# Revit family: d0088496_REVIT-QS
name_source: partatom
category: Mechanical Equipment
revit_build: Autodesk Revit 2017 (Build: 20190507_1515(x64)
units: mm (PartAtom-declared; Revit-internal decimal feet)

## family parameters
Always vertical = Yes
Cut with Voids When Loaded = No
Part Type = Normal
Room Calculation Point = No
Round Connector Dimension = Use Radius
Shared = No
Work Plane-Based = No

## types (134) — shared parameters
Apparent Load = 240 VA
Current = 2 A
Description = PVI QuickDraw® - Steam Storage
Disclaimer = This rendering is for building modeling purposes only. Submittal/catalog is still the contract document. PVI reserves the right to change design and specification without notice.
Drain Angle = 0.00°
Energy Radius = 14 1/2"
Frequency = 60 Hz
Manufacturer = PVI Industries, LLC
Phase = 1
Rear Access Extension = 0"
Relief Valve NPT = 1"
Relief Valve Radius = 1/2"
URL = www.pvi.com
Voltage = 120 V

## per-type parameters (varying)
- 900 L 150A-QS: Assembly Code=D3040400; Cold Water Extension=19 1/8"; Cold Water NPT=2"; Cold Water Radius=1"; Control Panel Extension=25 1/8"; Drain Extension=22"; Drain NPT=1"; Drain Radius=1/2"; Enclosure Location=15 1/2"; Energy Extension=34 1/8"; Flat Side Distance=34"; Front Skid Extension=72 5/8"; Height to Cold Inlet=14 13/16"; Height to Drain=1 3/4"; Height to Energy=26 1/2"; Height to Hot Outlet=44 7/8"; Height to Relief=51 7/8"; Hot Outlet Angle=0.00°; Hot Water Extension=19 1/8"; Hot Water NPT=2"; Hot Water Radius=1"; Large Visibility=No; Rear Skid Extension=18 1/8"; Recovery Rate 40F to 140F @15psi=900 gph; Relief Extension=21 1/8"; Skid Center Dist=8 1/2"; Skid Length=54 1/2"; Skid Spacing=17"; Small Visibility=Yes; Steam Return NPT=1"; Steam Return Radius=1/2"; Steam Return Y=2 9/16"; Steam Supply Conn Y=1 7/8"; Steam Supply NPT=2"; Steam Supply Radius=1"; Steam Supply Total Z=18"; Steam Supply X=14 1/16"; Steam Supply Y=1 7/8"; Steam Supply Z=9 1/16"; Steam flow lb/h 40F to 140F @15psi=780; Supply Pipe Conn Y=1 7/8"; U Tube Extension=8 15/16"; U Tube Radius=3 3/8"; Unit Height=63"; Unit Radius=18 1/8"; Weight=1095
- 830 L 150A-QSD: Assembly Code=D3040400; Cold Water Extension=19 1/8"; Cold Water NPT=2"; Cold Water Radius=1"; Control Panel Extension=25 1/8"; Drain Extension=22"; Drain NPT=1"; Drain Radius=1/2"; Enclosure Location=15 1/2"; Energy Extension=34 1/8"; Flat Side Distance=34"; Front Skid Extension=73 1/8"; Height to Cold Inlet=14 13/16"; Height to Drain=1 3/4"; Height to Energy=26 1/2"; Height to Hot Outlet=44 7/8"; Height to Relief=51 7/8"; Hot Outlet Angle=0.00°; Hot Water Extension=19 1/8"; Hot Water NPT=2"; Hot Water Radius=1"; Large Visibility=Yes; Rear Skid Extension=18 1/8"; Recovery Rate 40F to 140F @15psi=830 gph; Relief Extension=21 1/8"; Skid Center Dist=8 1/2"; Skid Length=55"; Skid Spacing=17"; Small Visibility=No; Steam Return NPT=1"; Steam Return Radius=1/2"; Steam Return Y=3 3/8"; Steam Supply Conn Y=2 1/4"; Steam Supply NPT=1 1/2"; Steam Supply Radius=3/4"; Steam Supply Total Z=18"; Steam Supply X=14 1/16"; Steam Supply Y=1 7/8"; Steam Supply Z=9 1/16"; Steam flow lb/h 40F to 140F @15psi=720; Supply Pipe Conn Y=4 1/8"; U Tube Extension=8 15/16"; U Tube Radius=4 5/16"; Unit Height=63"; Unit Radius=18 1/8"; Weight=1156
- 520 L 215A-QS: Assembly Code=D3040400; Cold Water Extension=19 1/8"; Cold Water NPT=2"; Cold Water Radius=1"; Control Panel Extension=25 1/8"; Drain Extension=22"; Drain NPT=1"; Drain Radius=1/2"; Enclosure Location=26"; Energy Extension=34 1/8"; Flat Side Distance=34"; Front Skid Extension=72 5/8"; Height to Cold Inlet=14 13/16"; Height to Drain=1 3/4"; Height to Energy=26 1/2"; Height to Hot Outlet=64 1/4"; Height to Relief=64 7/8"; Hot Outlet Angle=90.00°; Hot Water Extension=19 1/8"; Hot Water NPT=2"; Hot Water Radius=1"; Large Visibility=No; Rear Skid Extension=18 1/8"; Recovery Rate 40F to 140F @15psi=520 gph; Relief Extension=21 1/8"; Skid Center Dist=8 1/2"; Skid Length=54 1/2"; Skid Spacing=17"; Small Visibility=Yes; Steam Return NPT=3/4"; Steam Return Radius=3/8"; Steam Return Y=1 11/16"; Steam Supply Conn Y=1 5/16"; Steam Supply NPT=1 1/2"; Steam Supply Radius=3/4"; Steam Supply Total Z=15 5/16"; Steam Supply X=12 11/16"; Steam Supply Y=1 5/16"; Steam Supply Z=7 1/8"; Steam flow lb/h 40F to 140F @15psi=450; Supply Pipe Conn Y=1 5/16"; U Tube Extension=8 3/16"; U Tube Radius=2 1/4"; Unit Height=76"; Unit Radius=18 1/8"; Weight=1170
- 520 L 175A-QS: Assembly Code=D3040400; Cold Water Extension=19 1/8"; Cold Water NPT=2"; Cold Water Radius=1"; Control Panel Extension=25 1/8"; Drain Extension=22"; Drain NPT=1"; Drain Radius=1/2"; Enclosure Location=20"; Energy Extension=34 1/8"; Flat Side Distance=34"; Front Skid Extension=72 5/8"; Height to Cold Inlet=14 13/16"; Height to Drain=1 3/4"; Height to Energy=26 1/2"; Height to Hot Outlet=50 7/8"; Height to Relief=57 7/8"; Hot Outlet Angle=0.00°; Hot Water Extension=19 1/8"; Hot Water NPT=2"; Hot Water Radius=1"; Large Visibility=No; Rear Skid Extension=18 1/8"; Recovery Rate 40F to 140F @15psi=520 gph; Relief Extension=21 1/8"; Skid Center Dist=8 1/2"; Skid Length=54 1/2"; Skid Spacing=17"; Small Visibility=Yes; Steam Return NPT=3/4"; Steam Return Radius=3/8"; Steam Return Y=1 11/16"; Steam Supply Conn Y=1 5/16"; Steam Supply NPT=1 1/2"; Steam Supply Radius=3/4"; Steam Supply Total Z=15 5/16"; Steam Supply X=12 11/16"; Steam Supply Y=1 5/16"; Steam Supply Z=7 1/8"; Steam flow lb/h 40F to 140F @15psi=450; Supply Pipe Conn Y=1 5/16"; U Tube Extension=8 3/16"; U Tube Radius=2 1/4"; Unit Height=69"; Unit Radius=18 1/8"; Weight=1080
- 440 L 215A-QSD: Assembly Code=D3040400; Cold Water Extension=19 1/8"; Cold Water NPT=2"; Cold Water Radius=1"; Control Panel Extension=25 1/8"; Drain Extension=22"; Drain NPT=1"; Drain Radius=1/2"; Enclosure Location=26"; Energy Extension=34 1/8"; Flat Side Distance=34"; Front Skid Extension=72 5/8"; Height to Cold Inlet=14 13/16"; Height to Drain=1 3/4"; Height to Energy=26 1/2"; Height to Hot Outlet=64 1/4"; Height to Relief=64 7/8"; Hot Outlet Angle=90.00°; Hot Water Extension=19 1/8"; Hot Water NPT=2"; Hot Water Radius=1"; Large Visibility=No; Rear Skid Extension=18 1/8"; Recovery Rate 40F to 140F @15psi=440 gph; Relief Extension=21 1/8"; Skid Center Dist=8 1/2"; Skid Length=54 1/2"; Skid Spacing=17"; Small Visibility=Yes; Steam Return NPT=3/4"; Steam Return Radius=3/8"; Steam Return Y=1 11/16"; Steam Supply Conn Y=1 5/16"; Steam Supply NPT=1"; Steam Supply Radius=1/2"; Steam Supply Total Z=15 5/16"; Steam Supply X=12 11/16"; Steam Supply Y=1 5/16"; Steam Supply Z=7 1/8"; Steam flow lb/h 40F to 140F @15psi=380; Supply Pipe Conn Y=1 5/16"; U Tube Extension=8 3/16"; U Tube Radius=2 1/4"; Unit Height=76"; Unit Radius=18 1/8"; Weight=1220
- 440 L 175A-QSD: Assembly Code=D3040400; Cold Water Extension=19 1/8"; Cold Water NPT=2"; Cold Water Radius=1"; Control Panel Extension=25 1/8"; Drain Extension=22"; Drain NPT=1"; Drain Radius=1/2"; Enclosure Location=20"; Energy Extension=34 1/8"; Flat Side Distance=34"; Front Skid Extension=73 1/8"; Height to Cold Inlet=14 13/16"; Height to Drain=1 3/4"; Height to Energy=26 1/2"; Height to Hot Outlet=50 7/8"; Height to Relief=57 7/8"; Hot Outlet Angle=0.00°; Hot Water Extension=19 1/8"; Hot Water NPT=2"; Hot Water Radius=1"; Large Visibility=No; Rear Skid Extension=18 1/8"; Recovery Rate 40F to 140F @15psi=440 gph; Relief Extension=21 1/8"; Skid Center Dist=8 1/2"; Skid Length=55"; Skid Spacing=17"; Small Visibility=Yes; Steam Return NPT=3/4"; Steam Return Radius=3/8"; Steam Return Y=1 11/16"; Steam Supply Conn Y=1 5/16"; Steam Supply NPT=1"; Steam Supply Radius=1/2"; Steam Supply Total Z=15 5/16"; Steam Supply X=12 11/16"; Steam Supply Y=1 5/16"; Steam Supply Z=7 1/8"; Steam flow lb/h 40F to 140F @15psi=380; Supply Pipe Conn Y=1 5/16"; U Tube Extension=8 3/16"; U Tube Radius=2 1/4"; Unit Height=69"; Unit Radius=18 1/8"; Weight=1130
- 520 L 150A-QS: Assembly Code=D3040400; Cold Water Extension=19 1/8"; Cold Water NPT=2"; Cold Water Radius=1"; Control Panel Extension=25 1/8"; Drain Extension=22"; Drain NPT=1"; Drain Radius=1/2"; Enclosure Location=15 1/2"; Energy Extension=34 1/8"; Flat Side Distance=34"; Front Skid Extension=72 5/8"; Height to Cold Inlet=14 13/16"; Height to Drain=1 3/4"; Height to Energy=26 1/2"; Height to Hot Outlet=44 7/8"; Height to Relief=51 7/8"; Hot Outlet Angle=0.00°; Hot Water Extension=19 1/8"; Hot Water NPT=2"; Hot Water Radius=1"; Large Visibility=No; Rear Skid Extension=18 1/8"; Recovery Rate 40F to 140F @15psi=520 gph; Relief Extension=21 1/8"; Skid Center Dist=8 1/2"; Skid Length=54 1/2"; Skid Spacing=17"; Small Visibility=Yes; Steam Return NPT=3/4"; Steam Return Radius=3/8"; Steam Return Y=1 11/16"; Steam Supply Conn Y=1 5/16"; Steam Supply NPT=1 1/2"; Steam Supply Radius=3/4"; Steam Supply Total Z=15 5/16"; Steam Supply X=12 11/16"; Steam Supply Y=1 5/16"; Steam Supply Z=7 1/8"; Steam flow lb/h 40F to 140F @15psi=450; Supply Pipe Conn Y=1 5/16"; U Tube Extension=8 3/16"; U Tube Radius=2 1/4"; Unit Height=63"; Unit Radius=18 1/8"; Weight=1010
- 3790 L 215A-QSD: Assembly Code=D3040400; Cold Water Extension=19 1/8"; Cold Water NPT=2"; Cold Water Radius=1"; Control Panel Extension=25 1/8"; Drain Extension=22"; Drain NPT=1"; Drain Radius=1/2"; Enclosure Location=26"; Energy Extension=34 1/8"; Flat Side Distance=34"; Front Skid Extension=72 5/8"; Height to Cold Inlet=14 13/16"; Height to Drain=1 3/4"; Height to Energy=26 1/2"; Height to Hot Outlet=64 1/4"; Height to Relief=64 7/8"; Hot Outlet Angle=90.00°; Hot Water Extension=19 1/8"; Hot Water NPT=2"; Hot Water Radius=1"; Large Visibility=Yes; Rear Skid Extension=18 1/8"; Recovery Rate 40F to 140F @15psi=3790 gph; Relief Extension=21 1/8"; Skid Center Dist=8 1/2"; Skid Length=54 1/2"; Skid Spacing=17"; Small Visibility=No; Steam Return NPT=2"; Steam Return Radius=1"; Steam Return Y=4 5/8"; Steam Supply Conn Y=3 13/16"; Steam Supply NPT=2 1/2"; Steam Supply Radius=1 1/4"; Steam Supply Total Z=18 15/16"; Steam Supply X=25 1/2"; Steam Supply Y=8 9/16"; Steam Supply Z=10 13/16"; Steam flow lb/h 40F to 140F @15psi=3300; Supply Pipe Conn Y=12 3/8"; U Tube Extension=8 1/8"; U Tube Radius=6 3/8"; Unit Height=76"; Unit Radius=18 1/8"; Weight=1670
- 3790 L 175A-QSD: Assembly Code=D3040400; Cold Water Extension=19 1/8"; Cold Water NPT=2"; Cold Water Radius=1"; Control Panel Extension=25 1/8"; Drain Extension=22"; Drain NPT=1"; Drain Radius=1/2"; Enclosure Location=20"; Energy Extension=34 1/8"; Flat Side Distance=34"; Front Skid Extension=72 5/8"; Height to Cold Inlet=14 13/16"; Height to Drain=1 3/4"; Height to Energy=26 1/2"; Height to Hot Outlet=50 7/8"; Height to Relief=57 7/8"; Hot Outlet Angle=0.00°; Hot Water Extension=19 1/8"; Hot Water NPT=2"; Hot Water Radius=1"; Large Visibility=Yes; Rear Skid Extension=18 1/8"; Recovery Rate 40F to 140F @15psi=3790 gph; Relief Extension=21 1/8"; Skid Center Dist=8 1/2"; Skid Length=54 1/2"; Skid Spacing=17"; Small Visibility=No; Steam Return NPT=2"; Steam Return Radius=1"; Steam Return Y=4 5/8"; Steam Supply Conn Y=3 13/16"; Steam Supply NPT=2 1/2"; Steam Supply Radius=1 1/4"; Steam Supply Total Z=18 15/16"; Steam Supply X=25 1/2"; Steam Supply Y=8 9/16"; Steam Supply Z=10 13/16"; Steam flow lb/h 40F to 140F @15psi=3300; Supply Pipe Conn Y=12 3/8"; U Tube Extension=8 1/8"; U Tube Radius=6 3/8"; Unit Height=69"; Unit Radius=18 1/8"; Weight=1580
- 380 L 215A-QS: Assembly Code=D3040400; Cold Water Extension=19 1/8"; Cold Water NPT=2"; Cold Water Radius=1"; Control Panel Extension=25 1/8"; Drain Extension=22"; Drain NPT=1"; Drain Radius=1/2"; Enclosure Location=26"; Energy Extension=23 1/8"; Flat Side Distance=34"; Front Skid Extension=55 1/8"; Height to Cold Inlet=14 13/16"; Height to Drain=1 3/4"; Height to Energy=26 1/2"; Height to Hot Outlet=64 1/4"; Height to Relief=64 7/8"; Hot Outlet Angle=90.00°; Hot Water Extension=19 1/8"; Hot Water NPT=2"; Hot Water Radius=1"; Large Visibility=No; Rear Skid Extension=18 1/8"; Recovery Rate 40F to 140F @15psi=380 gph; Relief Extension=21 1/8"; Skid Center Dist=8 1/2"; Skid Length=37"; Skid Spacing=17"; Small Visibility=Yes; Steam Return NPT=3/4"; Steam Return Radius=3/8"; Steam Return Y=1 11/16"; Steam Supply Conn Y=1 5/16"; Steam Supply NPT=1"; Steam Supply Radius=1/2"; Steam Supply Total Z=15 5/16"; Steam Supply X=12 11/16"; Steam Supply Y=1 5/16"; Steam Supply Z=7 1/8"; Steam flow lb/h 40F to 140F @15psi=330; Supply Pipe Conn Y=1 5/16"; U Tube Extension=8 3/16"; U Tube Radius=2 1/4"; Unit Height=76"; Unit Radius=18 1/8"; Weight=1070
- 380 L 175A-QS: Assembly Code=D3040400; Cold Water Extension=19 1/8"; Cold Water NPT=2"; Cold Water Radius=1"; Control Panel Extension=25 1/8"; Drain Extension=22"; Drain NPT=1"; Drain Radius=1/2"; Enclosure Location=20"; Energy Extension=23 1/8"; Flat Side Distance=34"; Front Skid Extension=55 1/8"; Height to Cold Inlet=14 13/16"; Height to Drain=1 3/4"; Height to Energy=26 1/2"; Height to Hot Outlet=50 7/8"; Height to Relief=57 7/8"; Hot Outlet Angle=0.00°; Hot Water Extension=19 1/8"; Hot Water NPT=2"; Hot Water Radius=1"; Large Visibility=No; Rear Skid Extension=18 1/8"; Recovery Rate 40F to 140F @15psi=380 gph; Relief Extension=21 1/8"; Skid Center Dist=8 1/2"; Skid Length=37"; Skid Spacing=17"; Small Visibility=Yes; Steam Return NPT=3/4"; Steam Return Radius=3/8"; Steam Return Y=1 11/16"; Steam Supply Conn Y=1 5/16"; Steam Supply NPT=1"; Steam Supply Radius=1/2"; Steam Supply Total Z=15 5/16"; Steam Supply X=12 11/16"; Steam Supply Y=1 5/16"; Steam Supply Z=7 1/8"; Steam flow lb/h 40F to 140F @15psi=330; Supply Pipe Conn Y=1 5/16"; U Tube Extension=8 3/16"; U Tube Radius=2 1/4"; Unit Height=69"; Unit Radius=18 1/8"; Weight=980
- 440 L 150A-QSD: Assembly Code=D3040400; Cold Water Extension=19 1/8"; Cold Water NPT=2"; Cold Water Radius=1"; Control Panel Extension=25 1/8"; Drain Extension=22"; Drain NPT=1"; Drain Radius=1/2"; Enclosure Location=15 1/2"; Energy Extension=34 1/8"; Flat Side Distance=34"; Front Skid Extension=73 1/8"; Height to Cold Inlet=14 13/16"; Height to Drain=1 3/4"; Height to Energy=26 1/2"; Height to Hot Outlet=44 7/8"; Height to Relief=51 7/8"; Hot Outlet Angle=0.00°; Hot Water Extension=19 1/8"; Hot Water NPT=2"; Hot Water Radius=1"; Large Visibility=No; Rear Skid Extension=18 1/8"; Recovery Rate 40F to 140F @15psi=440 gph; Relief Extension=21 1/8"; Skid Center Dist=8 1/2"; Skid Length=55"; Skid Spacing=17"; Small Visibility=Yes; Steam Return NPT=3/4"; Steam Return Radius=3/8"; Steam Return Y=1 11/16"; Steam Supply Conn Y=1 5/16"; Steam Supply NPT=1"; Steam Supply Radius=1/2"; Steam Supply Total Z=15 5/16"; Steam Supply X=12 11/16"; Steam Supply Y=1 5/16"; Steam Supply Z=7 1/8"; Steam flow lb/h 40F to 140F @15psi=380; Supply Pipe Conn Y=1 5/16"; U Tube Extension=8 3/16"; U Tube Radius=2 1/4"; Unit Height=63"; Unit Radius=18 1/8"; Weight=1060
- 3120 L 215A-QS: Assembly Code=D3040400; Cold Water Extension=19 1/8"; Cold Water NPT=2"; Cold Water Radius=1"; Control Panel Extension=25 1/8"; Drain Extension=22"; Drain NPT=1"; Drain Radius=1/2"; Enclosure Location=26"; Energy Extension=34 1/8"; Flat Side Distance=34"; Front Skid Extension=72 5/8"; Height to Cold Inlet=14 13/16"; Height to Drain=1 3/4"; Height to Energy=26 1/2"; Height to Hot Outlet=64 1/4"; Height to Relief=64 7/8"; Hot Outlet Angle=90.00°; Hot Water Extension=19 1/8"; Hot Water NPT=2"; Hot Water Radius=1"; Large Visibility=Yes; Rear Skid Extension=18 1/8"; Recovery Rate 40F to 140F @15psi=3120 gph; Relief Extension=21 1/8"; Skid Center Dist=8 1/2"; Skid Length=54 1/2"; Skid Spacing=17"; Small Visibility=No; Steam Return NPT=2"; Steam Return Radius=1"; Steam Return Y=4 1/16"; Steam Supply Conn Y=2 11/16"; Steam Supply NPT=2 1/2"; Steam Supply Radius=1 1/4"; Steam Supply Total Z=19 3/4"; Steam Supply X=25 1/2"; Steam Supply Y=8 9/16"; Steam Supply Z=10 13/16"; Steam flow lb/h 40F to 140F @15psi=2700; Supply Pipe Conn Y=11 1/4"; U Tube Extension=8 15/16"; U Tube Radius=5 3/8"; Unit Height=76"; Unit Radius=18 1/8"; Weight=1370
- 3120 L 175A-QS: Assembly Code=D3040400; Cold Water Extension=19 1/8"; Cold Water NPT=2"; Cold Water Radius=1"; Control Panel Extension=25 1/8"; Drain Extension=22"; Drain NPT=1"; Drain Radius=1/2"; Enclosure Location=20"; Energy Extension=34 1/8"; Flat Side Distance=34"; Front Skid Extension=72 5/8"; Height to Cold Inlet=14 13/16"; Height to Drain=1 3/4"; Height to Energy=26 1/2"; Height to Hot Outlet=50 7/8"; Height to Relief=57 7/8"; Hot Outlet Angle=0.00°; Hot Water Extension=19 1/8"; Hot Water NPT=2"; Hot Water Radius=1"; Large Visibility=Yes; Rear Skid Extension=18 1/8"; Recovery Rate 40F to 140F @15psi=3120 gph; Relief Extension=21 1/8"; Skid Center Dist=8 1/2"; Skid Length=54 1/2"; Skid Spacing=17"; Small Visibility=No; Steam Return NPT=2"; Steam Return Radius=1"; Steam Return Y=4 1/16"; Steam Supply Conn Y=2 11/16"; Steam Supply NPT=2 1/2"; Steam Supply Radius=1 1/4"; Steam Supply Total Z=19 3/4"; Steam Supply X=25 1/2"; Steam Supply Y=8 9/16"; Steam Supply Z=10 13/16"; Steam flow lb/h 40F to 140F @15psi=2700; Supply Pipe Conn Y=11 1/4"; U Tube Extension=8 15/16"; U Tube Radius=5 3/8"; Unit Height=69"; Unit Radius=18 1/8"; Weight=1280
- 330 L 215A-QSD: Assembly Code=D3040400; Cold Water Extension=19 1/8"; Cold Water NPT=2"; Cold Water Radius=1"; Control Panel Extension=25 1/8"; Drain Extension=22"; Drain NPT=1"; Drain Radius=1/2"; Enclosure Location=26"; Energy Extension=23 1/8"; Flat Side Distance=34"; Front Skid Extension=55 1/8"; Height to Cold Inlet=14 13/16"; Height to Drain=1 3/4"; Height to Energy=26 1/2"; Height to Hot Outlet=64 1/4"; Height to Relief=64 7/8"; Hot Outlet Angle=90.00°; Hot Water Extension=19 1/8"; Hot Water NPT=2"; Hot Water Radius=1"; Large Visibility=No; Rear Skid Extension=18 1/8"; Recovery Rate 40F to 140F @15psi=330 gph; Relief Extension=21 1/8"; Skid Center Dist=8 1/2"; Skid Length=37"; Skid Spacing=17"; Small Visibility=Yes; Steam Return NPT=3/4"; Steam Return Radius=3/8"; Steam Return Y=1 11/16"; Steam Supply Conn Y=1 5/16"; Steam Supply NPT=1"; Steam Supply Radius=1/2"; Steam Supply Total Z=15 5/16"; Steam Supply X=12 11/16"; Steam Supply Y=1 5/16"; Steam Supply Z=7 1/8"; Steam flow lb/h 40F to 140F @15psi=280; Supply Pipe Conn Y=1 5/16"; U Tube Extension=8 3/16"; U Tube Radius=2 1/4"; Unit Height=76"; Unit Radius=18 1/8"; Weight=1070
- 330 L 175A-QSD: Assembly Code=D3040400; Cold Water Extension=19 1/8"; Cold Water NPT=2"; Cold Water Radius=1"; Control Panel Extension=25 1/8"; Drain Extension=22"; Drain NPT=1"; Drain Radius=1/2"; Enclosure Location=20"; Energy Extension=23 1/8"; Flat Side Distance=34"; Front Skid Extension=55 1/8"; Height to Cold Inlet=14 13/16"; Height to Drain=1 3/4"; Height to Energy=26 1/2"; Height to Hot Outlet=50 7/8"; Height to Relief=57 7/8"; Hot Outlet Angle=0.00°; Hot Water Extension=19 1/8"; Hot Water NPT=2"; Hot Water Radius=1"; Large Visibility=No; Rear Skid Extension=18 1/8"; Recovery Rate 40F to 140F @15psi=330 gph; Relief Extension=21 1/8"; Skid Center Dist=8 1/2"; Skid Length=37"; Skid Spacing=17"; Small Visibility=Yes; Steam Return NPT=3/4"; Steam Return Radius=3/8"; Steam Return Y=1 11/16"; Steam Supply Conn Y=1 5/16"; Steam Supply NPT=1"; Steam Supply Radius=1/2"; Steam Supply Total Z=15 5/16"; Steam Supply X=12 11/16"; Steam Supply Y=1 5/16"; Steam Supply Z=7 1/8"; Steam flow lb/h 40F to 140F @15psi=280; Supply Pipe Conn Y=1 5/16"; U Tube Extension=8 3/16"; U Tube Radius=2 1/4"; Unit Height=69"; Unit Radius=18 1/8"; Weight=980
- 3800 L 150A-QS: Assembly Code=D3040400; Cold Water Extension=19 1/8"; Cold Water NPT=2"; Cold Water Radius=1"; Control Panel Extension=25 1/8"; Drain Extension=22"; Drain NPT=1"; Drain Radius=1/2"; Enclosure Location=15 1/2"; Energy Extension=34 1/8"; Flat Side Distance=34"; Front Skid Extension=72 5/8"; Height to Cold Inlet=14 13/16"; Height to Drain=1 3/4"; Height to Energy=26 1/2"; Height to Hot Outlet=44 7/8"; Height to Relief=51 7/8"; Hot Outlet Angle=0.00°; Hot Water Extension=19 1/8"; Hot Water NPT=2"; Hot Water Radius=1"; Large Visibility=Yes; Rear Skid Extension=18 1/8"; Recovery Rate 40F to 140F @15psi=3790 gph; Relief Extension=21 1/8"; Skid Center Dist=8 1/2"; Skid Length=54 1/2"; Skid Spacing=17"; Small Visibility=No; Steam Return NPT=2"; Steam Return Radius=1"; Steam Return Y=4 5/8"; Steam Supply Conn Y=3 13/16"; Steam Supply NPT=2 1/2"; Steam Supply Radius=1 1/4"; Steam Supply Total Z=18 15/16"; Steam Supply X=25 1/2"; Steam Supply Y=8 9/16"; Steam Supply Z=10 13/16"; Steam flow lb/h 40F to 140F @15psi=3300; Supply Pipe Conn Y=12 3/8"; U Tube Extension=8 1/8"; U Tube Radius=6 3/8"; Unit Height=63"; Unit Radius=18 1/8"; Weight=1335
- 380 L 150A-QS: Assembly Code=D3040400; Cold Water Extension=19 1/8"; Cold Water NPT=2"; Cold Water Radius=1"; Control Panel Extension=25 1/8"; Drain Extension=22"; Drain NPT=1"; Drain Radius=1/2"; Enclosure Location=15 1/2"; Energy Extension=23 1/8"; Flat Side Distance=34"; Front Skid Extension=55 1/8"; Height to Cold Inlet=14 13/16"; Height to Drain=1 3/4"; Height to Energy=26 1/2"; Height to Hot Outlet=44 7/8"; Height to Relief=51 7/8"; Hot Outlet Angle=0.00°; Hot Water Extension=19 1/8"; Hot Water NPT=2"; Hot Water Radius=1"; Large Visibility=No; Rear Skid Extension=18 1/8"; Recovery Rate 40F to 140F @15psi=380 gph; Relief Extension=21 1/8"; Skid Center Dist=8 1/2"; Skid Length=37"; Skid Spacing=17"; Small Visibility=Yes; Steam Return NPT=3/4"; Steam Return Radius=3/8"; Steam Return Y=1 11/16"; Steam Supply Conn Y=1 5/16"; Steam Supply NPT=1"; Steam Supply Radius=1/2"; Steam Supply Total Z=15 5/16"; Steam Supply X=12 11/16"; Steam Supply Y=1 5/16"; Steam Supply Z=7 1/8"; Steam flow lb/h 40F to 140F @15psi=330; Supply Pipe Conn Y=1 5/16"; U Tube Extension=8 3/16"; U Tube Radius=2 1/4"; Unit Height=63"; Unit Radius=18 1/8"; Weight=910
- 3790 L 150A-QSD: Assembly Code=D3040400; Cold Water Extension=19 1/8"; Cold Water NPT=2"; Cold Water Radius=1"; Control Panel Extension=25 1/8"; Drain Extension=22"; Drain NPT=1"; Drain Radius=1/2"; Enclosure Location=15 1/2"; Energy Extension=34 1/8"; Flat Side Distance=34"; Front Skid Extension=73 1/8"; Height to Cold Inlet=14 13/16"; Height to Drain=1 3/4"; Height to Energy=26 1/2"; Height to Hot Outlet=44 7/8"; Height to Relief=51 7/8"; Hot Outlet Angle=0.00°; Hot Water Extension=19 1/8"; Hot Water NPT=2"; Hot Water Radius=1"; Large Visibility=Yes; Rear Skid Extension=18 1/8"; Recovery Rate 40F to 140F @15psi=3790 gph; Relief Extension=21 1/8"; Skid Center Dist=8 1/2"; Skid Length=55"; Skid Spacing=17"; Small Visibility=No; Steam Return NPT=2"; Steam Return Radius=1"; Steam Return Y=5 1/16"; Steam Supply Conn Y=3 11/16"; Steam Supply NPT=2 1/2"; Steam Supply Radius=1 1/4"; Steam Supply Total Z=18 15/16"; Steam Supply X=25 1/2"; Steam Supply Y=8 9/16"; Steam Supply Z=10 13/16"; Steam flow lb/h 40F to 140F @15psi=3300; Supply Pipe Conn Y=12 1/4"; U Tube Extension=8 1/8"; U Tube Radius=6 3/8"; Unit Height=63"; Unit Radius=18 1/8"; Weight=1510
- 2650 L 215A-QSD: Assembly Code=D3040400; Cold Water Extension=19 1/8"; Cold Water NPT=2"; Cold Water Radius=1"; Control Panel Extension=25 1/8"; Drain Extension=22"; Drain NPT=1"; Drain Radius=1/2"; Enclosure Location=26"; Energy Extension=34 1/8"; Flat Side Distance=34"; Front Skid Extension=72 5/8"; Height to Cold Inlet=14 13/16"; Height to Drain=1 3/4"; Height to Energy=26 1/2"; Height to Hot Outlet=64 1/4"; Height to Relief=64 7/8"; Hot Outlet Angle=90.00°; Hot Water Extension=19 1/8"; Hot Water NPT=2"; Hot Water Radius=1"; Large Visibility=Yes; Rear Skid Extension=18 1/8"; Recovery Rate 40F to 140F @15psi=2650 gph; Relief Extension=21 1/8"; Skid Center Dist=8 1/2"; Skid Length=54 1/2"; Skid Spacing=17"; Small Visibility=No; Steam Return NPT=2"; Steam Return Radius=1"; Steam Return Y=4 1/16"; Steam Supply Conn Y=2 11/16"; Steam Supply NPT=2 1/2"; Steam Supply Radius=1 1/4"; Steam Supply Total Z=19 3/4"; Steam Supply X=25 1/2"; Steam Supply Y=8 9/16"; Steam Supply Z=10 13/16"; Steam flow lb/h 40F to 140F @15psi=2300; Supply Pipe Conn Y=11 1/4"; U Tube Extension=8 15/16"; U Tube Radius=5 3/8"; Unit Height=76"; Unit Radius=18 1/8"; Weight=1520
- 2650 L 175A-QSD: Assembly Code=D3040400; Cold Water Extension=19 1/8"; Cold Water NPT=2"; Cold Water Radius=1"; Control Panel Extension=25 1/8"; Drain Extension=22"; Drain NPT=1"; Drain Radius=1/2"; Enclosure Location=20"; Energy Extension=34 1/8"; Flat Side Distance=34"; Front Skid Extension=72 5/8"; Height to Cold Inlet=14 13/16"; Height to Drain=1 3/4"; Height to Energy=26 1/2"; Height to Hot Outlet=50 7/8"; Height to Relief=57 7/8"; Hot Outlet Angle=0.00°; Hot Water Extension=19 1/8"; Hot Water NPT=2"; Hot Water Radius=1"; Large Visibility=Yes; Rear Skid Extension=18 1/8"; Recovery Rate 40F to 140F @15psi=2650 gph; Relief Extension=21 1/8"; Skid Center Dist=8 1/2"; Skid Length=54 1/2"; Skid Spacing=17"; Small Visibility=No; Steam Return NPT=2"; Steam Return Radius=1"; Steam Return Y=4 1/16"; Steam Supply Conn Y=2 11/16"; Steam Supply NPT=2 1/2"; Steam Supply Radius=1 1/4"; Steam Supply Total Z=19 3/4"; Steam Supply X=25 1/2"; Steam Supply Y=8 9/16"; Steam Supply Z=10 13/16"; Steam flow lb/h 40F to 140F @15psi=2300; Supply Pipe Conn Y=11 1/4"; U Tube Extension=8 15/16"; U Tube Radius=5 3/8"; Unit Height=69"; Unit Radius=18 1/8"; Weight=1430
- 330 L 150A-QSD: Assembly Code=D3040400; Cold Water Extension=19 1/8"; Cold Water NPT=2"; Cold Water Radius=1"; Control Panel Extension=25 1/8"; Drain Extension=22"; Drain NPT=1"; Drain Radius=1/2"; Enclosure Location=15 1/2"; Energy Extension=23 1/8"; Flat Side Distance=34"; Front Skid Extension=55 1/8"; Height to Cold Inlet=14 13/16"; Height to Drain=1 3/4"; Height to Energy=26 1/2"; Height to Hot Outlet=44 7/8"; Height to Relief=51 7/8"; Hot Outlet Angle=0.00°; Hot Water Extension=19 1/8"; Hot Water NPT=2"; Hot Water Radius=1"; Large Visibility=No; Rear Skid Extension=18 1/8"; Recovery Rate 40F to 140F @15psi=330 gph; Relief Extension=21 1/8"; Skid Center Dist=8 1/2"; Skid Length=37"; Skid Spacing=17"; Small Visibility=Yes; Steam Return NPT=3/4"; Steam Return Radius=3/8"; Steam Return Y=1 11/16"; Steam Supply Conn Y=1 5/16"; Steam Supply NPT=1"; Steam Supply Radius=1/2"; Steam Supply Total Z=15 5/16"; Steam Supply X=12 11/16"; Steam Supply Y=1 5/16"; Steam Supply Z=7 1/8"; Steam flow lb/h 40F to 140F @15psi=280; Supply Pipe Conn Y=1 5/16"; U Tube Extension=8 3/16"; U Tube Radius=2 1/4"; Unit Height=63"; Unit Radius=18 1/8"; Weight=910
- 3120 L 150A-QS: Assembly Code=D3040400; Cold Water Extension=19 1/8"; Cold Water NPT=2"; Cold Water Radius=1"; Control Panel Extension=25 1/8"; Drain Extension=22"; Drain NPT=1"; Drain Radius=1/2"; Enclosure Location=15 1/2"; Energy Extension=34 1/8"; Flat Side Distance=34"; Front Skid Extension=72 5/8"; Height to Cold Inlet=14 13/16"; Height to Drain=1 3/4"; Height to Energy=26 1/2"; Height to Hot Outlet=44 7/8"; Height to Relief=51 7/8"; Hot Outlet Angle=0.00°; Hot Water Extension=19 1/8"; Hot Water NPT=2"; Hot Water Radius=1"; Large Visibility=Yes; Rear Skid Extension=18 1/8"; Recovery Rate 40F to 140F @15psi=3120 gph; Relief Extension=21 1/8"; Skid Center Dist=8 1/2"; Skid Length=54 1/2"; Skid Spacing=17"; Small Visibility=No; Steam Return NPT=2"; Steam Return Radius=1"; Steam Return Y=4 1/16"; Steam Supply Conn Y=2 11/16"; Steam Supply NPT=2 1/2"; Steam Supply Radius=1 1/4"; Steam Supply Total Z=19 3/4"; Steam Supply X=25 1/2"; Steam Supply Y=8 9/16"; Steam Supply Z=10 13/16"; Steam flow lb/h 40F to 140F @15psi=2700; Supply Pipe Conn Y=11 1/4"; U Tube Extension=8 15/16"; U Tube Radius=5 3/8"; Unit Height=63"; Unit Radius=18 1/8"; Weight=1235
- 2650 L 150A-QSD: Assembly Code=D3040400; Cold Water Extension=19 1/8"; Cold Water NPT=2"; Cold Water Radius=1"; Control Panel Extension=25 1/8"; Drain Extension=22"; Drain NPT=1"; Drain Radius=1/2"; Enclosure Location=15 1/2"; Energy Extension=34 1/8"; Flat Side Distance=34"; Front Skid Extension=72 5/8"; Height to Cold Inlet=14 13/16"; Height to Drain=1 3/4"; Height to Energy=26 1/2"; Height to Hot Outlet=44 7/8"; Height to Relief=51 7/8"; Hot Outlet Angle=0.00°; Hot Water Extension=19 1/8"; Hot Water NPT=2"; Hot Water Radius=1"; Large Visibility=Yes; Rear Skid Extension=18 1/8"; Recovery Rate 40F to 140F @15psi=2650 gph; Relief Extension=21 1/8"; Skid Center Dist=8 1/2"; Skid Length=54 1/2"; Skid Spacing=17"; Small Visibility=No; Steam Return NPT=2"; Steam Return Radius=1"; Steam Return Y=4 1/16"; Steam Supply Conn Y=2 13/16"; Steam Supply NPT=2 1/2"; Steam Supply Radius=1 1/4"; Steam Supply Total Z=19 3/4"; Steam Supply X=25 1/2"; Steam Supply Y=8 9/16"; Steam Supply Z=10 13/16"; Steam flow lb/h 40F to 140F @15psi=2300; Supply Pipe Conn Y=11 3/8"; U Tube Extension=8 15/16"; U Tube Radius=5 3/8"; Unit Height=63"; Unit Radius=18 1/8"; Weight=1332
- 1780 L 215A-QS: Assembly Code=D3040400; Cold Water Extension=19 1/8"; Cold Water NPT=2"; Cold Water Radius=1"; Control Panel Extension=25 1/8"; Drain Extension=22"; Drain NPT=1"; Drain Radius=1/2"; Enclosure Location=26"; Energy Extension=34 1/8"; Flat Side Distance=34"; Front Skid Extension=72 5/8"; Height to Cold Inlet=14 13/16"; Height to Drain=1 3/4"; Height to Energy=26 1/2"; Height to Hot Outlet=64 1/4"; Height to Relief=64 7/8"; Hot Outlet Angle=90.00°; Hot Water Extension=19 1/8"; Hot Water NPT=2"; Hot Water Radius=1"; Large Visibility=Yes; Rear Skid Extension=18 1/8"; Recovery Rate 40F to 140F @15psi=1780 gph; Relief Extension=21 1/8"; Skid Center Dist=8 1/2"; Skid Length=54 1/2"; Skid Spacing=17"; Small Visibility=No; Steam Return NPT=1 1/4"; Steam Return Radius=5/8"; Steam Return Y=3 3/8"; Steam Supply Conn Y=2 1/4"; Steam Supply NPT=2 1/2"; Steam Supply Radius=1 1/4"; Steam Supply Total Z=19 3/4"; Steam Supply X=25 1/2"; Steam Supply Y=8 9/16"; Steam Supply Z=10 13/16"; Steam flow lb/h 40F to 140F @15psi=1540; Supply Pipe Conn Y=10 13/16"; U Tube Extension=8 15/16"; U Tube Radius=4 5/16"; Unit Height=76"; Unit Radius=18 1/8"; Weight=1270
- 1780 L 175A-QS: Assembly Code=D3040400; Cold Water Extension=19 1/8"; Cold Water NPT=2"; Cold Water Radius=1"; Control Panel Extension=25 1/8"; Drain Extension=22"; Drain NPT=1"; Drain Radius=1/2"; Enclosure Location=20"; Energy Extension=34 1/8"; Flat Side Distance=34"; Front Skid Extension=72 5/8"; Height to Cold Inlet=14 13/16"; Height to Drain=1 3/4"; Height to Energy=26 1/2"; Height to Hot Outlet=50 7/8"; Height to Relief=57 7/8"; Hot Outlet Angle=0.00°; Hot Water Extension=19 1/8"; Hot Water NPT=2"; Hot Water Radius=1"; Large Visibility=Yes; Rear Skid Extension=18 1/8"; Recovery Rate 40F to 140F @15psi=1780 gph; Relief Extension=21 1/8"; Skid Center Dist=8 1/2"; Skid Length=54 1/2"; Skid Spacing=17"; Small Visibility=No; Steam Return NPT=1 1/4"; Steam Return Radius=5/8"; Steam Return Y=3 3/8"; Steam Supply Conn Y=2 1/4"; Steam Supply NPT=2 1/2"; Steam Supply Radius=1 1/4"; Steam Supply Total Z=19 3/4"; Steam Supply X=25 1/2"; Steam Supply Y=8 9/16"; Steam Supply Z=10 13/16"; Steam flow lb/h 40F to 140F @15psi=1540; Supply Pipe Conn Y=10 13/16"; U Tube Extension=8 15/16"; U Tube Radius=4 5/16"; Unit Height=69"; Unit Radius=18 1/8"; Weight=1180
- 1520 L 215A-QSD: Assembly Code=D3040400; Cold Water Extension=19 1/8"; Cold Water NPT=2"; Cold Water Radius=1"; Control Panel Extension=25 1/8"; Drain Extension=22"; Drain NPT=1"; Drain Radius=1/2"; Enclosure Location=26"; Energy Extension=34 1/8"; Flat Side Distance=34"; Front Skid Extension=72 5/8"; Height to Cold Inlet=14 13/16"; Height to Drain=1 3/4"; Height to Energy=26 1/2"; Height to Hot Outlet=64 1/4"; Height to Relief=64 7/8"; Hot Outlet Angle=90.00°; Hot Water Extension=19 1/8"; Hot Water NPT=2"; Hot Water Radius=1"; Large Visibility=No; Rear Skid Extension=18 1/8"; Recovery Rate 40F to 140F @15psi=1520 gph; Relief Extension=21 1/8"; Skid Center Dist=8 1/2"; Skid Length=54 1/2"; Skid Spacing=17"; Small Visibility=Yes; Steam Return NPT=1 1/4"; Steam Return Radius=5/8"; Steam Return Y=3 3/8"; Steam Supply Conn Y=2 1/4"; Steam Supply NPT=2"; Steam Supply Radius=1"; Steam Supply Total Z=17 1/8"; Steam Supply X=17 3/16"; Steam Supply Y=2 1/4"; Steam Supply Z=8 3/16"; Steam flow lb/h 40F to 140F @15psi=1320; Supply Pipe Conn Y=2 1/4"; U Tube Extension=8 15/16"; U Tube Radius=4 5/16"; Unit Height=76"; Unit Radius=18 1/8"; Weight=1370
- 1520 L 175A-QSD: Assembly Code=D3040400; Cold Water Extension=19 1/8"; Cold Water NPT=2"; Cold Water Radius=1"; Control Panel Extension=25 1/8"; Drain Extension=22"; Drain NPT=1"; Drain Radius=1/2"; Enclosure Location=20"; Energy Extension=34 1/8"; Flat Side Distance=34"; Front Skid Extension=72 5/8"; Height to Cold Inlet=14 13/16"; Height to Drain=1 3/4"; Height to Energy=26 1/2"; Height to Hot Outlet=50 7/8"; Height to Relief=57 7/8"; Hot Outlet Angle=0.00°; Hot Water Extension=19 1/8"; Hot Water NPT=2"; Hot Water Radius=1"; Large Visibility=No; Rear Skid Extension=18 1/8"; Recovery Rate 40F to 140F @15psi=1520 gph; Relief Extension=21 1/8"; Skid Center Dist=8 1/2"; Skid Length=54 1/2"; Skid Spacing=17"; Small Visibility=Yes; Steam Return NPT=1 1/4"; Steam Return Radius=5/8"; Steam Return Y=3 3/8"; Steam Supply Conn Y=2 1/4"; Steam Supply NPT=2"; Steam Supply Radius=1"; Steam Supply Total Z=17 1/8"; Steam Supply X=17 3/16"; Steam Supply Y=2 1/4"; Steam Supply Z=8 3/16"; Steam flow lb/h 40F to 140F @15psi=1320; Supply Pipe Conn Y=2 1/4"; U Tube Extension=8 15/16"; U Tube Radius=4 5/16"; Unit Height=69"; Unit Radius=18 1/8"; Weight=1280
- 1780 L 150A-QS: Assembly Code=D3040400; Cold Water Extension=19 1/8"; Cold Water NPT=2"; Cold Water Radius=1"; Control Panel Extension=25 1/8"; Drain Extension=22"; Drain NPT=1"; Drain Radius=1/2"; Enclosure Location=15 1/2"; Energy Extension=34 1/8"; Flat Side Distance=34"; Front Skid Extension=73 1/8"; Height to Cold Inlet=14 13/16"; Height to Drain=1 3/4"; Height to Energy=26 1/2"; Height to Hot Outlet=44 7/8"; Height to Relief=51 7/8"; Hot Outlet Angle=0.00°; Hot Water Extension=19 1/8"; Hot Water NPT=2"; Hot Water Radius=1"; Large Visibility=Yes; Rear Skid Extension=18 1/8"; Recovery Rate 40F to 140F @15psi=1780 gph; Relief Extension=21 1/8"; Skid Center Dist=8 1/2"; Skid Length=55"; Skid Spacing=17"; Small Visibility=No; Steam Return NPT=1 1/4"; Steam Return Radius=5/8"; Steam Return Y=3 3/8"; Steam Supply Conn Y=2 1/4"; Steam Supply NPT=2 1/2"; Steam Supply Radius=1 1/4"; Steam Supply Total Z=19 3/4"; Steam Supply X=25 1/2"; Steam Supply Y=8 9/16"; Steam Supply Z=10 13/16"; Steam flow lb/h 40F to 140F @15psi=1540; Supply Pipe Conn Y=10 13/16"; U Tube Extension=8 15/16"; U Tube Radius=4 5/16"; Unit Height=63"; Unit Radius=18 1/8"; Weight=1135
- 1520 L 150A-QSD: Assembly Code=D3040400; Cold Water Extension=19 1/8"; Cold Water NPT=2"; Cold Water Radius=1"; Control Panel Extension=25 1/8"; Drain Extension=22"; Drain NPT=1"; Drain Radius=1/2"; Enclosure Location=15 1/2"; Energy Extension=34 1/8"; Flat Side Distance=34"; Front Skid Extension=72 5/8"; Height to Cold Inlet=14 13/16"; Height to Drain=1 3/4"; Height to Energy=26 1/2"; Height to Hot Outlet=44 7/8"; Height to Relief=51 7/8"; Hot Outlet Angle=0.00°; Hot Water Extension=19 1/8"; Hot Water NPT=2"; Hot Water Radius=1"; Large Visibility=No; Rear Skid Extension=18 1/8"; Recovery Rate 40F to 140F @15psi=1520 gph; Relief Extension=21 1/8"; Skid Center Dist=8 1/2"; Skid Length=54 1/2"; Skid Spacing=17"; Small Visibility=Yes; Steam Return NPT=1 1/4"; Steam Return Radius=5/8"; Steam Return Y=3 3/8"; Steam Supply Conn Y=2 1/4"; Steam Supply NPT=2"; Steam Supply Radius=1"; Steam Supply Total Z=17 1/8"; Steam Supply X=17 3/16"; Steam Supply Y=2 1/4"; Steam Supply Z=8 3/16"; Steam flow lb/h 40F to 140F @15psi=1320; Supply Pipe Conn Y=2 1/4"; U Tube Extension=8 15/16"; U Tube Radius=4 5/16"; Unit Height=63"; Unit Radius=18 1/8"; Weight=1176
- 900 L 215A-QS: Assembly Code=D3040400; Cold Water Extension=19 1/8"; Cold Water NPT=2"; Cold Water Radius=1"; Control Panel Extension=25 1/8"; Drain Extension=22"; Drain NPT=1"; Drain Radius=1/2"; Enclosure Location=26"; Energy Extension=34 1/8"; Flat Side Distance=34"; Front Skid Extension=72 5/8"; Height to Cold Inlet=14 13/16"; Height to Drain=1 3/4"; Height to Energy=26 1/2"; Height to Hot Outlet=64 1/4"; Height to Relief=64 7/8"; Hot Outlet Angle=90.00°; Hot Water Extension=19 1/8"; Hot Water NPT=2"; Hot Water Radius=1"; Large Visibility=No; Rear Skid Extension=18 1/8"; Recovery Rate 40F to 140F @15psi=900 gph; Relief Extension=21 1/8"; Skid Center Dist=8 1/2"; Skid Length=54 1/2"; Skid Spacing=17"; Small Visibility=Yes; Steam Return NPT=1"; Steam Return Radius=1/2"; Steam Return Y=2 9/16"; Steam Supply Conn Y=1 7/8"; Steam Supply NPT=2"; Steam Supply Radius=1"; Steam Supply Total Z=18"; Steam Supply X=14 1/16"; Steam Supply Y=1 7/8"; Steam Supply Z=9 1/16"; Steam flow lb/h 40F to 140F @15psi=780; Supply Pipe Conn Y=1 7/8"; U Tube Extension=8 15/16"; U Tube Radius=3 3/8"; Unit Height=76"; Unit Radius=18 1/8"; Weight=1220
- 900 L 175A-QS: Assembly Code=D3040400; Cold Water Extension=19 1/8"; Cold Water NPT=2"; Cold Water Radius=1"; Control Panel Extension=25 1/8"; Drain Extension=22"; Drain NPT=1"; Drain Radius=1/2"; Enclosure Location=20"; Energy Extension=34 1/8"; Flat Side Distance=34"; Front Skid Extension=72 5/8"; Height to Cold Inlet=14 13/16"; Height to Drain=1 3/4"; Height to Energy=26 1/2"; Height to Hot Outlet=50 7/8"; Height to Relief=57 7/8"; Hot Outlet Angle=0.00°; Hot Water Extension=19 1/8"; Hot Water NPT=2"; Hot Water Radius=1"; Large Visibility=No; Rear Skid Extension=18 1/8"; Recovery Rate 40F to 140F @15psi=900 gph; Relief Extension=21 1/8"; Skid Center Dist=8 1/2"; Skid Length=54 1/2"; Skid Spacing=17"; Small Visibility=Yes; Steam Return NPT=1"; Steam Return Radius=1/2"; Steam Return Y=2 9/16"; Steam Supply Conn Y=1 7/8"; Steam Supply NPT=2"; Steam Supply Radius=1"; Steam Supply Total Z=18"; Steam Supply X=14 1/16"; Steam Supply Y=1 7/8"; Steam Supply Z=9 1/16"; Steam flow lb/h 40F to 140F @15psi=780; Supply Pipe Conn Y=1 7/8"; U Tube Extension=8 15/16"; U Tube Radius=3 3/8"; Unit Height=69"; Unit Radius=18 1/8"; Weight=1130
- 830 L 215A-QSD: Assembly Code=D3040400; Cold Water Extension=19 1/8"; Cold Water NPT=2"; Cold Water Radius=1"; Control Panel Extension=25 1/8"; Drain Extension=22"; Drain NPT=1"; Drain Radius=1/2"; Enclosure Location=26"; Energy Extension=34 1/8"; Flat Side Distance=34"; Front Skid Extension=72 5/8"; Height to Cold Inlet=14 13/16"; Height to Drain=1 3/4"; Height to Energy=26 1/2"; Height to Hot Outlet=64 1/4"; Height to Relief=64 7/8"; Hot Outlet Angle=90.00°; Hot Water Extension=19 1/8"; Hot Water NPT=2"; Hot Water Radius=1"; Large Visibility=No; Rear Skid Extension=18 1/8"; Recovery Rate 40F to 140F @15psi=830 gph; Relief Extension=21 1/8"; Skid Center Dist=8 1/2"; Skid Length=54 1/2"; Skid Spacing=17"; Small Visibility=Yes; Steam Return NPT=1"; Steam Return Radius=1/2"; Steam Return Y=2 9/16"; Steam Supply Conn Y=1 7/8"; Steam Supply NPT=1 1/2"; Steam Supply Radius=3/4"; Steam Supply Total Z=18"; Steam Supply X=14 1/16"; Steam Supply Y=1 7/8"; Steam Supply Z=9 1/16"; Steam flow lb/h 40F to 140F @15psi=720; Supply Pipe Conn Y=1 7/8"; U Tube Extension=8 15/16"; U Tube Radius=3 3/8"; Unit Height=76"; Unit Radius=18 1/8"; Weight=1270
- 830 L 175A-QSD: Assembly Code=D3040400; Cold Water Extension=19 1/8"; Cold Water NPT=2"; Cold Water Radius=1"; Control Panel Extension=25 1/8"; Drain Extension=22"; Drain NPT=1"; Drain Radius=1/2"; Enclosure Location=15 1/2"; Energy Extension=34 1/8"; Flat Side Distance=34"; Front Skid Extension=72 5/8"; Height to Cold Inlet=14 13/16"; Height to Drain=1 3/4"; Height to Energy=26 1/2"; Height to Hot Outlet=50 7/8"; Height to Relief=57 7/8"; Hot Outlet Angle=0.00°; Hot Water Extension=19 1/8"; Hot Water NPT=2"; Hot Water Radius=1"; Large Visibility=No; Rear Skid Extension=18 1/8"; Recovery Rate 40F to 140F @15psi=830 gph; Relief Extension=21 1/8"; Skid Center Dist=8 1/2"; Skid Length=54 1/2"; Skid Spacing=17"; Small Visibility=Yes; Steam Return NPT=1"; Steam Return Radius=1/2"; Steam Return Y=2 9/16"; Steam Supply Conn Y=1 7/8"; Steam Supply NPT=1 1/2"; Steam Supply Radius=3/4"; Steam Supply Total Z=18"; Steam Supply X=14 1/16"; Steam Supply Y=1 7/8"; Steam Supply Z=9 1/16"; Steam flow lb/h 40F to 140F @15psi=720; Supply Pipe Conn Y=1 7/8"; U Tube Extension=8 15/16"; U Tube Radius=3 3/8"; Unit Height=69"; Unit Radius=18 1/8"; Weight=1180
- 900 L 400A-QS: Assembly Code=D3040400; Cold Water Extension=23 5/8"; Cold Water NPT=2"; Cold Water Radius=1"; Control Panel Extension=29 5/8"; Drain Extension=26 1/2"; Drain NPT=1"; Drain Radius=1/2"; Enclosure Location=23"; Energy Extension=27 1/8"; Flat Side Distance=45 1/4"; Front Skid Extension=68 5/8"; Height to Cold Inlet=17 1/16"; Height to Drain=1 3/4"; Height to Energy=28 3/4"; Height to Hot Outlet=68 1/2"; Height to Relief=69 1/8"; Hot Outlet Angle=90.00°; Hot Water Extension=23 5/8"; Hot Water NPT=2"; Hot Water Radius=1"; Large Visibility=No; Rear Skid Extension=22 5/8"; Recovery Rate 40F to 140F @15psi=900 gph; Relief Extension=25 5/8"; Skid Center Dist=13 1/2"; Skid Length=46"; Skid Spacing=27"; Small Visibility=Yes; Steam Return NPT=1"; Steam Return Radius=1/2"; Steam Return Y=2 9/16"; Steam Supply Conn Y=1 7/8"; Steam Supply NPT=2"; Steam Supply Radius=1"; Steam Supply Total Z=18"; Steam Supply X=14 1/16"; Steam Supply Y=1 7/8"; Steam Supply Z=9 1/16"; Steam flow lb/h 40F to 140F @15psi=780; Supply Pipe Conn Y=1 7/8"; U Tube Extension=8 15/16"; U Tube Radius=3 3/8"; Unit Height=85 1/2"; Unit Radius=22 5/8"; Weight=1365
- 830 L 400A-QSD: Assembly Code=D3040400; Cold Water Extension=23 5/8"; Cold Water NPT=2"; Cold Water Radius=1"; Control Panel Extension=29 5/8"; Drain Extension=26 1/2"; Drain NPT=1"; Drain Radius=1/2"; Enclosure Location=23"; Energy Extension=27 1/8"; Flat Side Distance=45 1/4"; Front Skid Extension=68 5/8"; Height to Cold Inlet=17 1/16"; Height to Drain=1 3/4"; Height to Energy=28 3/4"; Height to Hot Outlet=68 1/2"; Height to Relief=69 1/8"; Hot Outlet Angle=90.00°; Hot Water Extension=23 5/8"; Hot Water NPT=2"; Hot Water Radius=1"; Large Visibility=Yes; Rear Skid Extension=22 5/8"; Recovery Rate 40F to 140F @15psi=830 gph; Relief Extension=25 5/8"; Skid Center Dist=13 1/2"; Skid Length=46"; Skid Spacing=27"; Small Visibility=No; Steam Return NPT=1"; Steam Return Radius=1/2"; Steam Return Y=3 3/8"; Steam Supply Conn Y=2 1/4"; Steam Supply NPT=1 1/2"; Steam Supply Radius=3/4"; Steam Supply Total Z=18"; Steam Supply X=14 1/16"; Steam Supply Y=1 7/8"; Steam Supply Z=9 1/16"; Steam flow lb/h 40F to 140F @15psi=720; Supply Pipe Conn Y=4 1/8"; U Tube Extension=8 15/16"; U Tube Radius=4 5/16"; Unit Height=85 1/2"; Unit Radius=22 5/8"; Weight=1411
- 520 L 300A-QS: Assembly Code=D3040400; Cold Water Extension=23 5/8"; Cold Water NPT=2"; Cold Water Radius=1"; Control Panel Extension=29 5/8"; Drain Extension=26 1/2"; Drain NPT=1"; Drain Radius=1/2"; Enclosure Location=17"; Energy Extension=27 1/8"; Flat Side Distance=45 1/4"; Front Skid Extension=68 5/8"; Height to Cold Inlet=17 1/16"; Height to Drain=1 3/4"; Height to Energy=28 3/4"; Height to Hot Outlet=50 7/8"; Height to Relief=57 1/8"; Hot Outlet Angle=0.00°; Hot Water Extension=23 5/8"; Hot Water NPT=2"; Hot Water Radius=1"; Large Visibility=No; Rear Skid Extension=22 5/8"; Recovery Rate 40F to 140F @15psi=520 gph; Relief Extension=25 5/8"; Skid Center Dist=13 1/2"; Skid Length=46"; Skid Spacing=27"; Small Visibility=Yes; Steam Return NPT=3/4"; Steam Return Radius=3/8"; Steam Return Y=1 11/16"; Steam Supply Conn Y=1 5/16"; Steam Supply NPT=1 1/2"; Steam Supply Radius=3/4"; Steam Supply Total Z=15 5/16"; Steam Supply X=12 11/16"; Steam Supply Y=1 5/16"; Steam Supply Z=7 1/8"; Steam flow lb/h 40F to 140F @15psi=450; Supply Pipe Conn Y=1 5/16"; U Tube Extension=8 3/16"; U Tube Radius=2 1/4"; Unit Height=73 1/2"; Unit Radius=22 5/8"; Weight=1250
- 520 L 250A-QS: Assembly Code=D3040400; Cold Water Extension=23 5/8"; Cold Water NPT=2"; Cold Water Radius=1"; Control Panel Extension=29 5/8"; Drain Extension=26 1/2"; Drain NPT=1"; Drain Radius=1/2"; Enclosure Location=15 1/2"; Energy Extension=27 1/8"; Flat Side Distance=45 1/4"; Front Skid Extension=68 5/8"; Height to Cold Inlet=17 1/16"; Height to Drain=1 3/4"; Height to Energy=28 3/4"; Height to Hot Outlet=38 7/8"; Height to Relief=45 1/8"; Hot Outlet Angle=0.00°; Hot Water Extension=23 5/8"; Hot Water NPT=2"; Hot Water Radius=1"; Large Visibility=No; Rear Skid Extension=22 5/8"; Recovery Rate 40F to 140F @15psi=520 gph; Relief Extension=25 5/8"; Skid Center Dist=13 1/2"; Skid Length=46"; Skid Spacing=27"; Small Visibility=Yes; Steam Return NPT=3/4"; Steam Return Radius=3/8"; Steam Return Y=1 11/16"; Steam Supply Conn Y=1 5/16"; Steam Supply NPT=1 1/2"; Steam Supply Radius=3/4"; Steam Supply Total Z=15 5/16"; Steam Supply X=12 11/16"; Steam Supply Y=1 5/16"; Steam Supply Z=7 1/8"; Steam flow lb/h 40F to 140F @15psi=450; Supply Pipe Conn Y=1 5/16"; U Tube Extension=8 3/16"; U Tube Radius=2 1/4"; Unit Height=61 1/2"; Unit Radius=22 5/8"; Weight=1190
- 440 L 300A-QSD: Assembly Code=D3040400; Cold Water Extension=23 5/8"; Cold Water NPT=2"; Cold Water Radius=1"; Control Panel Extension=29 5/8"; Drain Extension=26 1/2"; Drain NPT=1"; Drain Radius=1/2"; Enclosure Location=17"; Energy Extension=27 1/8"; Flat Side Distance=45 1/4"; Front Skid Extension=68 5/8"; Height to Cold Inlet=17 1/16"; Height to Drain=1 3/4"; Height to Energy=28 3/4"; Height to Hot Outlet=50 7/8"; Height to Relief=57 1/8"; Hot Outlet Angle=0.00°; Hot Water Extension=23 5/8"; Hot Water NPT=2"; Hot Water Radius=1"; Large Visibility=No; Rear Skid Extension=22 5/8"; Recovery Rate 40F to 140F @15psi=440 gph; Relief Extension=25 5/8"; Skid Center Dist=13 1/2"; Skid Length=46"; Skid Spacing=27"; Small Visibility=Yes; Steam Return NPT=3/4"; Steam Return Radius=3/8"; Steam Return Y=1 11/16"; Steam Supply Conn Y=1 5/16"; Steam Supply NPT=1"; Steam Supply Radius=1/2"; Steam Supply Total Z=15 5/16"; Steam Supply X=12 11/16"; Steam Supply Y=1 5/16"; Steam Supply Z=7 1/8"; Steam flow lb/h 40F to 140F @15psi=380; Supply Pipe Conn Y=1 5/16"; U Tube Extension=8 3/16"; U Tube Radius=2 1/4"; Unit Height=73 1/2"; Unit Radius=22 5/8"; Weight=1250
- 440 L 250A-QSD: Assembly Code=D3040400; Cold Water Extension=23 5/8"; Cold Water NPT=2"; Cold Water Radius=1"; Control Panel Extension=29 5/8"; Drain Extension=26 1/2"; Drain NPT=1"; Drain Radius=1/2"; Enclosure Location=15 1/2"; Energy Extension=27 1/8"; Flat Side Distance=45 1/4"; Front Skid Extension=68 5/8"; Height to Cold Inlet=17 1/16"; Height to Drain=1 3/4"; Height to Energy=28 3/4"; Height to Hot Outlet=38 7/8"; Height to Relief=45 1/8"; Hot Outlet Angle=0.00°; Hot Water Extension=23 5/8"; Hot Water NPT=2"; Hot Water Radius=1"; Large Visibility=No; Rear Skid Extension=22 5/8"; Recovery Rate 40F to 140F @15psi=440 gph; Relief Extension=25 5/8"; Skid Center Dist=13 1/2"; Skid Length=46"; Skid Spacing=27"; Small Visibility=Yes; Steam Return NPT=3/4"; Steam Return Radius=3/8"; Steam Return Y=1 11/16"; Steam Supply Conn Y=1 5/16"; Steam Supply NPT=1"; Steam Supply Radius=1/2"; Steam Supply Total Z=15 5/16"; Steam Supply X=12 11/16"; Steam Supply Y=1 5/16"; Steam Supply Z=7 1/8"; Steam flow lb/h 40F to 140F @15psi=380; Supply Pipe Conn Y=1 5/16"; U Tube Extension=8 3/16"; U Tube Radius=2 1/4"; Unit Height=61 1/2"; Unit Radius=22 5/8"; Weight=1190
- 520 L 400A-QS: Assembly Code=D3040400; Cold Water Extension=23 5/8"; Cold Water NPT=2"; Cold Water Radius=1"; Control Panel Extension=29 5/8"; Drain Extension=26 1/2"; Drain NPT=1"; Drain Radius=1/2"; Enclosure Location=23"; Energy Extension=27 1/8"; Flat Side Distance=45 1/4"; Front Skid Extension=68 5/8"; Height to Cold Inlet=17 1/16"; Height to Drain=1 3/4"; Height to Energy=28 3/4"; Height to Hot Outlet=68 1/2"; Height to Relief=69 1/8"; Hot Outlet Angle=90.00°; Hot Water Extension=23 5/8"; Hot Water NPT=2"; Hot Water Radius=1"; Large Visibility=No; Rear Skid Extension=22 5/8"; Recovery Rate 40F to 140F @15psi=520 gph; Relief Extension=25 5/8"; Skid Center Dist=13 1/2"; Skid Length=46"; Skid Spacing=27"; Small Visibility=Yes; Steam Return NPT=3/4"; Steam Return Radius=3/8"; Steam Return Y=1 11/16"; Steam Supply Conn Y=1 5/16"; Steam Supply NPT=1 1/2"; Steam Supply Radius=3/4"; Steam Supply Total Z=15 5/16"; Steam Supply X=12 11/16"; Steam Supply Y=1 5/16"; Steam Supply Z=7 1/8"; Steam flow lb/h 40F to 140F @15psi=450; Supply Pipe Conn Y=1 5/16"; U Tube Extension=8 3/16"; U Tube Radius=2 1/4"; Unit Height=85 1/2"; Unit Radius=22 5/8"; Weight=1265
- 3790 L 300A-QSD: Assembly Code=D3040400; Cold Water Extension=23 5/8"; Cold Water NPT=2"; Cold Water Radius=1"; Control Panel Extension=29 5/8"; Drain Extension=26 1/2"; Drain NPT=1"; Drain Radius=1/2"; Enclosure Location=17"; Energy Extension=27 1/8"; Flat Side Distance=45 1/4"; Front Skid Extension=68 5/8"; Height to Cold Inlet=17 1/16"; Height to Drain=1 3/4"; Height to Energy=28 3/4"; Height to Hot Outlet=50 7/8"; Height to Relief=57 1/8"; Hot Outlet Angle=0.00°; Hot Water Extension=23 5/8"; Hot Water NPT=2"; Hot Water Radius=1"; Large Visibility=Yes; Rear Skid Extension=22 5/8"; Recovery Rate 40F to 140F @15psi=3790 gph; Relief Extension=25 5/8"; Skid Center Dist=13 1/2"; Skid Length=46"; Skid Spacing=27"; Small Visibility=No; Steam Return NPT=2"; Steam Return Radius=1"; Steam Return Y=4 5/8"; Steam Supply Conn Y=3 13/16"; Steam Supply NPT=2 1/2"; Steam Supply Radius=1 1/4"; Steam Supply Total Z=18 15/16"; Steam Supply X=25 1/2"; Steam Supply Y=8 9/16"; Steam Supply Z=10 13/16"; Steam flow lb/h 40F to 140F @15psi=3300; Supply Pipe Conn Y=12 3/8"; U Tube Extension=8 1/8"; U Tube Radius=6 3/8"; Unit Height=73 1/2"; Unit Radius=22 5/8"; Weight=1750
- 3790 L 250A-QSD: Assembly Code=D3040400; Cold Water Extension=23 5/8"; Cold Water NPT=2"; Cold Water Radius=1"; Control Panel Extension=29 5/8"; Drain Extension=26 1/2"; Drain NPT=1"; Drain Radius=1/2"; Enclosure Location=15 1/2"; Energy Extension=27 1/8"; Flat Side Distance=45 1/4"; Front Skid Extension=68 5/8"; Height to Cold Inlet=17 1/16"; Height to Drain=1 3/4"; Height to Energy=28 3/4"; Height to Hot Outlet=38 7/8"; Height to Relief=45 1/8"; Hot Outlet Angle=0.00°; Hot Water Extension=23 5/8"; Hot Water NPT=2"; Hot Water Radius=1"; Large Visibility=Yes; Rear Skid Extension=22 5/8"; Recovery Rate 40F to 140F @15psi=3790 gph; Relief Extension=25 5/8"; Skid Center Dist=13 1/2"; Skid Length=46"; Skid Spacing=27"; Small Visibility=No; Steam Return NPT=2"; Steam Return Radius=1"; Steam Return Y=4 5/8"; Steam Supply Conn Y=3 13/16"; Steam Supply NPT=2 1/2"; Steam Supply Radius=1 1/4"; Steam Supply Total Z=18 15/16"; Steam Supply X=25 1/2"; Steam Supply Y=8 9/16"; Steam Supply Z=10 13/16"; Steam flow lb/h 40F to 140F @15psi=3300; Supply Pipe Conn Y=12 3/8"; U Tube Extension=8 1/8"; U Tube Radius=6 3/8"; Unit Height=61 1/2"; Unit Radius=22 5/8"; Weight=1590
- 3790 L 300A-QS: Assembly Code=D3040400; Cold Water Extension=23 5/8"; Cold Water NPT=2"; Cold Water Radius=1"; Control Panel Extension=29 5/8"; Drain Extension=26 1/2"; Drain NPT=1"; Drain Radius=1/2"; Enclosure Location=17"; Energy Extension=38 1/8"; Flat Side Distance=45 1/4"; Front Skid Extension=77 5/8"; Height to Cold Inlet=17 1/16"; Height to Drain=1 3/4"; Height to Energy=28 3/4"; Height to Hot Outlet=50 7/8"; Height to Relief=57 1/8"; Hot Outlet Angle=0.00°; Hot Water Extension=23 5/8"; Hot Water NPT=2"; Hot Water Radius=1"; Large Visibility=Yes; Rear Skid Extension=22 5/8"; Recovery Rate 40F to 140F @15psi=3790 gph; Relief Extension=25 5/8"; Skid Center Dist=13 1/2"; Skid Length=55"; Skid Spacing=27"; Small Visibility=No; Steam Return NPT=2"; Steam Return Radius=1"; Steam Return Y=4 5/8"; Steam Supply Conn Y=3 13/16"; Steam Supply NPT=2 1/2"; Steam Supply Radius=1 1/4"; Steam Supply Total Z=18 15/16"; Steam Supply X=25 1/2"; Steam Supply Y=8 9/16"; Steam Supply Z=10 13/16"; Steam flow lb/h 40F to 140F @15psi=3300; Supply Pipe Conn Y=12 3/8"; U Tube Extension=8 1/8"; U Tube Radius=6 3/8"; Unit Height=73 1/2"; Unit Radius=22 5/8"; Weight=1500
- 3790 L 250A-QS: Assembly Code=D3040400; Cold Water Extension=23 5/8"; Cold Water NPT=2"; Cold Water Radius=1"; Control Panel Extension=29 5/8"; Drain Extension=26 1/2"; Drain NPT=1"; Drain Radius=1/2"; Enclosure Location=15 1/2"; Energy Extension=38 1/8"; Flat Side Distance=45 1/4"; Front Skid Extension=77 5/8"; Height to Cold Inlet=17 1/16"; Height to Drain=1 3/4"; Height to Energy=28 3/4"; Height to Hot Outlet=38 7/8"; Height to Relief=45 1/8"; Hot Outlet Angle=0.00°; Hot Water Extension=23 5/8"; Hot Water NPT=2"; Hot Water Radius=1"; Large Visibility=Yes; Rear Skid Extension=22 5/8"; Recovery Rate 40F to 140F @15psi=3790 gph; Relief Extension=25 5/8"; Skid Center Dist=13 1/2"; Skid Length=55"; Skid Spacing=27"; Small Visibility=No; Steam Return NPT=2"; Steam Return Radius=1"; Steam Return Y=4 5/8"; Steam Supply Conn Y=3 13/16"; Steam Supply NPT=2 1/2"; Steam Supply Radius=1 1/4"; Steam Supply Total Z=18 15/16"; Steam Supply X=25 1/2"; Steam Supply Y=8 9/16"; Steam Supply Z=10 13/16"; Steam flow lb/h 40F to 140F @15psi=3300; Supply Pipe Conn Y=12 3/8"; U Tube Extension=8 1/8"; U Tube Radius=6 3/8"; Unit Height=61 1/2"; Unit Radius=22 5/8"; Weight=1440
- 380 L 300A-QS: Assembly Code=D3040400; Cold Water Extension=23 5/8"; Cold Water NPT=2"; Cold Water Radius=1"; Control Panel Extension=29 5/8"; Drain Extension=26 1/2"; Drain NPT=1"; Drain Radius=1/2"; Enclosure Location=17"; Energy Extension=27 1/8"; Flat Side Distance=45 1/4"; Front Skid Extension=68 5/8"; Height to Cold Inlet=17 1/16"; Height to Drain=1 3/4"; Height to Energy=28 3/4"; Height to Hot Outlet=50 7/8"; Height to Relief=57 1/8"; Hot Outlet Angle=0.00°; Hot Water Extension=23 5/8"; Hot Water NPT=2"; Hot Water Radius=1"; Large Visibility=No; Rear Skid Extension=22 5/8"; Recovery Rate 40F to 140F @15psi=380 gph; Relief Extension=25 5/8"; Skid Center Dist=13 1/2"; Skid Length=46"; Skid Spacing=27"; Small Visibility=Yes; Steam Return NPT=3/4"; Steam Return Radius=3/8"; Steam Return Y=1 11/16"; Steam Supply Conn Y=1 5/16"; Steam Supply NPT=1"; Steam Supply Radius=1/2"; Steam Supply Total Z=15 5/16"; Steam Supply X=12 11/16"; Steam Supply Y=1 5/16"; Steam Supply Z=7 1/8"; Steam flow lb/h 40F to 140F @15psi=330; Supply Pipe Conn Y=1 5/16"; U Tube Extension=8 3/16"; U Tube Radius=2 1/4"; Unit Height=73 1/2"; Unit Radius=22 5/8"; Weight=1100
- 380 L 250A-QS: Assembly Code=D3040400; Cold Water Extension=23 5/8"; Cold Water NPT=2"; Cold Water Radius=1"; Control Panel Extension=29 5/8"; Drain Extension=26 1/2"; Drain NPT=1"; Drain Radius=1/2"; Enclosure Location=15 1/2"; Energy Extension=27 1/8"; Flat Side Distance=45 1/4"; Front Skid Extension=68 5/8"; Height to Cold Inlet=17 1/16"; Height to Drain=1 3/4"; Height to Energy=28 3/4"; Height to Hot Outlet=38 7/8"; Height to Relief=45 1/8"; Hot Outlet Angle=0.00°; Hot Water Extension=23 5/8"; Hot Water NPT=2"; Hot Water Radius=1"; Large Visibility=No; Rear Skid Extension=22 5/8"; Recovery Rate 40F to 140F @15psi=380 gph; Relief Extension=25 5/8"; Skid Center Dist=13 1/2"; Skid Length=46"; Skid Spacing=27"; Small Visibility=Yes; Steam Return NPT=3/4"; Steam Return Radius=3/8"; Steam Return Y=1 11/16"; Steam Supply Conn Y=1 5/16"; Steam Supply NPT=1"; Steam Supply Radius=1/2"; Steam Supply Total Z=15 5/16"; Steam Supply X=12 11/16"; Steam Supply Y=1 5/16"; Steam Supply Z=7 1/8"; Steam flow lb/h 40F to 140F @15psi=330; Supply Pipe Conn Y=1 5/16"; U Tube Extension=8 3/16"; U Tube Radius=2 1/4"; Unit Height=61 1/2"; Unit Radius=22 5/8"; Weight=1040
- 440 L 400A-QSD: Assembly Code=D3040400; Cold Water Extension=23 5/8"; Cold Water NPT=2"; Cold Water Radius=1"; Control Panel Extension=29 5/8"; Drain Extension=26 1/2"; Drain NPT=1"; Drain Radius=1/2"; Enclosure Location=23"; Energy Extension=27 1/8"; Flat Side Distance=45 1/4"; Front Skid Extension=68 5/8"; Height to Cold Inlet=17 1/16"; Height to Drain=1 3/4"; Height to Energy=28 3/4"; Height to Hot Outlet=68 1/2"; Height to Relief=69 1/8"; Hot Outlet Angle=90.00°; Hot Water Extension=23 5/8"; Hot Water NPT=2"; Hot Water Radius=1"; Large Visibility=No; Rear Skid Extension=22 5/8"; Recovery Rate 40F to 140F @15psi=440 gph; Relief Extension=25 5/8"; Skid Center Dist=13 1/2"; Skid Length=46"; Skid Spacing=27"; Small Visibility=Yes; Steam Return NPT=3/4"; Steam Return Radius=3/8"; Steam Return Y=1 11/16"; Steam Supply Conn Y=1 5/16"; Steam Supply NPT=1"; Steam Supply Radius=1/2"; Steam Supply Total Z=15 5/16"; Steam Supply X=12 11/16"; Steam Supply Y=1 5/16"; Steam Supply Z=7 1/8"; Steam flow lb/h 40F to 140F @15psi=380; Supply Pipe Conn Y=1 5/16"; U Tube Extension=8 3/16"; U Tube Radius=2 1/4"; Unit Height=85 1/2"; Unit Radius=22 5/8"; Weight=1315
- 330 L 300A-QSD: Assembly Code=D3040400; Cold Water Extension=23 5/8"; Cold Water NPT=2"; Cold Water Radius=1"; Control Panel Extension=29 5/8"; Drain Extension=26 1/2"; Drain NPT=1"; Drain Radius=1/2"; Enclosure Location=17"; Energy Extension=27 1/8"; Flat Side Distance=45 1/4"; Front Skid Extension=68 5/8"; Height to Cold Inlet=17 1/16"; Height to Drain=1 3/4"; Height to Energy=28 3/4"; Height to Hot Outlet=50 7/8"; Height to Relief=57 1/8"; Hot Outlet Angle=0.00°; Hot Water Extension=23 5/8"; Hot Water NPT=2"; Hot Water Radius=1"; Large Visibility=No; Rear Skid Extension=22 5/8"; Recovery Rate 40F to 140F @15psi=330 gph; Relief Extension=25 5/8"; Skid Center Dist=13 1/2"; Skid Length=46"; Skid Spacing=27"; Small Visibility=Yes; Steam Return NPT=3/4"; Steam Return Radius=3/8"; Steam Return Y=1 11/16"; Steam Supply Conn Y=1 5/16"; Steam Supply NPT=1"; Steam Supply Radius=1/2"; Steam Supply Total Z=15 5/16"; Steam Supply X=12 11/16"; Steam Supply Y=1 5/16"; Steam Supply Z=7 1/8"; Steam flow lb/h 40F to 140F @15psi=280; Supply Pipe Conn Y=1 5/16"; U Tube Extension=8 3/16"; U Tube Radius=2 1/4"; Unit Height=73 1/2"; Unit Radius=22 5/8"; Weight=1100
- 330 L 250A-QSD: Assembly Code=D3040400; Cold Water Extension=23 5/8"; Cold Water NPT=2"; Cold Water Radius=1"; Control Panel Extension=29 5/8"; Drain Extension=26 1/2"; Drain NPT=1"; Drain Radius=1/2"; Enclosure Location=15 1/2"; Energy Extension=27 1/8"; Flat Side Distance=45 1/4"; Front Skid Extension=68 5/8"; Height to Cold Inlet=17 1/16"; Height to Drain=1 3/4"; Height to Energy=28 3/4"; Height to Hot Outlet=38 7/8"; Height to Relief=45 1/8"; Hot Outlet Angle=0.00°; Hot Water Extension=23 5/8"; Hot Water NPT=2"; Hot Water Radius=1"; Large Visibility=No; Rear Skid Extension=22 5/8"; Recovery Rate 40F to 140F @15psi=330 gph; Relief Extension=25 5/8"; Skid Center Dist=13 1/2"; Skid Length=46"; Skid Spacing=27"; Small Visibility=Yes; Steam Return NPT=3/4"; Steam Return Radius=3/8"; Steam Return Y=1 11/16"; Steam Supply Conn Y=1 5/16"; Steam Supply NPT=1"; Steam Supply Radius=1/2"; Steam Supply Total Z=15 5/16"; Steam Supply X=12 11/16"; Steam Supply Y=1 5/16"; Steam Supply Z=7 1/8"; Steam flow lb/h 40F to 140F @15psi=280; Supply Pipe Conn Y=1 5/16"; U Tube Extension=8 3/16"; U Tube Radius=2 1/4"; Unit Height=61 1/2"; Unit Radius=22 5/8"; Weight=1040
- 380 L 400A-QS: Assembly Code=D3040400; Cold Water Extension=23 5/8"; Cold Water NPT=2"; Cold Water Radius=1"; Control Panel Extension=29 5/8"; Drain Extension=26 1/2"; Drain NPT=1"; Drain Radius=1/2"; Enclosure Location=23"; Energy Extension=27 1/8"; Flat Side Distance=45 1/4"; Front Skid Extension=68 5/8"; Height to Cold Inlet=17 1/16"; Height to Drain=1 3/4"; Height to Energy=28 3/4"; Height to Hot Outlet=68 1/2"; Height to Relief=69 1/8"; Hot Outlet Angle=90.00°; Hot Water Extension=23 5/8"; Hot Water NPT=2"; Hot Water Radius=1"; Large Visibility=No; Rear Skid Extension=22 5/8"; Recovery Rate 40F to 140F @15psi=380 gph; Relief Extension=25 5/8"; Skid Center Dist=13 1/2"; Skid Length=46"; Skid Spacing=27"; Small Visibility=Yes; Steam Return NPT=3/4"; Steam Return Radius=3/8"; Steam Return Y=1 11/16"; Steam Supply Conn Y=1 5/16"; Steam Supply NPT=1"; Steam Supply Radius=1/2"; Steam Supply Total Z=15 5/16"; Steam Supply X=12 11/16"; Steam Supply Y=1 5/16"; Steam Supply Z=7 1/8"; Steam flow lb/h 40F to 140F @15psi=330; Supply Pipe Conn Y=1 5/16"; U Tube Extension=8 3/16"; U Tube Radius=2 1/4"; Unit Height=85 1/2"; Unit Radius=22 5/8"; Weight=1165
- 3790 L 400A-QSD: Assembly Code=D3040400; Cold Water Extension=23 5/8"; Cold Water NPT=2"; Cold Water Radius=1"; Control Panel Extension=29 5/8"; Drain Extension=26 1/2"; Drain NPT=1"; Drain Radius=1/2"; Enclosure Location=23"; Energy Extension=27 1/8"; Flat Side Distance=45 1/4"; Front Skid Extension=77 5/8"; Height to Cold Inlet=17 1/16"; Height to Drain=1 3/4"; Height to Energy=28 3/4"; Height to Hot Outlet=68 1/2"; Height to Relief=69 1/8"; Hot Outlet Angle=90.00°; Hot Water Extension=23 5/8"; Hot Water NPT=2"; Hot Water Radius=1"; Large Visibility=Yes; Rear Skid Extension=22 5/8"; Recovery Rate 40F to 140F @15psi=3790 gph; Relief Extension=25 5/8"; Skid Center Dist=13 1/2"; Skid Length=55"; Skid Spacing=27"; Small Visibility=No; Steam Return NPT=2"; Steam Return Radius=1"; Steam Return Y=5 1/16"; Steam Supply Conn Y=3 11/16"; Steam Supply NPT=2 1/2"; Steam Supply Radius=1 1/4"; Steam Supply Total Z=18 15/16"; Steam Supply X=25 1/2"; Steam Supply Y=8 9/16"; Steam Supply Z=10 13/16"; Steam flow lb/h 40F to 140F @15psi=3300; Supply Pipe Conn Y=12 1/4"; U Tube Extension=8 1/8"; U Tube Radius=6 3/8"; Unit Height=85 1/2"; Unit Radius=22 5/8"; Weight=1677
- 3790 L 400A-QS: Assembly Code=D3040400; Cold Water Extension=23 5/8"; Cold Water NPT=2"; Cold Water Radius=1"; Control Panel Extension=29 5/8"; Drain Extension=26 1/2"; Drain NPT=1"; Drain Radius=1/2"; Enclosure Location=23"; Energy Extension=38 1/8"; Flat Side Distance=45 1/4"; Front Skid Extension=77 5/8"; Height to Cold Inlet=17 1/16"; Height to Drain=1 3/4"; Height to Energy=28 3/4"; Height to Hot Outlet=68 1/2"; Height to Relief=69 1/8"; Hot Outlet Angle=90.00°; Hot Water Extension=23 5/8"; Hot Water NPT=2"; Hot Water Radius=1"; Large Visibility=Yes; Rear Skid Extension=22 5/8"; Recovery Rate 40F to 140F @15psi=3790 gph; Relief Extension=25 5/8"; Skid Center Dist=13 1/2"; Skid Length=55"; Skid Spacing=27"; Small Visibility=No; Steam Return NPT=2"; Steam Return Radius=1"; Steam Return Y=5 1/16"; Steam Supply Conn Y=3 11/16"; Steam Supply NPT=2 1/2"; Steam Supply Radius=1 1/4"; Steam Supply Total Z=18 15/16"; Steam Supply X=25 1/2"; Steam Supply Y=8 9/16"; Steam Supply Z=10 13/16"; Steam flow lb/h 40F to 140F @15psi=3300; Supply Pipe Conn Y=12 1/4"; U Tube Extension=8 1/8"; U Tube Radius=6 3/8"; Unit Height=85 1/2"; Unit Radius=22 5/8"; Weight=1427
- 2650 L 300A-QSD: Assembly Code=D3040400; Cold Water Extension=23 5/8"; Cold Water NPT=2"; Cold Water Radius=1"; Control Panel Extension=29 5/8"; Drain Extension=26 1/2"; Drain NPT=1"; Drain Radius=1/2"; Enclosure Location=17"; Energy Extension=27 1/8"; Flat Side Distance=45 1/4"; Front Skid Extension=68 5/8"; Height to Cold Inlet=17 1/16"; Height to Drain=1 3/4"; Height to Energy=28 3/4"; Height to Hot Outlet=50 7/8"; Height to Relief=57 1/8"; Hot Outlet Angle=0.00°; Hot Water Extension=23 5/8"; Hot Water NPT=2"; Hot Water Radius=1"; Large Visibility=Yes; Rear Skid Extension=22 5/8"; Recovery Rate 40F to 140F @15psi=2650 gph; Relief Extension=25 5/8"; Skid Center Dist=13 1/2"; Skid Length=46"; Skid Spacing=27"; Small Visibility=No; Steam Return NPT=2"; Steam Return Radius=1"; Steam Return Y=4 1/16"; Steam Supply Conn Y=2 11/16"; Steam Supply NPT=2 1/2"; Steam Supply Radius=1 1/4"; Steam Supply Total Z=19 3/4"; Steam Supply X=25 1/2"; Steam Supply Y=8 9/16"; Steam Supply Z=10 13/16"; Steam flow lb/h 40F to 140F @15psi=2300; Supply Pipe Conn Y=11 1/4"; U Tube Extension=8 15/16"; U Tube Radius=5 3/8"; Unit Height=73 1/2"; Unit Radius=22 5/8"; Weight=1550
- 2650 L 250A-QSD: Assembly Code=D3040400; Cold Water Extension=23 5/8"; Cold Water NPT=2"; Cold Water Radius=1"; Control Panel Extension=29 5/8"; Drain Extension=26 1/2"; Drain NPT=1"; Drain Radius=1/2"; Enclosure Location=15 1/2"; Energy Extension=27 1/8"; Flat Side Distance=45 1/4"; Front Skid Extension=68 5/8"; Height to Cold Inlet=17 1/16"; Height to Drain=1 3/4"; Height to Energy=28 3/4"; Height to Hot Outlet=38 7/8"; Height to Relief=45 1/8"; Hot Outlet Angle=0.00°; Hot Water Extension=23 5/8"; Hot Water NPT=2"; Hot Water Radius=1"; Large Visibility=Yes; Rear Skid Extension=22 5/8"; Recovery Rate 40F to 140F @15psi=2650 gph; Relief Extension=25 5/8"; Skid Center Dist=13 1/2"; Skid Length=46"; Skid Spacing=27"; Small Visibility=No; Steam Return NPT=2"; Steam Return Radius=1"; Steam Return Y=4 1/16"; Steam Supply Conn Y=2 11/16"; Steam Supply NPT=2 1/2"; Steam Supply Radius=1 1/4"; Steam Supply Total Z=19 3/4"; Steam Supply X=25 1/2"; Steam Supply Y=8 9/16"; Steam Supply Z=10 13/16"; Steam flow lb/h 40F to 140F @15psi=2300; Supply Pipe Conn Y=11 1/4"; U Tube Extension=8 15/16"; U Tube Radius=5 3/8"; Unit Height=61 1/2"; Unit Radius=22 5/8"; Weight=1390
- 330 L 400A-QSD: Assembly Code=D3040400; Cold Water Extension=23 5/8"; Cold Water NPT=2"; Cold Water Radius=1"; Control Panel Extension=29 5/8"; Drain Extension=26 1/2"; Drain NPT=1"; Drain Radius=1/2"; Enclosure Location=23"; Energy Extension=27 1/8"; Flat Side Distance=45 1/4"; Front Skid Extension=68 5/8"; Height to Cold Inlet=17 1/16"; Height to Drain=1 3/4"; Height to Energy=28 3/4"; Height to Hot Outlet=68 1/2"; Height to Relief=69 1/8"; Hot Outlet Angle=90.00°; Hot Water Extension=23 5/8"; Hot Water NPT=2"; Hot Water Radius=1"; Large Visibility=No; Rear Skid Extension=22 5/8"; Recovery Rate 40F to 140F @15psi=330 gph; Relief Extension=25 5/8"; Skid Center Dist=13 1/2"; Skid Length=46"; Skid Spacing=27"; Small Visibility=Yes; Steam Return NPT=3/4"; Steam Return Radius=3/8"; Steam Return Y=1 11/16"; Steam Supply Conn Y=1 5/16"; Steam Supply NPT=1"; Steam Supply Radius=1/2"; Steam Supply Total Z=15 5/16"; Steam Supply X=12 11/16"; Steam Supply Y=1 5/16"; Steam Supply Z=7 1/8"; Steam flow lb/h 40F to 140F @15psi=280; Supply Pipe Conn Y=1 5/16"; U Tube Extension=8 3/16"; U Tube Radius=2 1/4"; Unit Height=85 1/2"; Unit Radius=22 5/8"; Weight=1165
- 2280 L 300A-QS: Assembly Code=D3040400; Cold Water Extension=23 5/8"; Cold Water NPT=2"; Cold Water Radius=1"; Control Panel Extension=29 5/8"; Drain Extension=26 1/2"; Drain NPT=1"; Drain Radius=1/2"; Enclosure Location=17"; Energy Extension=38 1/8"; Flat Side Distance=45 1/4"; Front Skid Extension=77 5/8"; Height to Cold Inlet=17 1/16"; Height to Drain=1 3/4"; Height to Energy=28 3/4"; Height to Hot Outlet=50 7/8"; Height to Relief=57 1/8"; Hot Outlet Angle=0.00°; Hot Water Extension=23 5/8"; Hot Water NPT=2"; Hot Water Radius=1"; Large Visibility=Yes; Rear Skid Extension=22 5/8"; Recovery Rate 40F to 140F @15psi=2280 gph; Relief Extension=25 5/8"; Skid Center Dist=13 1/2"; Skid Length=55"; Skid Spacing=27"; Small Visibility=No; Steam Return NPT=1 1/4"; Steam Return Radius=5/8"; Steam Return Y=3 3/8"; Steam Supply Conn Y=2 1/4"; Steam Supply NPT=2 1/2"; Steam Supply Radius=1 1/4"; Steam Supply Total Z=19 3/4"; Steam Supply X=25 1/2"; Steam Supply Y=8 9/16"; Steam Supply Z=10 13/16"; Steam flow lb/h 40F to 140F @15psi=1980; Supply Pipe Conn Y=10 13/16"; U Tube Extension=8 15/16"; U Tube Radius=4 5/16"; Unit Height=73 1/2"; Unit Radius=22 5/8"; Weight=1400
- 2280 L 250A-QS: Assembly Code=D3040400; Cold Water Extension=23 5/8"; Cold Water NPT=2"; Cold Water Radius=1"; Control Panel Extension=29 5/8"; Drain Extension=26 1/2"; Drain NPT=1"; Drain Radius=1/2"; Enclosure Location=15 1/2"; Energy Extension=38 1/8"; Flat Side Distance=45 1/4"; Front Skid Extension=77 5/8"; Height to Cold Inlet=17 1/16"; Height to Drain=1 3/4"; Height to Energy=28 3/4"; Height to Hot Outlet=38 7/8"; Height to Relief=45 1/8"; Hot Outlet Angle=0.00°; Hot Water Extension=23 5/8"; Hot Water NPT=2"; Hot Water Radius=1"; Large Visibility=Yes; Rear Skid Extension=22 5/8"; Recovery Rate 40F to 140F @15psi=2280 gph; Relief Extension=25 5/8"; Skid Center Dist=13 1/2"; Skid Length=55"; Skid Spacing=27"; Small Visibility=No; Steam Return NPT=1 1/4"; Steam Return Radius=5/8"; Steam Return Y=3 3/8"; Steam Supply Conn Y=2 1/4"; Steam Supply NPT=2 1/2"; Steam Supply Radius=1 1/4"; Steam Supply Total Z=19 3/4"; Steam Supply X=25 1/2"; Steam Supply Y=8 9/16"; Steam Supply Z=10 13/16"; Steam flow lb/h 40F to 140F @15psi=1980; Supply Pipe Conn Y=10 13/16"; U Tube Extension=8 15/16"; U Tube Radius=4 5/16"; Unit Height=61 1/2"; Unit Radius=22 5/8"; Weight=1340
- 2650 L 400A-QSD: Assembly Code=D3040400; Cold Water Extension=23 5/8"; Cold Water NPT=2"; Cold Water Radius=1"; Control Panel Extension=29 5/8"; Drain Extension=26 1/2"; Drain NPT=1"; Drain Radius=1/2"; Enclosure Location=23"; Energy Extension=27 1/8"; Flat Side Distance=45 1/4"; Front Skid Extension=68 5/8"; Height to Cold Inlet=17 1/16"; Height to Drain=1 3/4"; Height to Energy=28 3/4"; Height to Hot Outlet=68 1/2"; Height to Relief=69 1/8"; Hot Outlet Angle=90.00°; Hot Water Extension=23 5/8"; Hot Water NPT=2"; Hot Water Radius=1"; Large Visibility=Yes; Rear Skid Extension=22 5/8"; Recovery Rate 40F to 140F @15psi=2650 gph; Relief Extension=25 5/8"; Skid Center Dist=13 1/2"; Skid Length=46"; Skid Spacing=27"; Small Visibility=No; Steam Return NPT=2"; Steam Return Radius=1"; Steam Return Y=4 1/16"; Steam Supply Conn Y=2 13/16"; Steam Supply NPT=2 1/2"; Steam Supply Radius=1 1/4"; Steam Supply Total Z=19 3/4"; Steam Supply X=25 1/2"; Steam Supply Y=8 9/16"; Steam Supply Z=10 13/16"; Steam flow lb/h 40F to 140F @15psi=2300; Supply Pipe Conn Y=11 3/8"; U Tube Extension=8 15/16"; U Tube Radius=5 3/8"; Unit Height=85 1/2"; Unit Radius=22 5/8"; Weight=1587
- 1940 L 300A-QSD: Assembly Code=D3040400; Cold Water Extension=23 5/8"; Cold Water NPT=2"; Cold Water Radius=1"; Control Panel Extension=29 5/8"; Drain Extension=26 1/2"; Drain NPT=1"; Drain Radius=1/2"; Enclosure Location=17"; Energy Extension=38 1/8"; Flat Side Distance=45 1/4"; Front Skid Extension=68 5/8"; Height to Cold Inlet=17 1/16"; Height to Drain=1 3/4"; Height to Energy=28 3/4"; Height to Hot Outlet=50 7/8"; Height to Relief=57 1/8"; Hot Outlet Angle=0.00°; Hot Water Extension=23 5/8"; Hot Water NPT=2"; Hot Water Radius=1"; Large Visibility=No; Rear Skid Extension=22 5/8"; Recovery Rate 40F to 140F @15psi=1940 gph; Relief Extension=25 5/8"; Skid Center Dist=13 1/2"; Skid Length=46"; Skid Spacing=27"; Small Visibility=Yes; Steam Return NPT=1 1/4"; Steam Return Radius=5/8"; Steam Return Y=3 3/8"; Steam Supply Conn Y=2 1/4"; Steam Supply NPT=2 1/2"; Steam Supply Radius=1 1/4"; Steam Supply Total Z=17 1/8"; Steam Supply X=17 3/16"; Steam Supply Y=2 1/4"; Steam Supply Z=8 3/16"; Steam flow lb/h 40F to 140F @15psi=1680; Supply Pipe Conn Y=2 1/4"; U Tube Extension=8 15/16"; U Tube Radius=4 5/16"; Unit Height=73 1/2"; Unit Radius=22 5/8"; Weight=1450
- 1940 L 250A-QSD: Assembly Code=D3040400; Cold Water Extension=23 5/8"; Cold Water NPT=2"; Cold Water Radius=1"; Control Panel Extension=29 5/8"; Drain Extension=26 1/2"; Drain NPT=1"; Drain Radius=1/2"; Enclosure Location=15 1/2"; Energy Extension=38 1/8"; Flat Side Distance=45 1/4"; Front Skid Extension=68 5/8"; Height to Cold Inlet=17 1/16"; Height to Drain=1 3/4"; Height to Energy=28 3/4"; Height to Hot Outlet=38 7/8"; Height to Relief=45 1/8"; Hot Outlet Angle=0.00°; Hot Water Extension=23 5/8"; Hot Water NPT=2"; Hot Water Radius=1"; Large Visibility=No; Rear Skid Extension=22 5/8"; Recovery Rate 40F to 140F @15psi=1940 gph; Relief Extension=25 5/8"; Skid Center Dist=13 1/2"; Skid Length=46"; Skid Spacing=27"; Small Visibility=Yes; Steam Return NPT=1 1/4"; Steam Return Radius=5/8"; Steam Return Y=3 3/8"; Steam Supply Conn Y=2 1/4"; Steam Supply NPT=2 1/2"; Steam Supply Radius=1 1/4"; Steam Supply Total Z=17 1/8"; Steam Supply X=17 3/16"; Steam Supply Y=2 1/4"; Steam Supply Z=8 3/16"; Steam flow lb/h 40F to 140F @15psi=1680; Supply Pipe Conn Y=2 1/4"; U Tube Extension=8 15/16"; U Tube Radius=4 5/16"; Unit Height=61 1/2"; Unit Radius=22 5/8"; Weight=1390
- 1780 L 300A-QS: Assembly Code=D3040400; Cold Water Extension=23 5/8"; Cold Water NPT=2"; Cold Water Radius=1"; Control Panel Extension=29 5/8"; Drain Extension=26 1/2"; Drain NPT=1"; Drain Radius=1/2"; Enclosure Location=17"; Energy Extension=27 1/8"; Flat Side Distance=45 1/4"; Front Skid Extension=68 5/8"; Height to Cold Inlet=17 1/16"; Height to Drain=1 3/4"; Height to Energy=28 3/4"; Height to Hot Outlet=50 7/8"; Height to Relief=57 1/8"; Hot Outlet Angle=0.00°; Hot Water Extension=23 5/8"; Hot Water NPT=2"; Hot Water Radius=1"; Large Visibility=Yes; Rear Skid Extension=22 5/8"; Recovery Rate 40F to 140F @15psi=1780 gph; Relief Extension=25 5/8"; Skid Center Dist=13 1/2"; Skid Length=46"; Skid Spacing=27"; Small Visibility=No; Steam Return NPT=1 1/4"; Steam Return Radius=5/8"; Steam Return Y=3 3/8"; Steam Supply Conn Y=2 1/4"; Steam Supply NPT=2 1/2"; Steam Supply Radius=1 1/4"; Steam Supply Total Z=19 3/4"; Steam Supply X=25 1/2"; Steam Supply Y=8 9/16"; Steam Supply Z=10 13/16"; Steam flow lb/h 40F to 140F @15psi=1540; Supply Pipe Conn Y=10 13/16"; U Tube Extension=8 15/16"; U Tube Radius=4 5/16"; Unit Height=73 1/2"; Unit Radius=22 5/8"; Weight=1350
- 1780 L 250A-QS: Assembly Code=D3040400; Cold Water Extension=23 5/8"; Cold Water NPT=2"; Cold Water Radius=1"; Control Panel Extension=29 5/8"; Drain Extension=26 1/2"; Drain NPT=1"; Drain Radius=1/2"; Enclosure Location=15 1/2"; Energy Extension=27 1/8"; Flat Side Distance=45 1/4"; Front Skid Extension=68 5/8"; Height to Cold Inlet=17 1/16"; Height to Drain=1 3/4"; Height to Energy=28 3/4"; Height to Hot Outlet=38 7/8"; Height to Relief=45 1/8"; Hot Outlet Angle=0.00°; Hot Water Extension=23 5/8"; Hot Water NPT=2"; Hot Water Radius=1"; Large Visibility=Yes; Rear Skid Extension=22 5/8"; Recovery Rate 40F to 140F @15psi=1780 gph; Relief Extension=25 5/8"; Skid Center Dist=13 1/2"; Skid Length=46"; Skid Spacing=27"; Small Visibility=No; Steam Return NPT=1 1/4"; Steam Return Radius=5/8"; Steam Return Y=3 3/8"; Steam Supply Conn Y=2 1/4"; Steam Supply NPT=2 1/2"; Steam Supply Radius=1 1/4"; Steam Supply Total Z=19 3/4"; Steam Supply X=25 1/2"; Steam Supply Y=8 9/16"; Steam Supply Z=10 13/16"; Steam flow lb/h 40F to 140F @15psi=1540; Supply Pipe Conn Y=10 13/16"; U Tube Extension=8 15/16"; U Tube Radius=4 5/16"; Unit Height=61 1/2"; Unit Radius=22 5/8"; Weight=1290
- 2280 L 400A-QS: Assembly Code=D3040400; Cold Water Extension=23 5/8"; Cold Water NPT=2"; Cold Water Radius=1"; Control Panel Extension=29 5/8"; Drain Extension=26 1/2"; Drain NPT=1"; Drain Radius=1/2"; Enclosure Location=23"; Energy Extension=38 1/8"; Flat Side Distance=45 1/4"; Front Skid Extension=77 5/8"; Height to Cold Inlet=17 1/16"; Height to Drain=1 3/4"; Height to Energy=28 3/4"; Height to Hot Outlet=68 1/2"; Height to Relief=69 1/8"; Hot Outlet Angle=90.00°; Hot Water Extension=23 5/8"; Hot Water NPT=2"; Hot Water Radius=1"; Large Visibility=Yes; Rear Skid Extension=22 5/8"; Recovery Rate 40F to 140F @15psi=2280 gph; Relief Extension=25 5/8"; Skid Center Dist=13 1/2"; Skid Length=55"; Skid Spacing=27"; Small Visibility=No; Steam Return NPT=1 1/4"; Steam Return Radius=5/8"; Steam Return Y=3 3/8"; Steam Supply Conn Y=2 1/4"; Steam Supply NPT=2 1/2"; Steam Supply Radius=1 1/4"; Steam Supply Total Z=19 3/4"; Steam Supply X=25 1/2"; Steam Supply Y=8 9/16"; Steam Supply Z=10 13/16"; Steam flow lb/h 40F to 140F @15psi=1980; Supply Pipe Conn Y=10 13/16"; U Tube Extension=8 15/16"; U Tube Radius=4 5/16"; Unit Height=85 1/2"; Unit Radius=22 5/8"; Weight=1415
- 1520 L 300A-QSD: Assembly Code=D3040400; Cold Water Extension=23 5/8"; Cold Water NPT=2"; Cold Water Radius=1"; Control Panel Extension=29 5/8"; Drain Extension=26 1/2"; Drain NPT=1"; Drain Radius=1/2"; Enclosure Location=17"; Energy Extension=27 1/8"; Flat Side Distance=45 1/4"; Front Skid Extension=68 5/8"; Height to Cold Inlet=17 1/16"; Height to Drain=1 3/4"; Height to Energy=28 3/4"; Height to Hot Outlet=50 7/8"; Height to Relief=57 1/8"; Hot Outlet Angle=0.00°; Hot Water Extension=23 5/8"; Hot Water NPT=2"; Hot Water Radius=1"; Large Visibility=No; Rear Skid Extension=22 5/8"; Recovery Rate 40F to 140F @15psi=1520 gph; Relief Extension=25 5/8"; Skid Center Dist=13 1/2"; Skid Length=46"; Skid Spacing=27"; Small Visibility=Yes; Steam Return NPT=1 1/4"; Steam Return Radius=5/8"; Steam Return Y=3 3/8"; Steam Supply Conn Y=2 1/4"; Steam Supply NPT=2"; Steam Supply Radius=1"; Steam Supply Total Z=17 1/8"; Steam Supply X=17 3/16"; Steam Supply Y=2 1/4"; Steam Supply Z=8 3/16"; Steam flow lb/h 40F to 140F @15psi=1320; Supply Pipe Conn Y=2 1/4"; U Tube Extension=8 15/16"; U Tube Radius=4 5/16"; Unit Height=73 1/2"; Unit Radius=22 5/8"; Weight=1450
- 1520 L 250A-QSD: Assembly Code=D3040400e; Cold Water Extension=23 5/8"; Cold Water NPT=2"; Cold Water Radius=1"; Control Panel Extension=29 5/8"; Drain Extension=26 1/2"; Drain NPT=1"; Drain Radius=1/2"; Enclosure Location=15 1/2"; Energy Extension=27 1/8"; Flat Side Distance=45 1/4"; Front Skid Extension=68 5/8"; Height to Cold Inlet=17 1/16"; Height to Drain=1 3/4"; Height to Energy=28 3/4"; Height to Hot Outlet=38 7/8"; Height to Relief=45 1/8"; Hot Outlet Angle=0.00°; Hot Water Extension=23 5/8"; Hot Water NPT=2"; Hot Water Radius=1"; Large Visibility=No; Rear Skid Extension=22 5/8"; Recovery Rate 40F to 140F @15psi=1520 gph; Relief Extension=25 5/8"; Skid Center Dist=13 1/2"; Skid Length=46"; Skid Spacing=27"; Small Visibility=Yes; Steam Return NPT=1 1/4"; Steam Return Radius=5/8"; Steam Return Y=3 3/8"; Steam Supply Conn Y=2 1/4"; Steam Supply NPT=2"; Steam Supply Radius=1"; Steam Supply Total Z=17 1/8"; Steam Supply X=17 3/16"; Steam Supply Y=2 1/4"; Steam Supply Z=8 3/16"; Steam flow lb/h 40F to 140F @15psi=1320; Supply Pipe Conn Y=2 1/4"; U Tube Extension=8 15/16"; U Tube Radius=4 5/16"; Unit Height=61 1/2"; Unit Radius=22 5/8"; Weight=1290
- 1940 L 400A-QSD: Assembly Code=D3040400; Cold Water Extension=23 5/8"; Cold Water NPT=2"; Cold Water Radius=1"; Control Panel Extension=29 5/8"; Drain Extension=26 1/2"; Drain NPT=1"; Drain Radius=1/2"; Enclosure Location=23"; Energy Extension=38 1/8"; Flat Side Distance=45 1/4"; Front Skid Extension=68 5/8"; Height to Cold Inlet=17 1/16"; Height to Drain=1 3/4"; Height to Energy=28 3/4"; Height to Hot Outlet=68 1/2"; Height to Relief=69 1/8"; Hot Outlet Angle=90.00°; Hot Water Extension=23 5/8"; Hot Water NPT=2"; Hot Water Radius=1"; Large Visibility=Yes; Rear Skid Extension=22 5/8"; Recovery Rate 40F to 140F @15psi=1940 gph; Relief Extension=25 5/8"; Skid Center Dist=13 1/2"; Skid Length=46"; Skid Spacing=27"; Small Visibility=No; Steam Return NPT=1 1/4"; Steam Return Radius=5/8"; Steam Return Y=4 1/16"; Steam Supply Conn Y=2 13/16"; Steam Supply NPT=2 1/2"; Steam Supply Radius=1 1/4"; Steam Supply Total Z=17 1/8"; Steam Supply X=17 3/16"; Steam Supply Y=2 1/4"; Steam Supply Z=8 3/16"; Steam flow lb/h 40F to 140F @15psi=1680; Supply Pipe Conn Y=5 1/16"; U Tube Extension=8 15/16"; U Tube Radius=5 3/8"; Unit Height=85 1/2"; Unit Radius=22 5/8"; Weight=1597
- 1780 L 400A-QS: Assembly Code=D3040400; Cold Water Extension=23 5/8"; Cold Water NPT=2"; Cold Water Radius=1"; Control Panel Extension=29 5/8"; Drain Extension=26 1/2"; Drain NPT=1"; Drain Radius=1/2"; Enclosure Location=23"; Energy Extension=27 1/8"; Flat Side Distance=45 1/4"; Front Skid Extension=68 5/8"; Height to Cold Inlet=17 1/16"; Height to Drain=1 3/4"; Height to Energy=28 3/4"; Height to Hot Outlet=68 1/2"; Height to Relief=69 1/8"; Hot Outlet Angle=90.00°; Hot Water Extension=23 5/8"; Hot Water NPT=2"; Hot Water Radius=1"; Large Visibility=Yes; Rear Skid Extension=22 5/8"; Recovery Rate 40F to 140F @15psi=1780 gph; Relief Extension=25 5/8"; Skid Center Dist=13 1/2"; Skid Length=46"; Skid Spacing=27"; Small Visibility=No; Steam Return NPT=1 1/4"; Steam Return Radius=5/8"; Steam Return Y=3 3/8"; Steam Supply Conn Y=2 1/4"; Steam Supply NPT=2 1/2"; Steam Supply Radius=1 1/4"; Steam Supply Total Z=19 3/4"; Steam Supply X=25 1/2"; Steam Supply Y=8 9/16"; Steam Supply Z=10 13/16"; Steam flow lb/h 40F to 140F @15psi=1540; Supply Pipe Conn Y=10 13/16"; U Tube Extension=8 15/16"; U Tube Radius=4 5/16"; Unit Height=85 1/2"; Unit Radius=22 5/8"; Weight=1415
- 1230 L 300A-QS: Assembly Code=D3040400; Cold Water Extension=23 5/8"; Cold Water NPT=2"; Cold Water Radius=1"; Control Panel Extension=29 5/8"; Drain Extension=26 1/2"; Drain NPT=1"; Drain Radius=1/2"; Enclosure Location=17"; Energy Extension=38 1/8"; Flat Side Distance=45 1/4"; Front Skid Extension=77 5/8"; Height to Cold Inlet=17 1/16"; Height to Drain=1 3/4"; Height to Energy=28 3/4"; Height to Hot Outlet=50 7/8"; Height to Relief=57 1/8"; Hot Outlet Angle=0.00°; Hot Water Extension=23 5/8"; Hot Water NPT=2"; Hot Water Radius=1"; Large Visibility=Yes; Rear Skid Extension=22 5/8"; Recovery Rate 40F to 140F @15psi=1230 gph; Relief Extension=25 5/8"; Skid Center Dist=13 1/2"; Skid Length=55"; Skid Spacing=27"; Small Visibility=No; Steam Return NPT=1"; Steam Return Radius=1/2"; Steam Return Y=2 9/16"; Steam Supply Conn Y=1 7/8"; Steam Supply NPT=2"; Steam Supply Radius=1"; Steam Supply Total Z=17 1/8"; Steam Supply X=17 3/16"; Steam Supply Y=2 1/4"; Steam Supply Z=8 3/16"; Steam flow lb/h 40F to 140F @15psi=1070; Supply Pipe Conn Y=4 1/8"; U Tube Extension=8 15/16"; U Tube Radius=3 3/8"; Unit Height=73 1/2"; Unit Radius=22 5/8"; Weight=1300
- 1230 L 250A-QS: Assembly Code=D3040400; Cold Water Extension=23 5/8"; Cold Water NPT=2"; Cold Water Radius=1"; Control Panel Extension=29 5/8"; Drain Extension=26 1/2"; Drain NPT=1"; Drain Radius=1/2"; Enclosure Location=15 1/2"; Energy Extension=38 1/8"; Flat Side Distance=45 1/4"; Front Skid Extension=77 5/8"; Height to Cold Inlet=17 1/16"; Height to Drain=1 3/4"; Height to Energy=28 3/4"; Height to Hot Outlet=38 7/8"; Height to Relief=45 1/8"; Hot Outlet Angle=0.00°; Hot Water Extension=23 5/8"; Hot Water NPT=2"; Hot Water Radius=1"; Large Visibility=Yes; Rear Skid Extension=22 5/8"; Recovery Rate 40F to 140F @15psi=1230 gph; Relief Extension=25 5/8"; Skid Center Dist=13 1/2"; Skid Length=55"; Skid Spacing=27"; Small Visibility=No; Steam Return NPT=1"; Steam Return Radius=1/2"; Steam Return Y=2 9/16"; Steam Supply Conn Y=1 7/8"; Steam Supply NPT=2"; Steam Supply Radius=1"; Steam Supply Total Z=17 1/8"; Steam Supply X=17 3/16"; Steam Supply Y=2 1/4"; Steam Supply Z=8 3/16"; Steam flow lb/h 40F to 140F @15psi=1070; Supply Pipe Conn Y=4 1/8"; U Tube Extension=8 15/16"; U Tube Radius=3 3/8"; Unit Height=61 1/2"; Unit Radius=22 5/8"; Weight=1240
- 1520 L 400A-QSD: Assembly Code=D3040400; Cold Water Extension=23 5/8"; Cold Water NPT=2"; Cold Water Radius=1"; Control Panel Extension=29 5/8"; Drain Extension=26 1/2"; Drain NPT=1"; Drain Radius=1/2"; Enclosure Location=23"; Energy Extension=27 1/8"; Flat Side Distance=45 1/4"; Front Skid Extension=68 5/8"; Height to Cold Inlet=17 1/16"; Height to Drain=1 3/4"; Height to Energy=28 3/4"; Height to Hot Outlet=68 1/2"; Height to Relief=69 1/8"; Hot Outlet Angle=90.00°; Hot Water Extension=23 5/8"; Hot Water NPT=2"; Hot Water Radius=1"; Large Visibility=No; Rear Skid Extension=22 5/8"; Recovery Rate 40F to 140F @15psi=1520 gph; Relief Extension=25 5/8"; Skid Center Dist=13 1/2"; Skid Length=46"; Skid Spacing=27"; Small Visibility=Yes; Steam Return NPT=1 1/4"; Steam Return Radius=5/8"; Steam Return Y=3 3/8"; Steam Supply Conn Y=2 1/4"; Steam Supply NPT=2"; Steam Supply Radius=1"; Steam Supply Total Z=17 1/8"; Steam Supply X=17 3/16"; Steam Supply Y=2 1/4"; Steam Supply Z=8 3/16"; Steam flow lb/h 40F to 140F @15psi=1320; Supply Pipe Conn Y=2 1/4"; U Tube Extension=8 15/16"; U Tube Radius=4 5/16"; Unit Height=85 1/2"; Unit Radius=22 5/8"; Weight=1431
- 1230 L 400A-QS: Assembly Code=D3040400; Cold Water Extension=23 5/8"; Cold Water NPT=2"; Cold Water Radius=1"; Control Panel Extension=29 5/8"; Drain Extension=26 1/2"; Drain NPT=1"; Drain Radius=1/2"; Enclosure Location=23"; Energy Extension=38 1/8"; Flat Side Distance=45 1/4"; Front Skid Extension=77 5/8"; Height to Cold Inlet=17 1/16"; Height to Drain=1 3/4"; Height to Energy=28 3/4"; Height to Hot Outlet=68 1/2"; Height to Relief=69 1/8"; Hot Outlet Angle=90.00°; Hot Water Extension=23 5/8"; Hot Water NPT=2"; Hot Water Radius=1"; Large Visibility=Yes; Rear Skid Extension=22 5/8"; Recovery Rate 40F to 140F @15psi=1230 gph; Relief Extension=25 5/8"; Skid Center Dist=13 1/2"; Skid Length=55"; Skid Spacing=27"; Small Visibility=No; Steam Return NPT=1"; Steam Return Radius=1/2"; Steam Return Y=2 9/16"; Steam Supply Conn Y=1 7/8"; Steam Supply NPT=2"; Steam Supply Radius=1"; Steam Supply Total Z=17 1/8"; Steam Supply X=17 3/16"; Steam Supply Y=2 1/4"; Steam Supply Z=8 3/16"; Steam flow lb/h 40F to 140F @15psi=1070; Supply Pipe Conn Y=4 1/8"; U Tube Extension=8 15/16"; U Tube Radius=3 3/8"; Unit Height=85 1/2"; Unit Radius=22 5/8"; Weight=1365
- 900 L 300A-QS: Assembly Code=D3040400; Cold Water Extension=23 5/8"; Cold Water NPT=2"; Cold Water Radius=1"; Control Panel Extension=29 5/8"; Drain Extension=26 1/2"; Drain NPT=1"; Drain Radius=1/2"; Enclosure Location=17"; Energy Extension=27 1/8"; Flat Side Distance=45 1/4"; Front Skid Extension=68 5/8"; Height to Cold Inlet=17 1/16"; Height to Drain=1 3/4"; Height to Energy=28 3/4"; Height to Hot Outlet=50 7/8"; Height to Relief=57 1/8"; Hot Outlet Angle=0.00°; Hot Water Extension=23 5/8"; Hot Water NPT=2"; Hot Water Radius=1"; Large Visibility=No; Rear Skid Extension=22 5/8"; Recovery Rate 40F to 140F @15psi=900 gph; Relief Extension=25 5/8"; Skid Center Dist=13 1/2"; Skid Length=46"; Skid Spacing=27"; Small Visibility=Yes; Steam Return NPT=1"; Steam Return Radius=1/2"; Steam Return Y=2 9/16"; Steam Supply Conn Y=1 7/8"; Steam Supply NPT=2"; Steam Supply Radius=1"; Steam Supply Total Z=18"; Steam Supply X=14 1/16"; Steam Supply Y=1 7/8"; Steam Supply Z=9 1/16"; Steam flow lb/h 40F to 140F @15psi=780; Supply Pipe Conn Y=1 7/8"; U Tube Extension=8 15/16"; U Tube Radius=3 3/8"; Unit Height=73 1/2"; Unit Radius=22 5/8"; Weight=1300
- 900 L 250A-QS: Assembly Code=D3040400; Cold Water Extension=23 5/8"; Cold Water NPT=2"; Cold Water Radius=1"; Control Panel Extension=29 5/8"; Drain Extension=26 1/2"; Drain NPT=1"; Drain Radius=1/2"; Enclosure Location=15 1/2"; Energy Extension=27 1/8"; Flat Side Distance=45 1/4"; Front Skid Extension=68 5/8"; Height to Cold Inlet=17 1/16"; Height to Drain=1 3/4"; Height to Energy=28 3/4"; Height to Hot Outlet=38 7/8"; Height to Relief=45 1/8"; Hot Outlet Angle=0.00°; Hot Water Extension=23 5/8"; Hot Water NPT=2"; Hot Water Radius=1"; Large Visibility=No; Rear Skid Extension=22 5/8"; Recovery Rate 40F to 140F @15psi=900 gph; Relief Extension=25 5/8"; Skid Center Dist=13 1/2"; Skid Length=46"; Skid Spacing=27"; Small Visibility=Yes; Steam Return NPT=1"; Steam Return Radius=1/2"; Steam Return Y=2 9/16"; Steam Supply Conn Y=1 7/8"; Steam Supply NPT=2"; Steam Supply Radius=1"; Steam Supply Total Z=18"; Steam Supply X=14 1/16"; Steam Supply Y=1 7/8"; Steam Supply Z=9 1/16"; Steam flow lb/h 40F to 140F @15psi=780; Supply Pipe Conn Y=1 7/8"; U Tube Extension=8 15/16"; U Tube Radius=3 3/8"; Unit Height=61 1/2"; Unit Radius=22 5/8"; Weight=1240
- 830 L 300A-QSD: Assembly Code=D3040400; Cold Water Extension=23 5/8"; Cold Water NPT=2"; Cold Water Radius=1"; Control Panel Extension=29 5/8"; Drain Extension=26 1/2"; Drain NPT=1"; Drain Radius=1/2"; Enclosure Location=17"; Energy Extension=27 1/8"; Flat Side Distance=45 1/4"; Front Skid Extension=68 5/8"; Height to Cold Inlet=17 1/16"; Height to Drain=1 3/4"; Height to Energy=28 3/4"; Height to Hot Outlet=50 7/8"; Height to Relief=57 1/8"; Hot Outlet Angle=0.00°; Hot Water Extension=23 5/8"; Hot Water NPT=2"; Hot Water Radius=1"; Large Visibility=No; Rear Skid Extension=22 5/8"; Recovery Rate 40F to 140F @15psi=830 gph; Relief Extension=25 5/8"; Skid Center Dist=13 1/2"; Skid Length=46"; Skid Spacing=27"; Small Visibility=Yes; Steam Return NPT=1"; Steam Return Radius=1/2"; Steam Return Y=2 9/16"; Steam Supply Conn Y=1 7/8"; Steam Supply NPT=1 1/2"; Steam Supply Radius=3/4"; Steam Supply Total Z=18"; Steam Supply X=14 1/16"; Steam Supply Y=1 7/8"; Steam Supply Z=9 1/16"; Steam flow lb/h 40F to 140F @15psi=720; Supply Pipe Conn Y=1 7/8"; U Tube Extension=8 15/16"; U Tube Radius=3 3/8"; Unit Height=73 1/2"; Unit Radius=22 5/8"; Weight=1350
- 830 L 250A-QSD: Assembly Code=D3040400; Cold Water Extension=23 5/8"; Cold Water NPT=2"; Cold Water Radius=1"; Control Panel Extension=29 5/8"; Drain Extension=26 1/2"; Drain NPT=1"; Drain Radius=1/2"; Enclosure Location=15 1/2"; Energy Extension=27 1/8"; Flat Side Distance=45 1/4"; Front Skid Extension=68 5/8"; Height to Cold Inlet=17 1/16"; Height to Drain=1 3/4"; Height to Energy=28 3/4"; Height to Hot Outlet=38 7/8"; Height to Relief=45 1/8"; Hot Outlet Angle=0.00°; Hot Water Extension=23 5/8"; Hot Water NPT=2"; Hot Water Radius=1"; Large Visibility=No; Rear Skid Extension=22 5/8"; Recovery Rate 40F to 140F @15psi=830 gph; Relief Extension=25 5/8"; Skid Center Dist=13 1/2"; Skid Length=46"; Skid Spacing=27"; Small Visibility=Yes; Steam Return NPT=1"; Steam Return Radius=1/2"; Steam Return Y=2 9/16"; Steam Supply Conn Y=1 7/8"; Steam Supply NPT=1 1/2"; Steam Supply Radius=3/4"; Steam Supply Total Z=18"; Steam Supply X=14 1/16"; Steam Supply Y=1 7/8"; Steam Supply Z=9 1/16"; Steam flow lb/h 40F to 140F @15psi=720; Supply Pipe Conn Y=1 7/8"; U Tube Extension=8 15/16"; U Tube Radius=3 3/8"; Unit Height=61 1/2"; Unit Radius=22 5/8"; Weight=1240
- 520 L 600A-QS: Assembly Code=D3040400; Cold Water Extension=28 7/8"; Cold Water NPT=3"; Cold Water Radius=1 1/2"; Control Panel Extension=34 7/8"; Drain Extension=31 3/4"; Drain NPT=1 1/2"; Drain Radius=3/4"; Enclosure Location=23"; Energy Extension=32 5/8"; Flat Side Distance=55 3/4"; Front Skid Extension=82 7/8"; Height to Cold Inlet=18 1/4"; Height to Drain=1 3/4"; Height to Energy=30"; Height to Hot Outlet=69 3/8"; Height to Relief=70"; Hot Outlet Angle=90.00°; Hot Water Extension=28 7/8"; Hot Water NPT=3"; Hot Water Radius=1 1/2"; Large Visibility=No; Rear Skid Extension=27 7/8"; Recovery Rate 40F to 140F @15psi=520 gph; Relief Extension=30 7/8"; Skid Center Dist=13 1/2"; Skid Length=55"; Skid Spacing=27"; Small Visibility=Yes; Steam Return NPT=3/4"; Steam Return Radius=3/8"; Steam Return Y=1 11/16"; Steam Supply Conn Y=1 5/16"; Steam Supply NPT=1 1/2"; Steam Supply Radius=3/4"; Steam Supply Total Z=15 5/16"; Steam Supply X=12 11/16"; Steam Supply Y=1 5/16"; Steam Supply Z=7 1/8"; Steam flow lb/h 40F to 140F @15psi=450; Supply Pipe Conn Y=1 5/16"; U Tube Extension=8 3/16"; U Tube Radius=2 1/4"; Unit Height=87 3/4"; Unit Radius=27 7/8"; Weight=1900
- 520 L 500A-QS: Assembly Code=D3040400; Cold Water Extension=28 7/8"; Cold Water NPT=3"; Cold Water Radius=1 1/2"; Control Panel Extension=34 7/8"; Drain Extension=31 3/4"; Drain NPT=1 1/2"; Drain Radius=3/4"; Enclosure Location=17"; Energy Extension=32 5/8"; Flat Side Distance=55 3/4"; Front Skid Extension=82 7/8"; Height to Cold Inlet=18 1/4"; Height to Drain=1 3/4"; Height to Energy=30"; Height to Hot Outlet=57 3/8"; Height to Relief=58"; Hot Outlet Angle=90.00°; Hot Water Extension=28 7/8"; Hot Water NPT=3"; Hot Water Radius=1 1/2"; Large Visibility=No; Rear Skid Extension=27 7/8"; Recovery Rate 40F to 140F @15psi=520 gph; Relief Extension=30 7/8"; Skid Center Dist=13 1/2"; Skid Length=55"; Skid Spacing=27"; Small Visibility=Yes; Steam Return NPT=3/4"; Steam Return Radius=3/8"; Steam Return Y=1 11/16"; Steam Supply Conn Y=1 5/16"; Steam Supply NPT=1 1/2"; Steam Supply Radius=3/4"; Steam Supply Total Z=15 5/16"; Steam Supply X=12 11/16"; Steam Supply Y=1 5/16"; Steam Supply Z=7 1/8"; Steam flow lb/h 40F to 140F @15psi=450; Supply Pipe Conn Y=1 5/16"; U Tube Extension=8 3/16"; U Tube Radius=2 1/4"; Unit Height=75 3/4"; Unit Radius=27 7/8"; Weight=1675
- 440 L 600A-QSD: Assembly Code=D3040400; Cold Water Extension=28 7/8"; Cold Water NPT=3"; Cold Water Radius=1 1/2"; Control Panel Extension=34 7/8"; Drain Extension=31 3/4"; Drain NPT=1 1/2"; Drain Radius=3/4"; Enclosure Location=23"; Energy Extension=32 5/8"; Flat Side Distance=55 3/4"; Front Skid Extension=82 7/8"; Height to Cold Inlet=18 1/4"; Height to Drain=1 3/4"; Height to Energy=30"; Height to Hot Outlet=69 3/8"; Height to Relief=70"; Hot Outlet Angle=90.00°; Hot Water Extension=28 7/8"; Hot Water NPT=3"; Hot Water Radius=1 1/2"; Large Visibility=No; Rear Skid Extension=27 7/8"; Recovery Rate 40F to 140F @15psi=440 gph; Relief Extension=30 7/8"; Skid Center Dist=13 1/2"; Skid Length=55"; Skid Spacing=27"; Small Visibility=Yes; Steam Return NPT=3/4"; Steam Return Radius=3/8"; Steam Return Y=1 11/16"; Steam Supply Conn Y=1 5/16"; Steam Supply NPT=1"; Steam Supply Radius=1/2"; Steam Supply Total Z=15 5/16"; Steam Supply X=12 11/16"; Steam Supply Y=1 5/16"; Steam Supply Z=7 1/8"; Steam flow lb/h 40F to 140F @15psi=380; Supply Pipe Conn Y=1 5/16"; U Tube Extension=8 3/16"; U Tube Radius=2 1/4"; Unit Height=87 3/4"; Unit Radius=27 7/8"; Weight=1900
- 440 L 500A-QSD: Assembly Code=D3040400; Cold Water Extension=28 7/8"; Cold Water NPT=3"; Cold Water Radius=1 1/2"; Control Panel Extension=34 7/8"; Drain Extension=31 3/4"; Drain NPT=1 1/2"; Drain Radius=3/4"; Enclosure Location=17"; Energy Extension=32 5/8"; Flat Side Distance=55 3/4"; Front Skid Extension=82 7/8"; Height to Cold Inlet=18 1/4"; Height to Drain=1 3/4"; Height to Energy=30"; Height to Hot Outlet=57 3/8"; Height to Relief=58"; Hot Outlet Angle=90.00°; Hot Water Extension=28 7/8"; Hot Water NPT=3"; Hot Water Radius=1 1/2"; Large Visibility=No; Rear Skid Extension=27 7/8"; Recovery Rate 40F to 140F @15psi=440 gph; Relief Extension=30 7/8"; Skid Center Dist=13 1/2"; Skid Length=55"; Skid Spacing=27"; Small Visibility=Yes; Steam Return NPT=3/4"; Steam Return Radius=3/8"; Steam Return Y=1 11/16"; Steam Supply Conn Y=1 5/16"; Steam Supply NPT=1"; Steam Supply Radius=1/2"; Steam Supply Total Z=15 5/16"; Steam Supply X=12 11/16"; Steam Supply Y=1 5/16"; Steam Supply Z=7 1/8"; Steam flow lb/h 40F to 140F @15psi=380; Supply Pipe Conn Y=1 5/16"; U Tube Extension=8 3/16"; U Tube Radius=2 1/4"; Unit Height=75 3/4"; Unit Radius=27 7/8"; Weight=1675
- 3790 L 600A-QSD: Assembly Code=D3040400; Cold Water Extension=28 7/8"; Cold Water NPT=3"; Cold Water Radius=1 1/2"; Control Panel Extension=34 7/8"; Drain Extension=31 3/4"; Drain NPT=1 1/2"; Drain Radius=3/4"; Enclosure Location=23"; Energy Extension=32 5/8"; Flat Side Distance=55 3/4"; Front Skid Extension=82 7/8"; Height to Cold Inlet=18 1/4"; Height to Drain=1 3/4"; Height to Energy=30"; Height to Hot Outlet=69 3/8"; Height to Relief=70"; Hot Outlet Angle=90.00°; Hot Water Extension=28 7/8"; Hot Water NPT=3"; Hot Water Radius=1 1/2"; Large Visibility=Yes; Rear Skid Extension=27 7/8"; Recovery Rate 40F to 140F @15psi=3790 gph; Relief Extension=30 7/8"; Skid Center Dist=13 1/2"; Skid Length=55"; Skid Spacing=27"; Small Visibility=No; Steam Return NPT=2"; Steam Return Radius=1"; Steam Return Y=4 5/8"; Steam Supply Conn Y=3 13/16"; Steam Supply NPT=2 1/2"; Steam Supply Radius=1 1/4"; Steam Supply Total Z=18 15/16"; Steam Supply X=25 1/2"; Steam Supply Y=8 9/16"; Steam Supply Z=10 13/16"; Steam flow lb/h 40F to 140F @15psi=3300; Supply Pipe Conn Y=12 3/8"; U Tube Extension=8 1/8"; U Tube Radius=6 3/8"; Unit Height=87 3/4"; Unit Radius=27 7/8"; Weight=2400
- 3790 L 500A-QSD: Assembly Code=D3040400; Cold Water Extension=28 7/8"; Cold Water NPT=3"; Cold Water Radius=1 1/2"; Control Panel Extension=34 7/8"; Drain Extension=31 3/4"; Drain NPT=1 1/2"; Drain Radius=3/4"; Enclosure Location=17"; Energy Extension=32 5/8"; Flat Side Distance=55 3/4"; Front Skid Extension=82 7/8"; Height to Cold Inlet=18 1/4"; Height to Drain=1 3/4"; Height to Energy=30"; Height to Hot Outlet=57 3/8"; Height to Relief=58"; Hot Outlet Angle=90.00°; Hot Water Extension=28 7/8"; Hot Water NPT=3"; Hot Water Radius=1 1/2"; Large Visibility=Yes; Rear Skid Extension=27 7/8"; Recovery Rate 40F to 140F @15psi=3790 gph; Relief Extension=30 7/8"; Skid Center Dist=13 1/2"; Skid Length=55"; Skid Spacing=27"; Small Visibility=No; Steam Return NPT=2"; Steam Return Radius=1"; Steam Return Y=4 5/8"; Steam Supply Conn Y=3 13/16"; Steam Supply NPT=2 1/2"; Steam Supply Radius=1 1/4"; Steam Supply Total Z=18 15/16"; Steam Supply X=25 1/2"; Steam Supply Y=8 9/16"; Steam Supply Z=10 13/16"; Steam flow lb/h 40F to 140F @15psi=3300; Supply Pipe Conn Y=12 3/8"; U Tube Extension=8 1/8"; U Tube Radius=6 3/8"; Unit Height=75 3/4"; Unit Radius=27 7/8"; Weight=2125
- 3790 L 600A-QS: Assembly Code=D3040400; Cold Water Extension=28 7/8"; Cold Water NPT=3"; Cold Water Radius=1 1/2"; Control Panel Extension=34 7/8"; Drain Extension=31 3/4"; Drain NPT=1 1/2"; Drain Radius=3/4"; Enclosure Location=23"; Energy Extension=32 5/8"; Flat Side Distance=55 3/4"; Front Skid Extension=82 7/8"; Height to Cold Inlet=18 1/4"; Height to Drain=1 3/4"; Height to Energy=30"; Height to Hot Outlet=69 3/8"; Height to Relief=70"; Hot Outlet Angle=90.00°; Hot Water Extension=28 7/8"; Hot Water NPT=3"; Hot Water Radius=1 1/2"; Large Visibility=Yes; Rear Skid Extension=27 7/8"; Recovery Rate 40F to 140F @15psi=3790 gph; Relief Extension=30 7/8"; Skid Center Dist=13 1/2"; Skid Length=55"; Skid Spacing=27"; Small Visibility=No; Steam Return NPT=2"; Steam Return Radius=1"; Steam Return Y=4 5/8"; Steam Supply Conn Y=3 13/16"; Steam Supply NPT=2 1/2"; Steam Supply Radius=1 1/4"; Steam Supply Total Z=18 15/16"; Steam Supply X=25 1/2"; Steam Supply Y=8 9/16"; Steam Supply Z=10 13/16"; Steam flow lb/h 40F to 140F @15psi=3300; Supply Pipe Conn Y=12 3/8"; U Tube Extension=8 1/8"; U Tube Radius=6 3/8"; Unit Height=87 3/4"; Unit Radius=27 7/8"; Weight=2150
- 3790 L 500A-QS: Assembly Code=D3040400; Cold Water Extension=28 7/8"; Cold Water NPT=3"; Cold Water Radius=1 1/2"; Control Panel Extension=34 7/8"; Drain Extension=31 3/4"; Drain NPT=1 1/2"; Drain Radius=3/4"; Enclosure Location=17"; Energy Extension=32 5/8"; Flat Side Distance=55 3/4"; Front Skid Extension=82 7/8"; Height to Cold Inlet=18 1/4"; Height to Drain=1 3/4"; Height to Energy=30"; Height to Hot Outlet=57 3/8"; Height to Relief=58"; Hot Outlet Angle=90.00°; Hot Water Extension=28 7/8"; Hot Water NPT=3"; Hot Water Radius=1 1/2"; Large Visibility=Yes; Rear Skid Extension=27 7/8"; Recovery Rate 40F to 140F @15psi=3790 gph; Relief Extension=30 7/8"; Skid Center Dist=13 1/2"; Skid Length=55"; Skid Spacing=27"; Small Visibility=No; Steam Return NPT=2"; Steam Return Radius=1"; Steam Return Y=4 5/8"; Steam Supply Conn Y=3 13/16"; Steam Supply NPT=2 1/2"; Steam Supply Radius=1 1/4"; Steam Supply Total Z=18 15/16"; Steam Supply X=25 1/2"; Steam Supply Y=8 9/16"; Steam Supply Z=10 13/16"; Steam flow lb/h 40F to 140F @15psi=3300; Supply Pipe Conn Y=12 3/8"; U Tube Extension=8 1/8"; U Tube Radius=6 3/8"; Unit Height=75 3/4"; Unit Radius=27 7/8"; Weight=1925
- 380 L 600A-QS: Assembly Code=D3040400; Cold Water Extension=28 7/8"; Cold Water NPT=3"; Cold Water Radius=1 1/2"; Control Panel Extension=34 7/8"; Drain Extension=31 3/4"; Drain NPT=1 1/2"; Drain Radius=3/4"; Enclosure Location=23"; Energy Extension=32 5/8"; Flat Side Distance=55 3/4"; Front Skid Extension=82 7/8"; Height to Cold Inlet=18 1/4"; Height to Drain=1 3/4"; Height to Energy=30"; Height to Hot Outlet=69 3/8"; Height to Relief=70"; Hot Outlet Angle=90.00°; Hot Water Extension=28 7/8"; Hot Water NPT=3"; Hot Water Radius=1 1/2"; Large Visibility=No; Rear Skid Extension=27 7/8"; Recovery Rate 40F to 140F @15psi=380 gph; Relief Extension=30 7/8"; Skid Center Dist=13 1/2"; Skid Length=55"; Skid Spacing=27"; Small Visibility=Yes; Steam Return NPT=3/4"; Steam Return Radius=3/8"; Steam Return Y=1 11/16"; Steam Supply Conn Y=1 5/16"; Steam Supply NPT=1"; Steam Supply Radius=1/2"; Steam Supply Total Z=15 5/16"; Steam Supply X=12 11/16"; Steam Supply Y=1 5/16"; Steam Supply Z=7 1/8"; Steam flow lb/h 40F to 140F @15psi=330; Supply Pipe Conn Y=1 5/16"; U Tube Extension=8 3/16"; U Tube Radius=2 1/4"; Unit Height=87 3/4"; Unit Radius=27 7/8"; Weight=1750
- 380 L 500A-QS: Assembly Code=D3040400; Cold Water Extension=28 7/8"; Cold Water NPT=3"; Cold Water Radius=1 1/2"; Control Panel Extension=34 7/8"; Drain Extension=31 3/4"; Drain NPT=1 1/2"; Drain Radius=3/4"; Enclosure Location=17"; Energy Extension=32 5/8"; Flat Side Distance=55 3/4"; Front Skid Extension=82 7/8"; Height to Cold Inlet=18 1/4"; Height to Drain=1 3/4"; Height to Energy=30"; Height to Hot Outlet=57 3/8"; Height to Relief=58"; Hot Outlet Angle=90.00°; Hot Water Extension=28 7/8"; Hot Water NPT=3"; Hot Water Radius=1 1/2"; Large Visibility=No; Rear Skid Extension=27 7/8"; Recovery Rate 40F to 140F @15psi=380 gph; Relief Extension=30 7/8"; Skid Center Dist=13 1/2"; Skid Length=55"; Skid Spacing=27"; Small Visibility=Yes; Steam Return NPT=3/4"; Steam Return Radius=3/8"; Steam Return Y=1 11/16"; Steam Supply Conn Y=1 5/16"; Steam Supply NPT=1"; Steam Supply Radius=1/2"; Steam Supply Total Z=15 5/16"; Steam Supply X=12 11/16"; Steam Supply Y=1 5/16"; Steam Supply Z=7 1/8"; Steam flow lb/h 40F to 140F @15psi=330; Supply Pipe Conn Y=1 5/16"; U Tube Extension=8 3/16"; U Tube Radius=2 1/4"; Unit Height=75 3/4"; Unit Radius=27 7/8"; Weight=1525
- 330 L 600A-QSD: Assembly Code=D3040400; Cold Water Extension=28 7/8"; Cold Water NPT=3"; Cold Water Radius=1 1/2"; Control Panel Extension=34 7/8"; Drain Extension=31 3/4"; Drain NPT=1 1/2"; Drain Radius=3/4"; Enclosure Location=23"; Energy Extension=32 5/8"; Flat Side Distance=55 3/4"; Front Skid Extension=82 7/8"; Height to Cold Inlet=18 1/4"; Height to Drain=1 3/4"; Height to Energy=30"; Height to Hot Outlet=69 3/8"; Height to Relief=70"; Hot Outlet Angle=90.00°; Hot Water Extension=28 7/8"; Hot Water NPT=3"; Hot Water Radius=1 1/2"; Large Visibility=No; Rear Skid Extension=27 7/8"; Recovery Rate 40F to 140F @15psi=330 gph; Relief Extension=30 7/8"; Skid Center Dist=13 1/2"; Skid Length=55"; Skid Spacing=27"; Small Visibility=Yes; Steam Return NPT=3/4"; Steam Return Radius=3/8"; Steam Return Y=1 11/16"; Steam Supply Conn Y=1 5/16"; Steam Supply NPT=1"; Steam Supply Radius=1/2"; Steam Supply Total Z=15 5/16"; Steam Supply X=12 11/16"; Steam Supply Y=1 5/16"; Steam Supply Z=7 1/8"; Steam flow lb/h 40F to 140F @15psi=280; Supply Pipe Conn Y=1 5/16"; U Tube Extension=8 3/16"; U Tube Radius=2 1/4"; Unit Height=87 3/4"; Unit Radius=27 7/8"; Weight=1750
- 330 L 500A-QSD: Assembly Code=D3040400; Cold Water Extension=28 7/8"; Cold Water NPT=3"; Cold Water Radius=1 1/2"; Control Panel Extension=34 7/8"; Drain Extension=31 3/4"; Drain NPT=1 1/2"; Drain Radius=3/4"; Enclosure Location=17"; Energy Extension=32 5/8"; Flat Side Distance=55 3/4"; Front Skid Extension=82 7/8"; Height to Cold Inlet=18 1/4"; Height to Drain=1 3/4"; Height to Energy=30"; Height to Hot Outlet=57 3/8"; Height to Relief=58"; Hot Outlet Angle=90.00°; Hot Water Extension=28 7/8"; Hot Water NPT=3"; Hot Water Radius=1 1/2"; Large Visibility=No; Rear Skid Extension=27 7/8"; Recovery Rate 40F to 140F @15psi=330 gph; Relief Extension=30 7/8"; Skid Center Dist=13 1/2"; Skid Length=55"; Skid Spacing=27"; Small Visibility=Yes; Steam Return NPT=3/4"; Steam Return Radius=3/8"; Steam Return Y=1 11/16"; Steam Supply Conn Y=1 5/16"; Steam Supply NPT=1"; Steam Supply Radius=1/2"; Steam Supply Total Z=15 5/16"; Steam Supply X=12 11/16"; Steam Supply Y=1 5/16"; Steam Supply Z=7 1/8"; Steam flow lb/h 40F to 140F @15psi=280; Supply Pipe Conn Y=1 5/16"; U Tube Extension=8 3/16"; U Tube Radius=2 1/4"; Unit Height=75 3/4"; Unit Radius=27 7/8"; Weight=1525
- 2650 L 600A-QSD: Assembly Code=D3040400; Cold Water Extension=28 7/8"; Cold Water NPT=3"; Cold Water Radius=1 1/2"; Control Panel Extension=34 7/8"; Drain Extension=31 3/4"; Drain NPT=1 1/2"; Drain Radius=3/4"; Enclosure Location=23"; Energy Extension=32 5/8"; Flat Side Distance=55 3/4"; Front Skid Extension=82 7/8"; Height to Cold Inlet=18 1/4"; Height to Drain=1 3/4"; Height to Energy=30"; Height to Hot Outlet=69 3/8"; Height to Relief=70"; Hot Outlet Angle=90.00°; Hot Water Extension=28 7/8"; Hot Water NPT=3"; Hot Water Radius=1 1/2"; Large Visibility=Yes; Rear Skid Extension=27 7/8"; Recovery Rate 40F to 140F @15psi=2650 gph; Relief Extension=30 7/8"; Skid Center Dist=13 1/2"; Skid Length=55"; Skid Spacing=27"; Small Visibility=No; Steam Return NPT=2"; Steam Return Radius=1"; Steam Return Y=4 1/16"; Steam Supply Conn Y=2 11/16"; Steam Supply NPT=2 1/2"; Steam Supply Radius=1 1/4"; Steam Supply Total Z=19 3/4"; Steam Supply X=25 1/2"; Steam Supply Y=8 9/16"; Steam Supply Z=10 13/16"; Steam flow lb/h 40F to 140F @15psi=2300; Supply Pipe Conn Y=11 1/4"; U Tube Extension=8 15/16"; U Tube Radius=5 3/8"; Unit Height=87 3/4"; Unit Radius=27 7/8"; Weight=2200
- 2650 L 500A-QSD: Assembly Code=D3040400; Cold Water Extension=28 7/8"; Cold Water NPT=3"; Cold Water Radius=1 1/2"; Control Panel Extension=34 7/8"; Drain Extension=31 3/4"; Drain NPT=1 1/2"; Drain Radius=3/4"; Enclosure Location=17"; Energy Extension=32 5/8"; Flat Side Distance=55 3/4"; Front Skid Extension=82 7/8"; Height to Cold Inlet=18 1/4"; Height to Drain=1 3/4"; Height to Energy=30"; Height to Hot Outlet=57 3/8"; Height to Relief=58"; Hot Outlet Angle=90.00°; Hot Water Extension=28 7/8"; Hot Water NPT=3"; Hot Water Radius=1 1/2"; Large Visibility=Yes; Rear Skid Extension=27 7/8"; Recovery Rate 40F to 140F @15psi=2650 gph; Relief Extension=30 7/8"; Skid Center Dist=13 1/2"; Skid Length=55"; Skid Spacing=27"; Small Visibility=No; Steam Return NPT=2"; Steam Return Radius=1"; Steam Return Y=4 1/16"; Steam Supply Conn Y=2 11/16"; Steam Supply NPT=2 1/2"; Steam Supply Radius=1 1/4"; Steam Supply Total Z=19 3/4"; Steam Supply X=25 1/2"; Steam Supply Y=8 9/16"; Steam Supply Z=10 13/16"; Steam flow lb/h 40F to 140F @15psi=2300; Supply Pipe Conn Y=11 1/4"; U Tube Extension=8 15/16"; U Tube Radius=5 3/8"; Unit Height=75 3/4"; Unit Radius=27 7/8"; Weight=1975
- 2280 L 600A-QS: Assembly Code=D3040400; Cold Water Extension=28 7/8"; Cold Water NPT=3"; Cold Water Radius=1 1/2"; Control Panel Extension=34 7/8"; Drain Extension=31 3/4"; Drain NPT=1 1/2"; Drain Radius=3/4"; Enclosure Location=23"; Energy Extension=32 5/8"; Flat Side Distance=55 3/4"; Front Skid Extension=82 7/8"; Height to Cold Inlet=18 1/4"; Height to Drain=1 3/4"; Height to Energy=30"; Height to Hot Outlet=69 3/8"; Height to Relief=70"; Hot Outlet Angle=90.00°; Hot Water Extension=28 7/8"; Hot Water NPT=3"; Hot Water Radius=1 1/2"; Large Visibility=Yes; Rear Skid Extension=27 7/8"; Recovery Rate 40F to 140F @15psi=2280 gph; Relief Extension=30 7/8"; Skid Center Dist=13 1/2"; Skid Length=55"; Skid Spacing=27"; Small Visibility=No; Steam Return NPT=1 1/4"; Steam Return Radius=5/8"; Steam Return Y=3 3/8"; Steam Supply Conn Y=2 1/4"; Steam Supply NPT=2 1/2"; Steam Supply Radius=1 1/4"; Steam Supply Total Z=19 3/4"; Steam Supply X=25 1/2"; Steam Supply Y=8 9/16"; Steam Supply Z=10 13/16"; Steam flow lb/h 40F to 140F @15psi=1980; Supply Pipe Conn Y=10 13/16"; U Tube Extension=8 15/16"; U Tube Radius=4 5/16"; Unit Height=87 3/4"; Unit Radius=27 7/8"; Weight=2050
- 2280 L 500A-QS: Assembly Code=D3040400; Cold Water Extension=28 7/8"; Cold Water NPT=3"; Cold Water Radius=1 1/2"; Control Panel Extension=34 7/8"; Drain Extension=31 3/4"; Drain NPT=1 1/2"; Drain Radius=3/4"; Enclosure Location=17"; Energy Extension=32 5/8"; Flat Side Distance=55 3/4"; Front Skid Extension=82 7/8"; Height to Cold Inlet=18 1/4"; Height to Drain=1 3/4"; Height to Energy=30"; Height to Hot Outlet=57 3/8"; Height to Relief=58"; Hot Outlet Angle=90.00°; Hot Water Extension=28 7/8"; Hot Water NPT=3"; Hot Water Radius=1 1/2"; Large Visibility=Yes; Rear Skid Extension=27 7/8"; Recovery Rate 40F to 140F @15psi=2280 gph; Relief Extension=30 7/8"; Skid Center Dist=13 1/2"; Skid Length=55"; Skid Spacing=27"; Small Visibility=No; Steam Return NPT=1 1/4"; Steam Return Radius=5/8"; Steam Return Y=3 3/8"; Steam Supply Conn Y=2 1/4"; Steam Supply NPT=2 1/2"; Steam Supply Radius=1 1/4"; Steam Supply Total Z=19 3/4"; Steam Supply X=25 1/2"; Steam Supply Y=8 9/16"; Steam Supply Z=10 13/16"; Steam flow lb/h 40F to 140F @15psi=1980; Supply Pipe Conn Y=10 13/16"; U Tube Extension=8 15/16"; U Tube Radius=4 5/16"; Unit Height=75 3/4"; Unit Radius=27 7/8"; Weight=1825
- 1940 L 600A-QSD: Assembly Code=D3040400; Cold Water Extension=28 7/8"; Cold Water NPT=3"; Cold Water Radius=1 1/2"; Control Panel Extension=34 7/8"; Drain Extension=31 3/4"; Drain NPT=1 1/2"; Drain Radius=3/4"; Enclosure Location=23"; Energy Extension=32 5/8"; Flat Side Distance=55 3/4"; Front Skid Extension=82 7/8"; Height to Cold Inlet=18 1/4"; Height to Drain=1 3/4"; Height to Energy=30"; Height to Hot Outlet=69 3/8"; Height to Relief=70"; Hot Outlet Angle=90.00°; Hot Water Extension=28 7/8"; Hot Water NPT=3"; Hot Water Radius=1 1/2"; Large Visibility=No; Rear Skid Extension=27 7/8"; Recovery Rate 40F to 140F @15psi=1940 gph; Relief Extension=30 7/8"; Skid Center Dist=13 1/2"; Skid Length=55"; Skid Spacing=27"; Small Visibility=Yes; Steam Return NPT=1 1/4"; Steam Return Radius=5/8"; Steam Return Y=3 3/8"; Steam Supply Conn Y=2 1/4"; Steam Supply NPT=2 1/2"; Steam Supply Radius=1 1/4"; Steam Supply Total Z=17 1/8"; Steam Supply X=17 3/16"; Steam Supply Y=2 1/4"; Steam Supply Z=8 3/16"; Steam flow lb/h 40F to 140F @15psi=1680; Supply Pipe Conn Y=2 1/4"; U Tube Extension=8 15/16"; U Tube Radius=4 5/16"; Unit Height=87 3/4"; Unit Radius=27 7/8"; Weight=2100
- 1940 L 500A-QSD: Assembly Code=D3040400; Cold Water Extension=28 7/8"; Cold Water NPT=3"; Cold Water Radius=1 1/2"; Control Panel Extension=34 7/8"; Drain Extension=31 3/4"; Drain NPT=1 1/2"; Drain Radius=3/4"; Enclosure Location=17"; Energy Extension=32 5/8"; Flat Side Distance=55 3/4"; Front Skid Extension=82 7/8"; Height to Cold Inlet=18 1/4"; Height to Drain=1 3/4"; Height to Energy=30"; Height to Hot Outlet=57 3/8"; Height to Relief=58"; Hot Outlet Angle=90.00°; Hot Water Extension=28 7/8"; Hot Water NPT=3"; Hot Water Radius=1 1/2"; Large Visibility=No; Rear Skid Extension=27 7/8"; Recovery Rate 40F to 140F @15psi=1940 gph; Relief Extension=30 7/8"; Skid Center Dist=13 1/2"; Skid Length=55"; Skid Spacing=27"; Small Visibility=Yes; Steam Return NPT=1 1/4"; Steam Return Radius=5/8"; Steam Return Y=3 3/8"; Steam Supply Conn Y=2 1/4"; Steam Supply NPT=2 1/2"; Steam Supply Radius=1 1/4"; Steam Supply Total Z=17 1/8"; Steam Supply X=17 3/16"; Steam Supply Y=2 1/4"; Steam Supply Z=8 3/16"; Steam flow lb/h 40F to 140F @15psi=1680; Supply Pipe Conn Y=2 1/4"; U Tube Extension=8 15/16"; U Tube Radius=4 5/16"; Unit Height=75 3/4"; Unit Radius=27 7/8"; Weight=1875
- 1780 L 600A-QS: Assembly Code=D3040400; Cold Water Extension=28 7/8"; Cold Water NPT=3"; Cold Water Radius=1 1/2"; Control Panel Extension=34 7/8"; Drain Extension=31 3/4"; Drain NPT=1 1/2"; Drain Radius=3/4"; Enclosure Location=23"; Energy Extension=32 5/8"; Flat Side Distance=55 3/4"; Front Skid Extension=82 7/8"; Height to Cold Inlet=18 1/4"; Height to Drain=1 3/4"; Height to Energy=30"; Height to Hot Outlet=69 3/8"; Height to Relief=70"; Hot Outlet Angle=90.00°; Hot Water Extension=28 7/8"; Hot Water NPT=3"; Hot Water Radius=1 1/2"; Large Visibility=Yes; Rear Skid Extension=27 7/8"; Recovery Rate 40F to 140F @15psi=1780 gph; Relief Extension=30 7/8"; Skid Center Dist=13 1/2"; Skid Length=55"; Skid Spacing=27"; Small Visibility=No; Steam Return NPT=1 1/4"; Steam Return Radius=5/8"; Steam Return Y=3 3/8"; Steam Supply Conn Y=2 1/4"; Steam Supply NPT=2 1/2"; Steam Supply Radius=1 1/4"; Steam Supply Total Z=19 3/4"; Steam Supply X=25 1/2"; Steam Supply Y=8 9/16"; Steam Supply Z=10 13/16"; Steam flow lb/h 40F to 140F @15psi=1540; Supply Pipe Conn Y=10 13/16"; U Tube Extension=8 15/16"; U Tube Radius=4 5/16"; Unit Height=87 3/4"; Unit Radius=27 7/8"; Weight=2000
- 1780 L 500A-QS: Assembly Code=D3040400; Cold Water Extension=28 7/8"; Cold Water NPT=3"; Cold Water Radius=1 1/2"; Control Panel Extension=34 7/8"; Drain Extension=31 3/4"; Drain NPT=1 1/2"; Drain Radius=3/4"; Enclosure Location=17"; Energy Extension=32 5/8"; Flat Side Distance=55 3/4"; Front Skid Extension=82 7/8"; Height to Cold Inlet=18 1/4"; Height to Drain=1 3/4"; Height to Energy=30"; Height to Hot Outlet=57 3/8"; Height to Relief=58"; Hot Outlet Angle=90.00°; Hot Water Extension=28 7/8"; Hot Water NPT=3"; Hot Water Radius=1 1/2"; Large Visibility=Yes; Rear Skid Extension=27 7/8"; Recovery Rate 40F to 140F @15psi=1780 gph; Relief Extension=30 7/8"; Skid Center Dist=13 1/2"; Skid Length=55"; Skid Spacing=27"; Small Visibility=No; Steam Return NPT=1 1/4"; Steam Return Radius=5/8"; Steam Return Y=3 3/8"; Steam Supply Conn Y=2 1/4"; Steam Supply NPT=2 1/2"; Steam Supply Radius=1 1/4"; Steam Supply Total Z=19 3/4"; Steam Supply X=25 1/2"; Steam Supply Y=8 9/16"; Steam Supply Z=10 13/16"; Steam flow lb/h 40F to 140F @15psi=1540; Supply Pipe Conn Y=10 13/16"; U Tube Extension=8 15/16"; U Tube Radius=4 5/16"; Unit Height=75 3/4"; Unit Radius=27 7/8"; Weight=1775
- 1520 L 600A-QSD: Assembly Code=D3040400; Cold Water Extension=28 7/8"; Cold Water NPT=3"; Cold Water Radius=1 1/2"; Control Panel Extension=34 7/8"; Drain Extension=31 3/4"; Drain NPT=1 1/2"; Drain Radius=3/4"; Enclosure Location=23"; Energy Extension=32 5/8"; Flat Side Distance=55 3/4"; Front Skid Extension=82 7/8"; Height to Cold Inlet=18 1/4"; Height to Drain=1 3/4"; Height to Energy=30"; Height to Hot Outlet=69 3/8"; Height to Relief=70"; Hot Outlet Angle=90.00°; Hot Water Extension=28 7/8"; Hot Water NPT=3"; Hot Water Radius=1 1/2"; Large Visibility=No; Rear Skid Extension=27 7/8"; Recovery Rate 40F to 140F @15psi=1520 gph; Relief Extension=30 7/8"; Skid Center Dist=13 1/2"; Skid Length=55"; Skid Spacing=27"; Small Visibility=Yes; Steam Return NPT=1 1/4"; Steam Return Radius=5/8"; Steam Return Y=3 3/8"; Steam Supply Conn Y=2 1/4"; Steam Supply NPT=2"; Steam Supply Radius=1"; Steam Supply Total Z=17 1/8"; Steam Supply X=17 3/16"; Steam Supply Y=2 1/4"; Steam Supply Z=8 3/16"; Steam flow lb/h 40F to 140F @15psi=1320; Supply Pipe Conn Y=2 1/4"; U Tube Extension=8 15/16"; U Tube Radius=4 5/16"; Unit Height=87 3/4"; Unit Radius=27 7/8"; Weight=2100
- 1520 L 500A-QSD: Assembly Code=D3040400; Cold Water Extension=28 7/8"; Cold Water NPT=3"; Cold Water Radius=1 1/2"; Control Panel Extension=34 7/8"; Drain Extension=31 3/4"; Drain NPT=1 1/2"; Drain Radius=3/4"; Enclosure Location=17"; Energy Extension=32 5/8"; Flat Side Distance=55 3/4"; Front Skid Extension=82 7/8"; Height to Cold Inlet=18 1/4"; Height to Drain=1 3/4"; Height to Energy=30"; Height to Hot Outlet=57 3/8"; Height to Relief=58"; Hot Outlet Angle=90.00°; Hot Water Extension=28 7/8"; Hot Water NPT=3"; Hot Water Radius=1 1/2"; Large Visibility=No; Rear Skid Extension=27 7/8"; Recovery Rate 40F to 140F @15psi=1520 gph; Relief Extension=30 7/8"; Skid Center Dist=13 1/2"; Skid Length=55"; Skid Spacing=27"; Small Visibility=Yes; Steam Return NPT=1 1/4"; Steam Return Radius=5/8"; Steam Return Y=3 3/8"; Steam Supply Conn Y=2 1/4"; Steam Supply NPT=2"; Steam Supply Radius=1"; Steam Supply Total Z=17 1/8"; Steam Supply X=17 3/16"; Steam Supply Y=2 1/4"; Steam Supply Z=8 3/16"; Steam flow lb/h 40F to 140F @15psi=1320; Supply Pipe Conn Y=2 1/4"; U Tube Extension=8 15/16"; U Tube Radius=4 5/16"; Unit Height=75 3/4"; Unit Radius=27 7/8"; Weight=1875
- 1230 L 600A-QS: Assembly Code=D3040400; Cold Water Extension=28 7/8"; Cold Water NPT=3"; Cold Water Radius=1 1/2"; Control Panel Extension=34 7/8"; Drain Extension=31 3/4"; Drain NPT=1 1/2"; Drain Radius=3/4"; Enclosure Location=23"; Energy Extension=32 5/8"; Flat Side Distance=55 3/4"; Front Skid Extension=82 7/8"; Height to Cold Inlet=18 1/4"; Height to Drain=1 3/4"; Height to Energy=30"; Height to Hot Outlet=69 3/8"; Height to Relief=70"; Hot Outlet Angle=90.00°; Hot Water Extension=28 7/8"; Hot Water NPT=3"; Hot Water Radius=1 1/2"; Large Visibility=Yes; Rear Skid Extension=27 7/8"; Recovery Rate 40F to 140F @15psi=1230 gph; Relief Extension=30 7/8"; Skid Center Dist=13 1/2"; Skid Length=55"; Skid Spacing=27"; Small Visibility=No; Steam Return NPT=1"; Steam Return Radius=1/2"; Steam Return Y=2 9/16"; Steam Supply Conn Y=1 7/8"; Steam Supply NPT=2"; Steam Supply Radius=1"; Steam Supply Total Z=17 1/8"; Steam Supply X=17 3/16"; Steam Supply Y=2 1/4"; Steam Supply Z=8 3/16"; Steam flow lb/h 40F to 140F @15psi=1070; Supply Pipe Conn Y=4 1/8"; U Tube Extension=8 15/16"; U Tube Radius=3 3/8"; Unit Height=87 3/4"; Unit Radius=27 7/8"; Weight=1950
- 1230 L 500A-QS: Assembly Code=D3040400; Cold Water Extension=28 7/8"; Cold Water NPT=3"; Cold Water Radius=1 1/2"; Control Panel Extension=34 7/8"; Drain Extension=31 3/4"; Drain NPT=1 1/2"; Drain Radius=3/4"; Enclosure Location=17"; Energy Extension=32 5/8"; Flat Side Distance=55 3/4"; Front Skid Extension=82 7/8"; Height to Cold Inlet=18 1/4"; Height to Drain=1 3/4"; Height to Energy=30"; Height to Hot Outlet=57 3/8"; Height to Relief=58"; Hot Outlet Angle=90.00°; Hot Water Extension=28 7/8"; Hot Water NPT=3"; Hot Water Radius=1 1/2"; Large Visibility=Yes; Rear Skid Extension=27 7/8"; Recovery Rate 40F to 140F @15psi=1230 gph; Relief Extension=30 7/8"; Skid Center Dist=13 1/2"; Skid Length=55"; Skid Spacing=27"; Small Visibility=No; Steam Return NPT=1"; Steam Return Radius=1/2"; Steam Return Y=2 9/16"; Steam Supply Conn Y=1 7/8"; Steam Supply NPT=2"; Steam Supply Radius=1"; Steam Supply Total Z=17 1/8"; Steam Supply X=17 3/16"; Steam Supply Y=2 1/4"; Steam Supply Z=8 3/16"; Steam flow lb/h 40F to 140F @15psi=1070; Supply Pipe Conn Y=4 1/8"; U Tube Extension=8 15/16"; U Tube Radius=3 3/8"; Unit Height=75 3/4"; Unit Radius=27 7/8"; Weight=1725
- 900 L 600A-QS: Assembly Code=D3040400; Cold Water Extension=28 7/8"; Cold Water NPT=3"; Cold Water Radius=1 1/2"; Control Panel Extension=34 7/8"; Drain Extension=31 3/4"; Drain NPT=1 1/2"; Drain Radius=3/4"; Enclosure Location=23"; Energy Extension=32 5/8"; Flat Side Distance=55 3/4"; Front Skid Extension=82 7/8"; Height to Cold Inlet=18 1/4"; Height to Drain=1 3/4"; Height to Energy=30"; Height to Hot Outlet=69 3/8"; Height to Relief=70"; Hot Outlet Angle=90.00°; Hot Water Extension=28 7/8"; Hot Water NPT=3"; Hot Water Radius=1 1/2"; Large Visibility=No; Rear Skid Extension=27 7/8"; Recovery Rate 40F to 140F @15psi=900 gph; Relief Extension=30 7/8"; Skid Center Dist=13 1/2"; Skid Length=55"; Skid Spacing=27"; Small Visibility=Yes; Steam Return NPT=1"; Steam Return Radius=1/2"; Steam Return Y=2 9/16"; Steam Supply Conn Y=1 7/8"; Steam Supply NPT=2"; Steam Supply Radius=1"; Steam Supply Total Z=18"; Steam Supply X=14 1/16"; Steam Supply Y=1 7/8"; Steam Supply Z=9 1/16"; Steam flow lb/h 40F to 140F @15psi=780; Supply Pipe Conn Y=1 7/8"; U Tube Extension=8 15/16"; U Tube Radius=3 3/8"; Unit Height=87 3/4"; Unit Radius=27 7/8"; Weight=1950
- 900 L 500A-QS: Assembly Code=D3040400; Cold Water Extension=28 7/8"; Cold Water NPT=3"; Cold Water Radius=1 1/2"; Control Panel Extension=34 7/8"; Drain Extension=31 3/4"; Drain NPT=1 1/2"; Drain Radius=3/4"; Enclosure Location=17"; Energy Extension=32 5/8"; Flat Side Distance=55 3/4"; Front Skid Extension=82 7/8"; Height to Cold Inlet=18 1/4"; Height to Drain=1 3/4"; Height to Energy=30"; Height to Hot Outlet=57 3/8"; Height to Relief=58"; Hot Outlet Angle=90.00°; Hot Water Extension=28 7/8"; Hot Water NPT=3"; Hot Water Radius=1 1/2"; Large Visibility=No; Rear Skid Extension=27 7/8"; Recovery Rate 40F to 140F @15psi=900 gph; Relief Extension=30 7/8"; Skid Center Dist=13 1/2"; Skid Length=55"; Skid Spacing=27"; Small Visibility=Yes; Steam Return NPT=1"; Steam Return Radius=1/2"; Steam Return Y=2 9/16"; Steam Supply Conn Y=1 7/8"; Steam Supply NPT=2"; Steam Supply Radius=1"; Steam Supply Total Z=18"; Steam Supply X=14 1/16"; Steam Supply Y=1 7/8"; Steam Supply Z=9 1/16"; Steam flow lb/h 40F to 140F @15psi=780; Supply Pipe Conn Y=1 7/8"; U Tube Extension=8 15/16"; U Tube Radius=3 3/8"; Unit Height=75 3/4"; Unit Radius=27 7/8"; Weight=1725
- 830 L 600A-QSD: Assembly Code=D3040400; Cold Water Extension=28 7/8"; Cold Water NPT=3"; Cold Water Radius=1 1/2"; Control Panel Extension=34 7/8"; Drain Extension=31 3/4"; Drain NPT=1 1/2"; Drain Radius=3/4"; Enclosure Location=23"; Energy Extension=32 5/8"; Flat Side Distance=55 3/4"; Front Skid Extension=82 7/8"; Height to Cold Inlet=18 1/4"; Height to Drain=1 3/4"; Height to Energy=30"; Height to Hot Outlet=69 3/8"; Height to Relief=70"; Hot Outlet Angle=90.00°; Hot Water Extension=28 7/8"; Hot Water NPT=3"; Hot Water Radius=1 1/2"; Large Visibility=No; Rear Skid Extension=27 7/8"; Recovery Rate 40F to 140F @15psi=830 gph; Relief Extension=30 7/8"; Skid Center Dist=13 1/2"; Skid Length=55"; Skid Spacing=27"; Small Visibility=Yes; Steam Return NPT=1"; Steam Return Radius=1/2"; Steam Return Y=2 9/16"; Steam Supply Conn Y=1 7/8"; Steam Supply NPT=1 1/2"; Steam Supply Radius=3/4"; Steam Supply Total Z=18"; Steam Supply X=14 1/16"; Steam Supply Y=1 7/8"; Steam Supply Z=9 1/16"; Steam flow lb/h 40F to 140F @15psi=720; Supply Pipe Conn Y=1 7/8"; U Tube Extension=8 15/16"; U Tube Radius=3 3/8"; Unit Height=87 3/4"; Unit Radius=27 7/8"; Weight=2000
- 830 L 500A-QSD: Assembly Code=D3040400; Cold Water Extension=28 7/8"; Cold Water NPT=3"; Cold Water Radius=1 1/2"; Control Panel Extension=34 7/8"; Drain Extension=31 3/4"; Drain NPT=1 1/2"; Drain Radius=3/4"; Enclosure Location=17"; Energy Extension=32 5/8"; Flat Side Distance=55 3/4"; Front Skid Extension=82 7/8"; Height to Cold Inlet=18 1/4"; Height to Drain=1 3/4"; Height to Energy=30"; Height to Hot Outlet=57 3/8"; Height to Relief=58"; Hot Outlet Angle=90.00°; Hot Water Extension=28 7/8"; Hot Water NPT=3"; Hot Water Radius=1 1/2"; Large Visibility=No; Rear Skid Extension=27 7/8"; Recovery Rate 40F to 140F @15psi=830 gph; Relief Extension=30 7/8"; Skid Center Dist=13 1/2"; Skid Length=55"; Skid Spacing=27"; Small Visibility=Yes; Steam Return NPT=1"; Steam Return Radius=1/2"; Steam Return Y=2 9/16"; Steam Supply Conn Y=1 7/8"; Steam Supply NPT=1 1/2"; Steam Supply Radius=3/4"; Steam Supply Total Z=18"; Steam Supply X=14 1/16"; Steam Supply Y=1 7/8"; Steam Supply Z=9 1/16"; Steam flow lb/h 40F to 140F @15psi=720; Supply Pipe Conn Y=1 7/8"; U Tube Extension=8 15/16"; U Tube Radius=3 3/8"; Unit Height=75 3/4"; Unit Radius=27 7/8"; Weight=1775
- 520 L 900A-QS: Assembly Code=D3040400; Cold Water Extension=34 1/4"; Cold Water NPT=3"; Cold Water Radius=1 1/2"; Control Panel Extension=40 1/4"; Drain Extension=37 1/8"; Drain NPT=1 1/2"; Drain Radius=3/4"; Enclosure Location=20"; Energy Extension=38 1/4"; Flat Side Distance=66 1/2"; Front Skid Extension=100 1/4"; Height to Cold Inlet=20 3/8"; Height to Drain=3 7/8"; Height to Energy=32 5/8"; Height to Hot Outlet=72 7/8"; Height to Relief=73 1/2"; Hot Outlet Angle=90.00°; Hot Water Extension=34 1/4"; Hot Water NPT=3"; Hot Water Radius=1 1/2"; Large Visibility=No; Rear Skid Extension=33 1/4"; Recovery Rate 40F to 140F @15psi=520 gph; Relief Extension=36 1/4"; Skid Center Dist=18"; Skid Length=67"; Skid Spacing=36"; Small Visibility=Yes; Steam Return NPT=3/4"; Steam Return Radius=3/8"; Steam Return Y=1 11/16"; Steam Supply Conn Y=1 5/16"; Steam Supply NPT=1 1/2"; Steam Supply Radius=3/4"; Steam Supply Total Z=15 5/16"; Steam Supply X=12 11/16"; Steam Supply Y=1 5/16"; Steam Supply Z=7 1/8"; Steam flow lb/h 40F to 140F @15psi=450; Supply Pipe Conn Y=1 5/16"; U Tube Extension=8 3/16"; U Tube Radius=2 1/4"; Unit Height=93 1/4"; Unit Radius=33 1/4"; Weight=2270
- 520 L 750A-QS: Assembly Code=D3040400; Cold Water Extension=34 1/4"; Cold Water NPT=3"; Cold Water Radius=1 1/2"; Control Panel Extension=40 1/4"; Drain Extension=37 1/8"; Drain NPT=1 1/2"; Drain Radius=3/4"; Enclosure Location=20"; Energy Extension=38 1/4"; Flat Side Distance=66 1/2"; Front Skid Extension=100 1/4"; Height to Cold Inlet=20 3/8"; Height to Drain=3 7/8"; Height to Energy=32 5/8"; Height to Hot Outlet=60 7/8"; Height to Relief=61 1/2"; Hot Outlet Angle=90.00°; Hot Water Extension=34 1/4"; Hot Water NPT=3"; Hot Water Radius=1 1/2"; Large Visibility=No; Rear Skid Extension=33 1/4"; Recovery Rate 40F to 140F @15psi=520 gph; Relief Extension=36 1/4"; Skid Center Dist=18"; Skid Length=67"; Skid Spacing=36"; Small Visibility=Yes; Steam Return NPT=3/4"; Steam Return Radius=3/8"; Steam Return Y=1 11/16"; Steam Supply Conn Y=1 5/16"; Steam Supply NPT=1 1/2"; Steam Supply Radius=3/4"; Steam Supply Total Z=15 5/16"; Steam Supply X=12 11/16"; Steam Supply Y=1 5/16"; Steam Supply Z=7 1/8"; Steam flow lb/h 40F to 140F @15psi=450; Supply Pipe Conn Y=1 5/16"; U Tube Extension=8 3/16"; U Tube Radius=2 1/4"; Unit Height=81 1/4"; Unit Radius=33 1/4"; Weight=2040
- 440 L 900A-QSD: Assembly Code=D3040400; Cold Water Extension=34 1/4"; Cold Water NPT=3"; Cold Water Radius=1 1/2"; Control Panel Extension=40 1/4"; Drain Extension=37 1/8"; Drain NPT=1 1/2"; Drain Radius=3/4"; Enclosure Location=20"; Energy Extension=38 1/4"; Flat Side Distance=66 1/2"; Front Skid Extension=100 1/4"; Height to Cold Inlet=20 3/8"; Height to Drain=3 7/8"; Height to Energy=32 5/8"; Height to Hot Outlet=72 7/8"; Height to Relief=73 1/2"; Hot Outlet Angle=90.00°; Hot Water Extension=34 1/4"; Hot Water NPT=3"; Hot Water Radius=1 1/2"; Large Visibility=No; Rear Skid Extension=33 1/4"; Recovery Rate 40F to 140F @15psi=440 gph; Relief Extension=36 1/4"; Skid Center Dist=18"; Skid Length=67"; Skid Spacing=36"; Small Visibility=Yes; Steam Return NPT=3/4"; Steam Return Radius=3/8"; Steam Return Y=1 11/16"; Steam Supply Conn Y=1 5/16"; Steam Supply NPT=1"; Steam Supply Radius=1/2"; Steam Supply Total Z=15 5/16"; Steam Supply X=12 11/16"; Steam Supply Y=1 5/16"; Steam Supply Z=7 1/8"; Steam flow lb/h 40F to 140F @15psi=380; Supply Pipe Conn Y=1 5/16"; U Tube Extension=8 3/16"; U Tube Radius=2 1/4"; Unit Height=93 1/4"; Unit Radius=33 1/4"; Weight=2270
- 440 L 750A-QSD: Assembly Code=D3040400; Cold Water Extension=34 1/4"; Cold Water NPT=3"; Cold Water Radius=1 1/2"; Control Panel Extension=40 1/4"; Drain Extension=37 1/8"; Drain NPT=1 1/2"; Drain Radius=3/4"; Enclosure Location=20"; Energy Extension=38 1/4"; Flat Side Distance=66 1/2"; Front Skid Extension=100 1/4"; Height to Cold Inlet=20 3/8"; Height to Drain=3 7/8"; Height to Energy=32 5/8"; Height to Hot Outlet=60 7/8"; Height to Relief=61 1/2"; Hot Outlet Angle=90.00°; Hot Water Extension=34 1/4"; Hot Water NPT=3"; Hot Water Radius=1 1/2"; Large Visibility=No; Rear Skid Extension=33 1/4"; Recovery Rate 40F to 140F @15psi=440 gph; Relief Extension=36 1/4"; Skid Center Dist=18"; Skid Length=67"; Skid Spacing=36"; Small Visibility=Yes; Steam Return NPT=3/4"; Steam Return Radius=3/8"; Steam Return Y=1 11/16"; Steam Supply Conn Y=1 5/16"; Steam Supply NPT=1"; Steam Supply Radius=1/2"; Steam Supply Total Z=15 5/16"; Steam Supply X=12 11/16"; Steam Supply Y=1 5/16"; Steam Supply Z=7 1/8"; Steam flow lb/h 40F to 140F @15psi=380; Supply Pipe Conn Y=1 5/16"; U Tube Extension=8 3/16"; U Tube Radius=2 1/4"; Unit Height=81 1/4"; Unit Radius=33 1/4"; Weight=2040
- 3790 L 900A-QSD: Assembly Code=D3040400; Cold Water Extension=34 1/4"; Cold Water NPT=3"; Cold Water Radius=1 1/2"; Control Panel Extension=40 1/4"; Drain Extension=37 1/8"; Drain NPT=1 1/2"; Drain Radius=3/4"; Enclosure Location=20"; Energy Extension=38 1/4"; Flat Side Distance=66 1/2"; Front Skid Extension=100 1/4"; Height to Cold Inlet=20 3/8"; Height to Drain=3 7/8"; Height to Energy=32 5/8"; Height to Hot Outlet=72 7/8"; Height to Relief=73 1/2"; Hot Outlet Angle=90.00°; Hot Water Extension=34 1/4"; Hot Water NPT=3"; Hot Water Radius=1 1/2"; Large Visibility=Yes; Rear Skid Extension=33 1/4"; Recovery Rate 40F to 140F @15psi=3790 gph; Relief Extension=36 1/4"; Skid Center Dist=18"; Skid Length=67"; Skid Spacing=36"; Small Visibility=No; Steam Return NPT=2"; Steam Return Radius=1"; Steam Return Y=4 5/8"; Steam Supply Conn Y=3 13/16"; Steam Supply NPT=2 1/2"; Steam Supply Radius=1 1/4"; Steam Supply Total Z=18 15/16"; Steam Supply X=25 1/2"; Steam Supply Y=8 9/16"; Steam Supply Z=10 13/16"; Steam flow lb/h 40F to 140F @15psi=3300; Supply Pipe Conn Y=12 3/8"; U Tube Extension=8 1/8"; U Tube Radius=6 3/8"; Unit Height=93 1/4"; Unit Radius=33 1/4"; Weight=2770
- 3790 L 750A-QSD: Assembly Code=D3040400; Cold Water Extension=34 1/4"; Cold Water NPT=3"; Cold Water Radius=1 1/2"; Control Panel Extension=40 1/4"; Drain Extension=37 1/8"; Drain NPT=1 1/2"; Drain Radius=3/4"; Enclosure Location=20"; Energy Extension=38 1/4"; Flat Side Distance=66 1/2"; Front Skid Extension=100 1/4"; Height to Cold Inlet=20 3/8"; Height to Drain=3 7/8"; Height to Energy=32 5/8"; Height to Hot Outlet=60 7/8"; Height to Relief=61 1/2"; Hot Outlet Angle=90.00°; Hot Water Extension=34 1/4"; Hot Water NPT=3"; Hot Water Radius=1 1/2"; Large Visibility=Yes; Rear Skid Extension=33 1/4"; Recovery Rate 40F to 140F @15psi=3790 gph; Relief Extension=36 1/4"; Skid Center Dist=18"; Skid Length=67"; Skid Spacing=36"; Small Visibility=No; Steam Return NPT=2"; Steam Return Radius=1"; Steam Return Y=4 5/8"; Steam Supply Conn Y=3 13/16"; Steam Supply NPT=2 1/2"; Steam Supply Radius=1 1/4"; Steam Supply Total Z=18 15/16"; Steam Supply X=25 1/2"; Steam Supply Y=8 9/16"; Steam Supply Z=10 13/16"; Steam flow lb/h 40F to 140F @15psi=3300; Supply Pipe Conn Y=12 3/8"; U Tube Extension=8 1/8"; U Tube Radius=6 3/8"; Unit Height=81 1/4"; Unit Radius=33 1/4"; Weight=2540
- 3790 L 900A-QS: Assembly Code=D3040400; Cold Water Extension=34 1/4"; Cold Water NPT=3"; Cold Water Radius=1 1/2"; Control Panel Extension=40 1/4"; Drain Extension=37 1/8"; Drain NPT=1 1/2"; Drain Radius=3/4"; Enclosure Location=20"; Energy Extension=38 1/4"; Flat Side Distance=66 1/2"; Front Skid Extension=100 1/4"; Height to Cold Inlet=20 3/8"; Height to Drain=3 7/8"; Height to Energy=32 5/8"; Height to Hot Outlet=72 7/8"; Height to Relief=73 1/2"; Hot Outlet Angle=90.00°; Hot Water Extension=34 1/4"; Hot Water NPT=3"; Hot Water Radius=1 1/2"; Large Visibility=Yes; Rear Skid Extension=33 1/4"; Recovery Rate 40F to 140F @15psi=3790 gph; Relief Extension=36 1/4"; Skid Center Dist=18"; Skid Length=67"; Skid Spacing=36"; Small Visibility=No; Steam Return NPT=2"; Steam Return Radius=1"; Steam Return Y=4 5/8"; Steam Supply Conn Y=3 13/16"; Steam Supply NPT=2 1/2"; Steam Supply Radius=1 1/4"; Steam Supply Total Z=18 15/16"; Steam Supply X=25 1/2"; Steam Supply Y=8 9/16"; Steam Supply Z=10 13/16"; Steam flow lb/h 40F to 140F @15psi=3300; Supply Pipe Conn Y=12 3/8"; U Tube Extension=8 1/8"; U Tube Radius=6 3/8"; Unit Height=93 1/4"; Unit Radius=33 1/4"; Weight=2520
- 3790 L 750A-QS: Assembly Code=D3040400; Cold Water Extension=34 1/4"; Cold Water NPT=3"; Cold Water Radius=1 1/2"; Control Panel Extension=40 1/4"; Drain Extension=37 1/8"; Drain NPT=1 1/2"; Drain Radius=3/4"; Enclosure Location=20"; Energy Extension=38 1/4"; Flat Side Distance=66 1/2"; Front Skid Extension=100 1/4"; Height to Cold Inlet=20 3/8"; Height to Drain=3 7/8"; Height to Energy=32 5/8"; Height to Hot Outlet=60 7/8"; Height to Relief=61 1/2"; Hot Outlet Angle=90.00°; Hot Water Extension=34 1/4"; Hot Water NPT=3"; Hot Water Radius=1 1/2"; Large Visibility=Yes; Rear Skid Extension=33 1/4"; Recovery Rate 40F to 140F @15psi=3790 gph; Relief Extension=36 1/4"; Skid Center Dist=18"; Skid Length=67"; Skid Spacing=36"; Small Visibility=No; Steam Return NPT=2"; Steam Return Radius=1"; Steam Return Y=4 5/8"; Steam Supply Conn Y=3 13/16"; Steam Supply NPT=2 1/2"; Steam Supply Radius=1 1/4"; Steam Supply Total Z=18 15/16"; Steam Supply X=25 1/2"; Steam Supply Y=8 9/16"; Steam Supply Z=10 13/16"; Steam flow lb/h 40F to 140F @15psi=3300; Supply Pipe Conn Y=12 3/8"; U Tube Extension=8 1/8"; U Tube Radius=6 3/8"; Unit Height=81 1/4"; Unit Radius=33 1/4"; Weight=2290
- 380 L 900A-QS: Assembly Code=D3040400; Cold Water Extension=34 1/4"; Cold Water NPT=3"; Cold Water Radius=1 1/2"; Control Panel Extension=40 1/4"; Drain Extension=37 1/8"; Drain NPT=1 1/2"; Drain Radius=3/4"; Enclosure Location=20"; Energy Extension=38 1/4"; Flat Side Distance=66 1/2"; Front Skid Extension=100 1/4"; Height to Cold Inlet=20 3/8"; Height to Drain=3 7/8"; Height to Energy=32 5/8"; Height to Hot Outlet=72 7/8"; Height to Relief=73 1/2"; Hot Outlet Angle=90.00°; Hot Water Extension=34 1/4"; Hot Water NPT=3"; Hot Water Radius=1 1/2"; Large Visibility=No; Rear Skid Extension=33 1/4"; Recovery Rate 40F to 140F @15psi=380 gph; Relief Extension=36 1/4"; Skid Center Dist=18"; Skid Length=67"; Skid Spacing=36"; Small Visibility=Yes; Steam Return NPT=3/4"; Steam Return Radius=3/8"; Steam Return Y=1 11/16"; Steam Supply Conn Y=1 5/16"; Steam Supply NPT=1"; Steam Supply Radius=1/2"; Steam Supply Total Z=15 5/16"; Steam Supply X=12 11/16"; Steam Supply Y=1 5/16"; Steam Supply Z=7 1/8"; Steam flow lb/h 40F to 140F @15psi=330; Supply Pipe Conn Y=1 5/16"; U Tube Extension=8 3/16"; U Tube Radius=2 1/4"; Unit Height=93 1/4"; Unit Radius=33 1/4"; Weight=2120
- 380 L 750A-QS: Assembly Code=D3040400; Cold Water Extension=34 1/4"; Cold Water NPT=3"; Cold Water Radius=1 1/2"; Control Panel Extension=40 1/4"; Drain Extension=37 1/8"; Drain NPT=1 1/2"; Drain Radius=3/4"; Enclosure Location=20"; Energy Extension=38 1/4"; Flat Side Distance=66 1/2"; Front Skid Extension=100 1/4"; Height to Cold Inlet=20 3/8"; Height to Drain=3 7/8"; Height to Energy=32 5/8"; Height to Hot Outlet=60 7/8"; Height to Relief=61 1/2"; Hot Outlet Angle=90.00°; Hot Water Extension=34 1/4"; Hot Water NPT=3"; Hot Water Radius=1 1/2"; Large Visibility=No; Rear Skid Extension=33 1/4"; Recovery Rate 40F to 140F @15psi=380 gph; Relief Extension=36 1/4"; Skid Center Dist=18"; Skid Length=67"; Skid Spacing=36"; Small Visibility=Yes; Steam Return NPT=3/4"; Steam Return Radius=3/8"; Steam Return Y=1 11/16"; Steam Supply Conn Y=1 5/16"; Steam Supply NPT=1"; Steam Supply Radius=1/2"; Steam Supply Total Z=15 5/16"; Steam Supply X=12 11/16"; Steam Supply Y=1 5/16"; Steam Supply Z=7 1/8"; Steam flow lb/h 40F to 140F @15psi=330; Supply Pipe Conn Y=1 5/16"; U Tube Extension=8 3/16"; U Tube Radius=2 1/4"; Unit Height=81 1/4"; Unit Radius=33 1/4"; Weight=1890
- 330 L 900A-QSD: Assembly Code=D3040400; Cold Water Extension=34 1/4"; Cold Water NPT=3"; Cold Water Radius=1 1/2"; Control Panel Extension=40 1/4"; Drain Extension=37 1/8"; Drain NPT=1 1/2"; Drain Radius=3/4"; Enclosure Location=20"; Energy Extension=38 1/4"; Flat Side Distance=66 1/2"; Front Skid Extension=100 1/4"; Height to Cold Inlet=20 3/8"; Height to Drain=3 7/8"; Height to Energy=32 5/8"; Height to Hot Outlet=72 7/8"; Height to Relief=73 1/2"; Hot Outlet Angle=90.00°; Hot Water Extension=34 1/4"; Hot Water NPT=3"; Hot Water Radius=1 1/2"; Large Visibility=No; Rear Skid Extension=33 1/4"; Recovery Rate 40F to 140F @15psi=330 gph; Relief Extension=36 1/4"; Skid Center Dist=18"; Skid Length=67"; Skid Spacing=36"; Small Visibility=Yes; Steam Return NPT=3/4"; Steam Return Radius=3/8"; Steam Return Y=1 11/16"; Steam Supply Conn Y=1 5/16"; Steam Supply NPT=1"; Steam Supply Radius=1/2"; Steam Supply Total Z=15 5/16"; Steam Supply X=12 11/16"; Steam Supply Y=1 5/16"; Steam Supply Z=7 1/8"; Steam flow lb/h 40F to 140F @15psi=280; Supply Pipe Conn Y=1 5/16"; U Tube Extension=8 3/16"; U Tube Radius=2 1/4"; Unit Height=93 1/4"; Unit Radius=33 1/4"; Weight=2120
- 330 L 750A-QSD: Assembly Code=D3040400; Cold Water Extension=34 1/4"; Cold Water NPT=3"; Cold Water Radius=1 1/2"; Control Panel Extension=40 1/4"; Drain Extension=37 1/8"; Drain NPT=1 1/2"; Drain Radius=3/4"; Enclosure Location=20"; Energy Extension=38 1/4"; Flat Side Distance=66 1/2"; Front Skid Extension=100 1/4"; Height to Cold Inlet=20 3/8"; Height to Drain=3 7/8"; Height to Energy=32 5/8"; Height to Hot Outlet=60 7/8"; Height to Relief=61 1/2"; Hot Outlet Angle=90.00°; Hot Water Extension=34 1/4"; Hot Water NPT=3"; Hot Water Radius=1 1/2"; Large Visibility=No; Rear Skid Extension=33 1/4"; Recovery Rate 40F to 140F @15psi=330 gph; Relief Extension=36 1/4"; Skid Center Dist=18"; Skid Length=67"; Skid Spacing=36"; Small Visibility=Yes; Steam Return NPT=3/4"; Steam Return Radius=3/8"; Steam Return Y=1 11/16"; Steam Supply Conn Y=1 5/16"; Steam Supply NPT=1"; Steam Supply Radius=1/2"; Steam Supply Total Z=15 5/16"; Steam Supply X=12 11/16"; Steam Supply Y=1 5/16"; Steam Supply Z=7 1/8"; Steam flow lb/h 40F to 140F @15psi=280; Supply Pipe Conn Y=1 5/16"; U Tube Extension=8 3/16"; U Tube Radius=2 1/4"; Unit Height=81 1/4"; Unit Radius=33 1/4"; Weight=1890
- 2650 L 900A-QSD: Assembly Code=D3040400; Cold Water Extension=34 1/4"; Cold Water NPT=3"; Cold Water Radius=1 1/2"; Control Panel Extension=40 1/4"; Drain Extension=37 1/8"; Drain NPT=1 1/2"; Drain Radius=3/4"; Enclosure Location=20"; Energy Extension=38 1/4"; Flat Side Distance=66 1/2"; Front Skid Extension=100 1/4"; Height to Cold Inlet=20 3/8"; Height to Drain=3 7/8"; Height to Energy=32 5/8"; Height to Hot Outlet=72 7/8"; Height to Relief=73 1/2"; Hot Outlet Angle=90.00°; Hot Water Extension=34 1/4"; Hot Water NPT=3"; Hot Water Radius=1 1/2"; Large Visibility=Yes; Rear Skid Extension=33 1/4"; Recovery Rate 40F to 140F @15psi=2650 gph; Relief Extension=36 1/4"; Skid Center Dist=18"; Skid Length=67"; Skid Spacing=36"; Small Visibility=No; Steam Return NPT=2"; Steam Return Radius=1"; Steam Return Y=4 1/16"; Steam Supply Conn Y=2 11/16"; Steam Supply NPT=2 1/2"; Steam Supply Radius=1 1/4"; Steam Supply Total Z=19 3/4"; Steam Supply X=25 1/2"; Steam Supply Y=8 9/16"; Steam Supply Z=10 13/16"; Steam flow lb/h 40F to 140F @15psi=2300; Supply Pipe Conn Y=11 1/4"; U Tube Extension=8 15/16"; U Tube Radius=5 3/8"; Unit Height=93 1/4"; Unit Radius=33 1/4"; Weight=2570
- 2650 L 750A-QSD: Assembly Code=D3040400; Cold Water Extension=34 1/4"; Cold Water NPT=3"; Cold Water Radius=1 1/2"; Control Panel Extension=40 1/4"; Drain Extension=37 1/8"; Drain NPT=1 1/2"; Drain Radius=3/4"; Enclosure Location=20"; Energy Extension=38 1/4"; Flat Side Distance=66 1/2"; Front Skid Extension=100 1/4"; Height to Cold Inlet=20 3/8"; Height to Drain=3 7/8"; Height to Energy=32 5/8"; Height to Hot Outlet=60 7/8"; Height to Relief=61 1/2"; Hot Outlet Angle=90.00°; Hot Water Extension=34 1/4"; Hot Water NPT=3"; Hot Water Radius=1 1/2"; Large Visibility=Yes; Rear Skid Extension=33 1/4"; Recovery Rate 40F to 140F @15psi=2650 gph; Relief Extension=36 1/4"; Skid Center Dist=18"; Skid Length=67"; Skid Spacing=36"; Small Visibility=No; Steam Return NPT=2"; Steam Return Radius=1"; Steam Return Y=4 1/16"; Steam Supply Conn Y=2 11/16"; Steam Supply NPT=2 1/2"; Steam Supply Radius=1 1/4"; Steam Supply Total Z=19 3/4"; Steam Supply X=25 1/2"; Steam Supply Y=8 9/16"; Steam Supply Z=10 13/16"; Steam flow lb/h 40F to 140F @15psi=2300; Supply Pipe Conn Y=11 1/4"; U Tube Extension=8 15/16"; U Tube Radius=5 3/8"; Unit Height=81 1/4"; Unit Radius=33 1/4"; Weight=2340
- 2280 L 900A-QS: Assembly Code=D3040400; Cold Water Extension=34 1/4"; Cold Water NPT=3"; Cold Water Radius=1 1/2"; Control Panel Extension=40 1/4"; Drain Extension=37 1/8"; Drain NPT=1 1/2"; Drain Radius=3/4"; Enclosure Location=20"; Energy Extension=38 1/4"; Flat Side Distance=66 1/2"; Front Skid Extension=100 1/4"; Height to Cold Inlet=20 3/8"; Height to Drain=3 7/8"; Height to Energy=32 5/8"; Height to Hot Outlet=72 7/8"; Height to Relief=73 1/2"; Hot Outlet Angle=90.00°; Hot Water Extension=34 1/4"; Hot Water NPT=3"; Hot Water Radius=1 1/2"; Large Visibility=Yes; Rear Skid Extension=33 1/4"; Recovery Rate 40F to 140F @15psi=2280 gph; Relief Extension=36 1/4"; Skid Center Dist=18"; Skid Length=67"; Skid Spacing=36"; Small Visibility=No; Steam Return NPT=1 1/4"; Steam Return Radius=5/8"; Steam Return Y=3 3/8"; Steam Supply Conn Y=2 1/4"; Steam Supply NPT=2 1/2"; Steam Supply Radius=1 1/4"; Steam Supply Total Z=19 3/4"; Steam Supply X=25 1/2"; Steam Supply Y=8 9/16"; Steam Supply Z=10 13/16"; Steam flow lb/h 40F to 140F @15psi=1980; Supply Pipe Conn Y=10 13/16"; U Tube Extension=8 15/16"; U Tube Radius=4 5/16"; Unit Height=93 1/4"; Unit Radius=33 1/4"; Weight=2420
- 2280 L 750A-QS: Assembly Code=D3040400; Cold Water Extension=34 1/4"; Cold Water NPT=3"; Cold Water Radius=1 1/2"; Control Panel Extension=40 1/4"; Drain Extension=37 1/8"; Drain NPT=1 1/2"; Drain Radius=3/4"; Enclosure Location=20"; Energy Extension=38 1/4"; Flat Side Distance=66 1/2"; Front Skid Extension=100 1/4"; Height to Cold Inlet=20 3/8"; Height to Drain=3 7/8"; Height to Energy=32 5/8"; Height to Hot Outlet=60 7/8"; Height to Relief=61 1/2"; Hot Outlet Angle=90.00°; Hot Water Extension=34 1/4"; Hot Water NPT=3"; Hot Water Radius=1 1/2"; Large Visibility=Yes; Rear Skid Extension=33 1/4"; Recovery Rate 40F to 140F @15psi=2280 gph; Relief Extension=36 1/4"; Skid Center Dist=18"; Skid Length=67"; Skid Spacing=36"; Small Visibility=No; Steam Return NPT=1 1/4"; Steam Return Radius=5/8"; Steam Return Y=3 3/8"; Steam Supply Conn Y=2 1/4"; Steam Supply NPT=2 1/2"; Steam Supply Radius=1 1/4"; Steam Supply Total Z=19 3/4"; Steam Supply X=25 1/2"; Steam Supply Y=8 9/16"; Steam Supply Z=10 13/16"; Steam flow lb/h 40F to 140F @15psi=1980; Supply Pipe Conn Y=10 13/16"; U Tube Extension=8 15/16"; U Tube Radius=4 5/16"; Unit Height=81 1/4"; Unit Radius=33 1/4"; Weight=2190
- 1940 L 900A-QSD: Assembly Code=D3040400; Cold Water Extension=34 1/4"; Cold Water NPT=3"; Cold Water Radius=1 1/2"; Control Panel Extension=40 1/4"; Drain Extension=37 1/8"; Drain NPT=1 1/2"; Drain Radius=3/4"; Enclosure Location=20"; Energy Extension=38 1/4"; Flat Side Distance=66 1/2"; Front Skid Extension=100 1/4"; Height to Cold Inlet=20 3/8"; Height to Drain=3 7/8"; Height to Energy=32 5/8"; Height to Hot Outlet=72 7/8"; Height to Relief=73 1/2"; Hot Outlet Angle=90.00°; Hot Water Extension=34 1/4"; Hot Water NPT=3"; Hot Water Radius=1 1/2"; Large Visibility=No; Rear Skid Extension=33 1/4"; Recovery Rate 40F to 140F @15psi=1940 gph; Relief Extension=36 1/4"; Skid Center Dist=18"; Skid Length=67"; Skid Spacing=36"; Small Visibility=Yes; Steam Return NPT=1 1/4"; Steam Return Radius=5/8"; Steam Return Y=3 3/8"; Steam Supply Conn Y=2 1/4"; Steam Supply NPT=2 1/2"; Steam Supply Radius=1 1/4"; Steam Supply Total Z=17 1/8"; Steam Supply X=17 3/16"; Steam Supply Y=2 1/4"; Steam Supply Z=8 3/16"; Steam flow lb/h 40F to 140F @15psi=1680; Supply Pipe Conn Y=2 1/4"; U Tube Extension=8 15/16"; U Tube Radius=4 5/16"; Unit Height=93 1/4"; Unit Radius=33 1/4"; Weight=2470
- 1940 L 750A-QSD: Assembly Code=D3040400; Cold Water Extension=34 1/4"; Cold Water NPT=3"; Cold Water Radius=1 1/2"; Control Panel Extension=40 1/4"; Drain Extension=37 1/8"; Drain NPT=1 1/2"; Drain Radius=3/4"; Enclosure Location=20"; Energy Extension=38 1/4"; Flat Side Distance=66 1/2"; Front Skid Extension=100 1/4"; Height to Cold Inlet=20 3/8"; Height to Drain=3 7/8"; Height to Energy=32 5/8"; Height to Hot Outlet=60 7/8"; Height to Relief=61 1/2"; Hot Outlet Angle=90.00°; Hot Water Extension=34 1/4"; Hot Water NPT=3"; Hot Water Radius=1 1/2"; Large Visibility=No; Rear Skid Extension=33 1/4"; Recovery Rate 40F to 140F @15psi=1940 gph; Relief Extension=36 1/4"; Skid Center Dist=18"; Skid Length=67"; Skid Spacing=36"; Small Visibility=Yes; Steam Return NPT=1 1/4"; Steam Return Radius=5/8"; Steam Return Y=3 3/8"; Steam Supply Conn Y=2 1/4"; Steam Supply NPT=2 1/2"; Steam Supply Radius=1 1/4"; Steam Supply Total Z=17 1/8"; Steam Supply X=17 3/16"; Steam Supply Y=2 1/4"; Steam Supply Z=8 3/16"; Steam flow lb/h 40F to 140F @15psi=1680; Supply Pipe Conn Y=2 1/4"; U Tube Extension=8 15/16"; U Tube Radius=4 5/16"; Unit Height=81 1/4"; Unit Radius=33 1/4"; Weight=2240
- 1780 L 900A-QS: Assembly Code=D3040400; Cold Water Extension=34 1/4"; Cold Water NPT=3"; Cold Water Radius=1 1/2"; Control Panel Extension=40 1/4"; Drain Extension=37 1/8"; Drain NPT=1 1/2"; Drain Radius=3/4"; Enclosure Location=20"; Energy Extension=38 1/4"; Flat Side Distance=66 1/2"; Front Skid Extension=100 1/4"; Height to Cold Inlet=20 3/8"; Height to Drain=3 7/8"; Height to Energy=32 5/8"; Height to Hot Outlet=72 7/8"; Height to Relief=73 1/2"; Hot Outlet Angle=90.00°; Hot Water Extension=34 1/4"; Hot Water NPT=3"; Hot Water Radius=1 1/2"; Large Visibility=Yes; Rear Skid Extension=33 1/4"; Recovery Rate 40F to 140F @15psi=1780 gph; Relief Extension=36 1/4"; Skid Center Dist=18"; Skid Length=67"; Skid Spacing=36"; Small Visibility=No; Steam Return NPT=1 1/4"; Steam Return Radius=5/8"; Steam Return Y=3 3/8"; Steam Supply Conn Y=2 1/4"; Steam Supply NPT=2 1/2"; Steam Supply Radius=1 1/4"; Steam Supply Total Z=19 3/4"; Steam Supply X=25 1/2"; Steam Supply Y=8 9/16"; Steam Supply Z=10 13/16"; Steam flow lb/h 40F to 140F @15psi=1540; Supply Pipe Conn Y=10 13/16"; U Tube Extension=8 15/16"; U Tube Radius=4 5/16"; Unit Height=93 1/4"; Unit Radius=33 1/4"; Weight=2370
- 1780 L 750A-QS: Assembly Code=D3040400; Cold Water Extension=34 1/4"; Cold Water NPT=3"; Cold Water Radius=1 1/2"; Control Panel Extension=40 1/4"; Drain Extension=37 1/8"; Drain NPT=1 1/2"; Drain Radius=3/4"; Enclosure Location=20"; Energy Extension=38 1/4"; Flat Side Distance=66 1/2"; Front Skid Extension=100 1/4"; Height to Cold Inlet=20 3/8"; Height to Drain=3 7/8"; Height to Energy=32 5/8"; Height to Hot Outlet=60 7/8"; Height to Relief=61 1/2"; Hot Outlet Angle=90.00°; Hot Water Extension=34 1/4"; Hot Water NPT=3"; Hot Water Radius=1 1/2"; Large Visibility=Yes; Rear Skid Extension=33 1/4"; Recovery Rate 40F to 140F @15psi=1780 gph; Relief Extension=36 1/4"; Skid Center Dist=18"; Skid Length=67"; Skid Spacing=36"; Small Visibility=No; Steam Return NPT=1 1/4"; Steam Return Radius=5/8"; Steam Return Y=3 3/8"; Steam Supply Conn Y=2 1/4"; Steam Supply NPT=2 1/2"; Steam Supply Radius=1 1/4"; Steam Supply Total Z=19 3/4"; Steam Supply X=25 1/2"; Steam Supply Y=8 9/16"; Steam Supply Z=10 13/16"; Steam flow lb/h 40F to 140F @15psi=1540; Supply Pipe Conn Y=10 13/16"; U Tube Extension=8 15/16"; U Tube Radius=4 5/16"; Unit Height=81 1/4"; Unit Radius=33 1/4"; Weight=2140
- 1520 L 900A-QSD: Assembly Code=D3040400; Cold Water Extension=34 1/4"; Cold Water NPT=3"; Cold Water Radius=1 1/2"; Control Panel Extension=40 1/4"; Drain Extension=37 1/8"; Drain NPT=1 1/2"; Drain Radius=3/4"; Enclosure Location=20"; Energy Extension=38 1/4"; Flat Side Distance=66 1/2"; Front Skid Extension=100 1/4"; Height to Cold Inlet=20 3/8"; Height to Drain=3 7/8"; Height to Energy=32 5/8"; Height to Hot Outlet=72 7/8"; Height to Relief=73 1/2"; Hot Outlet Angle=90.00°; Hot Water Extension=34 1/4"; Hot Water NPT=3"; Hot Water Radius=1 1/2"; Large Visibility=No; Rear Skid Extension=33 1/4"; Recovery Rate 40F to 140F @15psi=1520 gph; Relief Extension=36 1/4"; Skid Center Dist=18"; Skid Length=67"; Skid Spacing=36"; Small Visibility=Yes; Steam Return NPT=1 1/4"; Steam Return Radius=5/8"; Steam Return Y=3 3/8"; Steam Supply Conn Y=2 1/4"; Steam Supply NPT=2"; Steam Supply Radius=1"; Steam Supply Total Z=17 1/8"; Steam Supply X=17 3/16"; Steam Supply Y=2 1/4"; Steam Supply Z=8 3/16"; Steam flow lb/h 40F to 140F @15psi=1320; Supply Pipe Conn Y=2 1/4"; U Tube Extension=8 15/16"; U Tube Radius=4 5/16"; Unit Height=93 1/4"; Unit Radius=33 1/4"; Weight=2470
- 1520 L 750A-QSD: Assembly Code=D3040400; Cold Water Extension=34 1/4"; Cold Water NPT=3"; Cold Water Radius=1 1/2"; Control Panel Extension=40 1/4"; Drain Extension=37 1/8"; Drain NPT=1 1/2"; Drain Radius=3/4"; Enclosure Location=20"; Energy Extension=38 1/4"; Flat Side Distance=66 1/2"; Front Skid Extension=100 1/4"; Height to Cold Inlet=20 3/8"; Height to Drain=3 7/8"; Height to Energy=32 5/8"; Height to Hot Outlet=60 7/8"; Height to Relief=61 1/2"; Hot Outlet Angle=90.00°; Hot Water Extension=34 1/4"; Hot Water NPT=3"; Hot Water Radius=1 1/2"; Large Visibility=No; Rear Skid Extension=33 1/4"; Recovery Rate 40F to 140F @15psi=1520 gph; Relief Extension=36 1/4"; Skid Center Dist=18"; Skid Length=67"; Skid Spacing=36"; Small Visibility=Yes; Steam Return NPT=1 1/4"; Steam Return Radius=5/8"; Steam Return Y=3 3/8"; Steam Supply Conn Y=2 1/4"; Steam Supply NPT=2"; Steam Supply Radius=1"; Steam Supply Total Z=17 1/8"; Steam Supply X=17 3/16"; Steam Supply Y=2 1/4"; Steam Supply Z=8 3/16"; Steam flow lb/h 40F to 140F @15psi=1320; Supply Pipe Conn Y=2 1/4"; U Tube Extension=8 15/16"; U Tube Radius=4 5/16"; Unit Height=81 1/4"; Unit Radius=33 1/4"; Weight=2240
- 1230 L 900A-QS: Assembly Code=D3040400; Cold Water Extension=34 1/4"; Cold Water NPT=3"; Cold Water Radius=1 1/2"; Control Panel Extension=40 1/4"; Drain Extension=37 1/8"; Drain NPT=1 1/2"; Drain Radius=3/4"; Enclosure Location=20"; Energy Extension=38 1/4"; Flat Side Distance=66 1/2"; Front Skid Extension=100 1/4"; Height to Cold Inlet=20 3/8"; Height to Drain=3 7/8"; Height to Energy=32 5/8"; Height to Hot Outlet=72 7/8"; Height to Relief=73 1/2"; Hot Outlet Angle=90.00°; Hot Water Extension=34 1/4"; Hot Water NPT=3"; Hot Water Radius=1 1/2"; Large Visibility=Yes; Rear Skid Extension=33 1/4"; Recovery Rate 40F to 140F @15psi=1230 gph; Relief Extension=36 1/4"; Skid Center Dist=18"; Skid Length=67"; Skid Spacing=36"; Small Visibility=No; Steam Return NPT=1"; Steam Return Radius=1/2"; Steam Return Y=2 9/16"; Steam Supply Conn Y=1 7/8"; Steam Supply NPT=2"; Steam Supply Radius=1"; Steam Supply Total Z=17 1/8"; Steam Supply X=17 3/16"; Steam Supply Y=2 1/4"; Steam Supply Z=8 3/16"; Steam flow lb/h 40F to 140F @15psi=1070; Supply Pipe Conn Y=4 1/8"; U Tube Extension=8 15/16"; U Tube Radius=3 3/8"; Unit Height=93 1/4"; Unit Radius=33 1/4"; Weight=2320
- 1230 L 750A-QS: Assembly Code=D3040400; Cold Water Extension=34 1/4"; Cold Water NPT=3"; Cold Water Radius=1 1/2"; Control Panel Extension=40 1/4"; Drain Extension=37 1/8"; Drain NPT=1 1/2"; Drain Radius=3/4"; Enclosure Location=20"; Energy Extension=38 1/4"; Flat Side Distance=66 1/2"; Front Skid Extension=100 1/4"; Height to Cold Inlet=20 3/8"; Height to Drain=3 7/8"; Height to Energy=32 5/8"; Height to Hot Outlet=60 7/8"; Height to Relief=61 1/2"; Hot Outlet Angle=90.00°; Hot Water Extension=34 1/4"; Hot Water NPT=3"; Hot Water Radius=1 1/2"; Large Visibility=Yes; Rear Skid Extension=33 1/4"; Recovery Rate 40F to 140F @15psi=1230 gph; Relief Extension=36 1/4"; Skid Center Dist=18"; Skid Length=67"; Skid Spacing=36"; Small Visibility=No; Steam Return NPT=1"; Steam Return Radius=1/2"; Steam Return Y=2 9/16"; Steam Supply Conn Y=1 7/8"; Steam Supply NPT=2"; Steam Supply Radius=1"; Steam Supply Total Z=17 1/8"; Steam Supply X=17 3/16"; Steam Supply Y=2 1/4"; Steam Supply Z=8 3/16"; Steam flow lb/h 40F to 140F @15psi=1070; Supply Pipe Conn Y=4 1/8"; U Tube Extension=8 15/16"; U Tube Radius=3 3/8"; Unit Height=81 1/4"; Unit Radius=33 1/4"; Weight=2090
- 900 L 900A-QS: Assembly Code=D3040400; Cold Water Extension=34 1/4"; Cold Water NPT=3"; Cold Water Radius=1 1/2"; Control Panel Extension=40 1/4"; Drain Extension=37 1/8"; Drain NPT=1 1/2"; Drain Radius=3/4"; Enclosure Location=20"; Energy Extension=38 1/4"; Flat Side Distance=66 1/2"; Front Skid Extension=100 1/4"; Height to Cold Inlet=20 3/8"; Height to Drain=3 7/8"; Height to Energy=32 5/8"; Height to Hot Outlet=72 7/8"; Height to Relief=73 1/2"; Hot Outlet Angle=90.00°; Hot Water Extension=34 1/4"; Hot Water NPT=3"; Hot Water Radius=1 1/2"; Large Visibility=No; Rear Skid Extension=33 1/4"; Recovery Rate 40F to 140F @15psi=900 gph; Relief Extension=36 1/4"; Skid Center Dist=18"; Skid Length=67"; Skid Spacing=36"; Small Visibility=Yes; Steam Return NPT=1"; Steam Return Radius=1/2"; Steam Return Y=2 9/16"; Steam Supply Conn Y=1 7/8"; Steam Supply NPT=2"; Steam Supply Radius=1"; Steam Supply Total Z=18"; Steam Supply X=14 1/16"; Steam Supply Y=1 7/8"; Steam Supply Z=9 1/16"; Steam flow lb/h 40F to 140F @15psi=780; Supply Pipe Conn Y=1 7/8"; U Tube Extension=8 15/16"; U Tube Radius=3 3/8"; Unit Height=93 1/4"; Unit Radius=33 1/4"; Weight=2320
- 900 L 750A-QS: Assembly Code=D3040400; Cold Water Extension=34 1/4"; Cold Water NPT=3"; Cold Water Radius=1 1/2"; Control Panel Extension=40 1/4"; Drain Extension=37 1/8"; Drain NPT=1 1/2"; Drain Radius=3/4"; Enclosure Location=20"; Energy Extension=38 1/4"; Flat Side Distance=66 1/2"; Front Skid Extension=100 1/4"; Height to Cold Inlet=20 3/8"; Height to Drain=3 7/8"; Height to Energy=32 5/8"; Height to Hot Outlet=60 7/8"; Height to Relief=61 1/2"; Hot Outlet Angle=90.00°; Hot Water Extension=34 1/4"; Hot Water NPT=3"; Hot Water Radius=1 1/2"; Large Visibility=No; Rear Skid Extension=33 1/4"; Recovery Rate 40F to 140F @15psi=900 gph; Relief Extension=36 1/4"; Skid Center Dist=18"; Skid Length=67"; Skid Spacing=36"; Small Visibility=Yes; Steam Return NPT=1"; Steam Return Radius=1/2"; Steam Return Y=2 9/16"; Steam Supply Conn Y=1 7/8"; Steam Supply NPT=2"; Steam Supply Radius=1"; Steam Supply Total Z=18"; Steam Supply X=14 1/16"; Steam Supply Y=1 7/8"; Steam Supply Z=9 1/16"; Steam flow lb/h 40F to 140F @15psi=780; Supply Pipe Conn Y=1 7/8"; U Tube Extension=8 15/16"; U Tube Radius=3 3/8"; Unit Height=81 1/4"; Unit Radius=33 1/4"; Weight=2090
- 830 L 900A-QSD: Assembly Code=D3040400; Cold Water Extension=34 1/4"; Cold Water NPT=3"; Cold Water Radius=1 1/2"; Control Panel Extension=40 1/4"; Drain Extension=37 1/8"; Drain NPT=1 1/2"; Drain Radius=3/4"; Enclosure Location=20"; Energy Extension=38 1/4"; Flat Side Distance=66 1/2"; Front Skid Extension=100 1/4"; Height to Cold Inlet=20 3/8"; Height to Drain=3 7/8"; Height to Energy=32 5/8"; Height to Hot Outlet=72 7/8"; Height to Relief=73 1/2"; Hot Outlet Angle=90.00°; Hot Water Extension=34 1/4"; Hot Water NPT=3"; Hot Water Radius=1 1/2"; Large Visibility=No; Rear Skid Extension=33 1/4"; Recovery Rate 40F to 140F @15psi=830 gph; Relief Extension=36 1/4"; Skid Center Dist=18"; Skid Length=67"; Skid Spacing=36"; Small Visibility=Yes; Steam Return NPT=1"; Steam Return Radius=1/2"; Steam Return Y=2 9/16"; Steam Supply Conn Y=1 7/8"; Steam Supply NPT=1 1/2"; Steam Supply Radius=3/4"; Steam Supply Total Z=18"; Steam Supply X=14 1/16"; Steam Supply Y=1 7/8"; Steam Supply Z=9 1/16"; Steam flow lb/h 40F to 140F @15psi=720; Supply Pipe Conn Y=1 7/8"; U Tube Extension=8 15/16"; U Tube Radius=3 3/8"; Unit Height=93 1/4"; Unit Radius=33 1/4"; Weight=2370
- 830 L 750A-QSD: Assembly Code=D3040400; Cold Water Extension=34 1/4"; Cold Water NPT=3"; Cold Water Radius=1 1/2"; Control Panel Extension=40 1/4"; Drain Extension=37 1/8"; Drain NPT=1 1/2"; Drain Radius=3/4"; Enclosure Location=20"; Energy Extension=38 1/4"; Flat Side Distance=66 1/2"; Front Skid Extension=100 1/4"; Height to Cold Inlet=20 3/8"; Height to Drain=3 7/8"; Height to Energy=32 5/8"; Height to Hot Outlet=60 7/8"; Height to Relief=61 1/2"; Hot Outlet Angle=90.00°; Hot Water Extension=34 1/4"; Hot Water NPT=3"; Hot Water Radius=1 1/2"; Large Visibility=No; Rear Skid Extension=33 1/4"; Recovery Rate 40F to 140F @15psi=830 gph; Relief Extension=36 1/4"; Skid Center Dist=18"; Skid Length=67"; Skid Spacing=36"; Small Visibility=Yes; Steam Return NPT=1"; Steam Return Radius=1/2"; Steam Return Y=2 9/16"; Steam Supply Conn Y=1 7/8"; Steam Supply NPT=1 1/2"; Steam Supply Radius=3/4"; Steam Supply Total Z=18"; Steam Supply X=14 1/16"; Steam Supply Y=1 7/8"; Steam Supply Z=9 1/16"; Steam flow lb/h 40F to 140F @15psi=720; Supply Pipe Conn Y=1 7/8"; U Tube Extension=8 15/16"; U Tube Radius=3 3/8"; Unit Height=81 1/4"; Unit Radius=33 1/4"; Weight=2140
- 3800 L 175A-QS: Assembly Code=D3040400; Cold Water Extension=19 1/8"; Cold Water NPT=2"; Cold Water Radius=1"; Control Panel Extension=25 1/8"; Drain Extension=22"; Drain NPT=1"; Drain Radius=1/2"; Enclosure Location=20"; Energy Extension=34 1/8"; Flat Side Distance=34"; Front Skid Extension=72 5/8"; Height to Cold Inlet=14 13/16"; Height to Drain=1 3/4"; Height to Energy=26 1/2"; Height to Hot Outlet=44 7/8"; Height to Relief=57 7/8"; Hot Outlet Angle=0.00°; Hot Water Extension=19 1/8"; Hot Water NPT=2"; Hot Water Radius=1"; Large Visibility=Yes; Rear Skid Extension=18 1/8"; Recovery Rate 40F to 140F @15psi=3790 gph; Relief Extension=21 1/8"; Skid Center Dist=8 1/2"; Skid Length=54 1/2"; Skid Spacing=17"; Small Visibility=No; Steam Return NPT=2"; Steam Return Radius=1"; Steam Return Y=4 5/8"; Steam Supply Conn Y=3 13/16"; Steam Supply NPT=2 1/2"; Steam Supply Radius=1 1/4"; Steam Supply Total Z=18 15/16"; Steam Supply X=25 1/2"; Steam Supply Y=8 9/16"; Steam Supply Z=10 13/16"; Steam flow lb/h 40F to 140F @15psi=3300; Supply Pipe Conn Y=12 3/8"; U Tube Extension=8 1/8"; U Tube Radius=6 3/8"; Unit Height=69"; Unit Radius=18 1/8"; Weight=1380
- 3800 L 215A-QS: Assembly Code=D3040400; Cold Water Extension=19 1/8"; Cold Water NPT=2"; Cold Water Radius=1"; Control Panel Extension=25 1/8"; Drain Extension=22"; Drain NPT=1"; Drain Radius=1/2"; Enclosure Location=26"; Energy Extension=34 1/8"; Flat Side Distance=34"; Front Skid Extension=73 1/8"; Height to Cold Inlet=14 13/16"; Height to Drain=1 3/4"; Height to Energy=26 1/2"; Height to Hot Outlet=44 7/8"; Height to Relief=64 7/8"; Hot Outlet Angle=0.00°; Hot Water Extension=19 1/8"; Hot Water NPT=2"; Hot Water Radius=1"; Large Visibility=Yes; Rear Skid Extension=18 1/8"; Recovery Rate 40F to 140F @15psi=3790 gph; Relief Extension=21 1/8"; Skid Center Dist=8 1/2"; Skid Length=55"; Skid Spacing=17"; Small Visibility=No; Steam Return NPT=2"; Steam Return Radius=1"; Steam Return Y=4 5/8"; Steam Supply Conn Y=3 13/16"; Steam Supply NPT=2 1/2"; Steam Supply Radius=1 1/4"; Steam Supply Total Z=18 15/16"; Steam Supply X=25 1/2"; Steam Supply Y=8 9/16"; Steam Supply Z=10 13/16"; Steam flow lb/h 40F to 140F @15psi=3300; Supply Pipe Conn Y=12 3/8"; U Tube Extension=8 1/8"; U Tube Radius=6 3/8"; Unit Height=76"; Unit Radius=18 1/8"; Weight=1470

note: column(s) folded — value = type name in every type: Model

## geometry (parser evidence)
native form markers: Sweep x5
no freeform markers — native parametric forms only
